FCSTD DOCUMENT  (FreeCAD 0.18.4R)
Label: Crane-04
License: All rights reserved
LicenseURL: http://en.wikipedia.org/wiki/All_rights_reserved
objects: Part::Cylinder×505, Part::MultiFuse×292, Part::Cut×223, Part::Box×206, Part::Fillet×87, Part::Feature×32, Part::Chamfer×30, Part::Extrusion×26, App::DocumentObjectGroup×7, Part::Mirroring×5, Part::Cone×4, Part::FeaturePython×4, Part::RegularPolygon×2
note: 1416 computed .brp shape members not serialized (recipe doc carries the construction recipe); baked Part::Feature solids carry a one-line shape summary decoded from their .brp

FEATURE [Part::Box] Box001  label="Cube001"
  AttacherType = Attacher::AttachEngine3D
  Height = 125
  Length = 30
  Placement = pos=(1,0,3) rot=(0,-1,0;0.20944rad)
  Width = 25
FEATURE [Part::Box] Box002  label="Cube002"
  AttacherType = Attacher::AttachEngine3D
  Height = 135
  Length = 26
  Placement = pos=(22,0,13) rot=(0,-1,0;0.261799rad)
  Width = 25
FEATURE [Part::Box] Box003  label="Cube003"
  AttacherType = Attacher::AttachEngine3D
  Height = 145
  Length = 35
  Placement = pos=(5,3,1) rot=(0,-1,0;0.20944rad)
  Width = 19
FEATURE [Part::Box] Box007  label="Cube004"
  AttacherType = Attacher::AttachEngine3D
  Height = 11
  Length = 25
  Placement = pos=(1,0,-2) rot=(0,0,1;0rad)
  Width = 25
FEATURE [Part::Fillet] Fillet
  Base = -> Box002
  Edges = 1 edges r=10: [Edge4]
  Placement = pos=(6,0,4) rot=(0,0,1;0rad)
FEATURE [Part::Box] Box017  label="Cube015"
  AttacherType = Attacher::AttachEngine3D
  Height = 30
  Length = 35
  Placement = pos=(1,0,0) rot=(0,0,1;0rad)
  Width = 25
FEATURE [Part::Box] Box018  label="Cube016"
  AttacherType = Attacher::AttachEngine3D
  Height = 30
  Length = 190
  Placement = pos=(1,0,105) rot=(0,0,1;0rad)
  Width = 25
FEATURE [Part::Box] Box019  label="Cube017"
  AttacherType = Attacher::AttachEngine3D
  Height = 10
  Length = 80
  Placement = pos=(65,0,105) rot=(0,0,1;0rad)
  Width = 25
FEATURE [Part::Cut] Cut002
  Base = -> Box018
  Refine = true
  Tool = -> Box019
FEATURE [Part::Feature] Solid
  shape: bbox 71.89 x 27.5 x 16.57 mm, 5 faces (baked)
FEATURE [Part::Cut] Cut003
  Base = -> Cut002
  Refine = true
  Tool = -> Solid
FEATURE [Part::Box] Box020  label="Cube018"
  AttacherType = Attacher::AttachEngine3D
  Height = 5
  Length = 46
  Placement = pos=(145,0,105) rot=(0,0,1;0rad)
  Width = 25
FEATURE [Part::Cut] Cut004
  Base = -> Cut003
  Refine = true
  Tool = -> Box020
FEATURE [Part::Feature] Solid001
  shape: bbox 51.52 x 27.5 x 8.266 mm, 5 faces (baked)
FEATURE [Part::Cut] Cut005
  Base = -> Cut004
  Refine = true
  Tool = -> Solid001
FEATURE [Part::Box] Box021  label="Cube019"
  AttacherType = Attacher::AttachEngine3D
  Height = 19
  Length = 46
  Placement = pos=(0,0,115) rot=(0,-1,0;0.610865rad)
  Width = 25
FEATURE [Part::Chamfer] Chamfer
  Base = -> Cut005
  Edges = 1 edges: [Edge13 r1=20 r2=18]
FEATURE [Part::Cut] Cut006
  Base = -> Chamfer
  Placement = pos=(-19,0,10) rot=(0,0,1;0rad)
  Refine = true
  Tool = -> Box021
FEATURE [Part::Box] Box022  label="Cube020"
  AttacherType = Attacher::AttachEngine3D
  Height = 30
  Length = 190
  Placement = pos=(-18,3,112) rot=(0,0,1;0rad)
  Width = 19
FEATURE [Part::Cut] Cut007
  Base = -> Cut006
  Placement = pos=(0,0,1) rot=(0,0,1;0rad)
  Refine = true
  Tool = -> Box022
FEATURE [Part::Fillet] Fillet003
  Base = -> Cut007
  Edges = 6 edges r=3: [Edge9,Edge13,Edge15,Edge17,Edge30,Edge41]
  Placement = pos=(-98.4842,0,33.7999) rot=(0,1,0;0.872665rad)
FEATURE [Part::Feature] Face001
  shape: bbox 65.47 x 2e-07 x 51.48 mm, 1 faces, 0 solids (baked)
FEATURE [Part::Extrusion] Extrude001
  Base = -> Face001
  Dir = (0,3,0)
  DirMode = 0
  FaceMakerClass = Part::FaceMakerExtrusion
  LengthFwd = 0
  LengthRev = 0
  Placement = pos=(0,-1,0) rot=(0,0,1;0rad)
  Solid = false
  Symmetric = false
FEATURE [Part::Fillet] Fillet006
  Base = -> Extrude001
  Edges = 1 edges r=3: [Edge8]
FEATURE [Part::Fillet] Fillet007
  Base = -> Fillet006
  Edges = 2 edges r=5: [Edge3,Edge12]
FEATURE [Part::Cylinder] Cylinder
  Angle = 360
  AttacherType = Attacher::AttachEngine3D
  Height = 25
  Placement = pos=(-13,25,122.5) rot=(1,0,0;1.5708rad)
  Radius = 5
FEATURE [Part::Box] Box023  label="Cube021"
  AttacherType = Attacher::AttachEngine3D
  Height = 64
  Length = 26
  Placement = pos=(-19,0,87) rot=(0,-1,0;0.279253rad)
  Width = 25
FEATURE [Part::Cut] Cut008
  Base = -> Fillet003
  Placement = pos=(89.1967,0,53.7171) rot=(0,-1,0;0.872665rad)
  Refine = true
  Tool = -> Box023
FEATURE [Part::Fillet] Fillet008
  Base = -> Cut008
  Edges = 2 edges r=3: [Edge21,Edge25]
FEATURE [Part::Cylinder] Cylinder001
  Angle = 360
  AttacherType = Attacher::AttachEngine3D
  Height = 27
  Placement = pos=(-13,26,122.5) rot=(1,0,0;1.5708rad)
  Radius = 3.1
FEATURE [Part::Cylinder] Cylinder002
  Angle = 360
  AttacherType = Attacher::AttachEngine3D
  Height = 27
  Placement = pos=(31,26,7) rot=(1,0,0;1.5708rad)
  Radius = 1.5
FEATURE [Part::Cylinder] Cylinder003
  Angle = 360
  AttacherType = Attacher::AttachEngine3D
  Height = 29
  Placement = pos=(20,27,130) rot=(1,0,0;1.5708rad)
  Radius = 1.5
FEATURE [Part::Cylinder] Cylinder004
  Angle = 360
  AttacherType = Attacher::AttachEngine3D
  Height = 25
  Placement = pos=(166,25,126) rot=(1,0,0;1.5708rad)
  Radius = 1.6
FEATURE [Part::Box] Box  label="Cube"
  AttacherType = Attacher::AttachEngine3D
  Height = 26
  Length = 40
  Placement = pos=(131,0,105) rot=(0,0,1;0rad)
  Width = 5
FEATURE [Part::Box] Box024  label="Cube022"
  AttacherType = Attacher::AttachEngine3D
  Height = 25
  Length = 60
  Placement = pos=(108,0,105) rot=(0,1,0;0.357792rad)
  Width = 5
FEATURE [Part::Cut] Cut009
  Base = -> Box
  Refine = true
  Tool = -> Box024
FEATURE [Part::Cylinder] Cylinder005
  Angle = 360
  AttacherType = Attacher::AttachEngine3D
  Height = 25
  Placement = pos=(166,25,115) rot=(1,0,0;1.5708rad)
  Radius = 1.6
FEATURE [Part::Cylinder] Cylinder006
  Angle = 360
  AttacherType = Attacher::AttachEngine3D
  Height = 25
  Placement = pos=(136,25,126) rot=(1,0,0;1.5708rad)
  Radius = 1.6
FEATURE [Part::Fillet] Fillet009
  Base = -> Cut009
  Edges = 4 edges r=3: [Edge2,Edge4,Edge9,Edge12]
  Placement = pos=(0,3,0) rot=(0,0,1;0rad)
FEATURE [Part::Box] Box025  label="Cube023"
  AttacherType = Attacher::AttachEngine3D
  Height = 26
  Length = 40
  Placement = pos=(131,0,105) rot=(0,0,1;0rad)
  Width = 5
FEATURE [Part::Box] Box026  label="Cube024"
  AttacherType = Attacher::AttachEngine3D
  Height = 25
  Length = 60
  Placement = pos=(108,0,105) rot=(0,1,0;0.357792rad)
  Width = 5
FEATURE [Part::Cut] Cut010
  Base = -> Box025
  Refine = true
  Tool = -> Box026
FEATURE [Part::Fillet] Fillet010
  Base = -> Cut010
  Edges = 4 edges r=3: [Edge2,Edge4,Edge9,Edge12]
  Placement = pos=(0,25,0) rot=(0,0,1;0rad)
FEATURE [Part::Cylinder] Cylinder007
  Angle = 360
  AttacherType = Attacher::AttachEngine3D
  Height = 25
  Placement = pos=(166,25,126) rot=(1,0,0;1.5708rad)
  Radius = 1.25
FEATURE [Part::Cylinder] Cylinder008
  Angle = 360
  AttacherType = Attacher::AttachEngine3D
  Height = 25
  Placement = pos=(136,25,126) rot=(1,0,0;1.5708rad)
  Radius = 1.25
FEATURE [Part::Cylinder] Cylinder009
  Angle = 360
  AttacherType = Attacher::AttachEngine3D
  Height = 25
  Placement = pos=(166,25,115) rot=(1,0,0;1.5708rad)
  Radius = 1.25
FEATURE [Part::MultiFuse] Fusion002
  Refine = true
  Shapes = -> [Cylinder004,Cylinder006,Cylinder005]
FEATURE [Part::MultiFuse] Fusion003
  Placement = pos=(0,5,0) rot=(0,0,1;0rad)
  Refine = true
  Shapes = -> [Cylinder007,Cylinder009,Cylinder008]
FEATURE [Part::Box] Box027  label="Cube025"
  AttacherType = Attacher::AttachEngine3D
  Height = 200
  Length = 29
  Placement = pos=(155,30,-59) rot=(0,0,1;0rad)
  Width = 17
FEATURE [Part::Box] Box028  label="Cube026"
  AttacherType = Attacher::AttachEngine3D
  Height = 200
  Length = 20.5
  Placement = pos=(159.25,33.25,-59) rot=(0,0,1;0rad)
  Width = 10.5
FEATURE [Part::Cylinder] Cylinder013
  Angle = 360
  AttacherType = Attacher::AttachEngine3D
  Height = 12
  Placement = pos=(13,12.5,-3) rot=(0,0,1;0rad)
  Radius = 2.5
FEATURE [Part::Box] Box030  label="Cube028"
  AttacherType = Attacher::AttachEngine3D
  Height = 5
  Length = 35
  Placement = pos=(1,3,4) rot=(0,0,1;0rad)
  Width = 19
FEATURE [Part::Cylinder] Cylinder020
  Angle = 360
  AttacherType = Attacher::AttachEngine3D
  Height = 25
  Placement = pos=(-19.5,25,121.5) rot=(1,0,0;1.5708rad)
  Radius = 4
FEATURE [Part::Cylinder] Cylinder028
  Angle = 360
  AttacherType = Attacher::AttachEngine3D
  Height = 25
  Placement = pos=(-4,25,63) rot=(1,0,0;1.5708rad)
  Radius = 5
FEATURE [Part::Cylinder] Cylinder029
  Angle = 360
  AttacherType = Attacher::AttachEngine3D
  Height = 25
  Placement = pos=(31,25,7) rot=(1,0,0;1.5708rad)
  Radius = 5
FEATURE [Part::Chamfer] Chamfer002
  Base = -> Fillet008
  Edges = 2 edges r=6: [Edge58,Edge66]
FEATURE [Part::Cylinder] Cylinder030
  Angle = 360
  AttacherType = Attacher::AttachEngine3D
  Height = 26
  Radius = 7.5
FEATURE [Part::Box] Box036  label="Cube034"
  AttacherType = Attacher::AttachEngine3D
  Height = 26
  Length = 10.4
  Placement = pos=(-5.2,-8.05,0) rot=(0,0,1;0rad)
  Width = 16.1
FEATURE [Part::Cut] Cut020
  Base = -> Cylinder030
  Refine = true
  Tool = -> Box036
FEATURE [Part::Cone] Cone
  Angle = 360
  AttacherType = Attacher::AttachEngine3D
  Height = 13
  Placement = pos=(0,0,-13) rot=(0,0,1;0rad)
  Radius1 = 5
  Radius2 = 7.5
FEATURE [Part::Box] Box037  label="Cube035"
  AttacherType = Attacher::AttachEngine3D
  Height = 12
  Length = 16
  Placement = pos=(-8,3,-12) rot=(0,0,1;0rad)
  Width = 10
FEATURE [Part::Box] Box038  label="Cube036"
  AttacherType = Attacher::AttachEngine3D
  Height = 12
  Length = 16
  Placement = pos=(-8,-13,-12) rot=(0,0,1;0rad)
  Width = 10
FEATURE [Part::MultiFuse] Fusion020
  Placement = pos=(0,0,-1) rot=(0,0,1;0rad)
  Refine = true
  Shapes = -> [Box038,Box037]
FEATURE [Part::Cylinder] Cylinder031
  Angle = 360
  AttacherType = Attacher::AttachEngine3D
  Height = 10
  Placement = pos=(0,5,-8) rot=(1,0,0;1.5708rad)
  Radius = 3.1
FEATURE [Part::Cylinder] Cylinder032
  Angle = 360
  AttacherType = Attacher::AttachEngine3D
  Height = 2
  Placement = pos=(0,0,-2) rot=(0,0,1;0rad)
  Radius = 7.5
FEATURE [Part::Cut] Cut021
  Base = -> Cone
  Refine = true
  Tool = -> Fusion020
FEATURE [Part::MultiFuse] Fusion021
  Refine = true
  Shapes = -> [Cut020,Cut021,Cylinder032]
FEATURE [Part::Cut] Cut022
  Base = -> Fusion021
  Refine = true
  Tool = -> Cylinder031
FEATURE [Part::Cylinder] Cylinder033
  Angle = 360
  AttacherType = Attacher::AttachEngine3D
  Height = 16
  Radius = 7.5
FEATURE [Part::Cylinder] Cylinder034
  Angle = 360
  AttacherType = Attacher::AttachEngine3D
  Height = 16
  Radius = 6.25
FEATURE [Part::Cut] Cut023
  Base = -> Cylinder033
  Refine = true
  Tool = -> Cylinder034
FEATURE [Part::MultiFuse] Fusion022
  Refine = true
  Shapes = -> [Cut022,Cut023]
FEATURE [Part::Box] Box004  label="Cube006"
  AttacherType = Attacher::AttachEngine3D
  Height = 2.5
  Length = 10
  Placement = pos=(2,-2,-0.5) rot=(0,0,1;0rad)
  Width = 4
FEATURE [Part::Cut] Cut024
  Base = -> Fusion022
  Placement = pos=(0,40,0) rot=(-1,0,0;1.5708rad)
  Refine = true
  Tool = -> Box004
FEATURE [Part::Cylinder] Cylinder014
  Angle = 360
  AttacherType = Attacher::AttachEngine3D
  Height = 5
  Placement = pos=(0,0,4) rot=(0,0,1;0rad)
  Radius = 3
FEATURE [Part::Cylinder] Cylinder015
  Angle = 360
  AttacherType = Attacher::AttachEngine3D
  Height = 8
  Placement = pos=(0,4,0) rot=(1,0,0;1.5708rad)
  Radius = 6
FEATURE [Part::Cylinder] Cylinder035
  Angle = 360
  AttacherType = Attacher::AttachEngine3D
  Height = 8
  Placement = pos=(0,4,0) rot=(1,0,0;1.5708rad)
  Radius = 3.1
FEATURE [Part::Cut] Cut025
  Base = -> Cylinder015
  Placement = pos=(0,0,-1) rot=(0,0,1;0rad)
  Refine = true
  Tool = -> Cylinder035
FEATURE [Part::Box] Box005  label="Cube007"
  AttacherType = Attacher::AttachEngine3D
  Height = 10
  Length = 6
  Placement = pos=(-3,2,4) rot=(0,0,1;0rad)
  Width = 2
FEATURE [Part::Box] Box006  label="Cube009"
  AttacherType = Attacher::AttachEngine3D
  Height = 10
  Length = 10
  Placement = pos=(-5,-5,4) rot=(0,0,1;0rad)
  Width = 10
FEATURE [Part::Cut] Cut026
  Base = -> Cut025
  Refine = true
  Tool = -> Box006
FEATURE [Part::Cut] Cut027
  Base = -> Cylinder014
  Refine = true
  Tool = -> Box005
FEATURE [Part::MultiFuse] Fusion023  label="cylinder-piston-head-attach"
  Placement = pos=(0,0,168) rot=(1,0,0;3.14159rad)
  Refine = true
  Shapes = -> [Cut026,Cut027]
FEATURE [Part::Fillet] Fillet012  label="cylinder-motor-holder"
  Base = -> Cut024
  Edges = 3 edges r=3: [Edge56,Edge61,Edge65]
  Placement = pos=(0,0,0) rot=(1,0,0;1.5708rad)
FEATURE [Part::Cylinder] Cylinder036  label="cylinder-jacket"
  Angle = 360
  AttacherType = Attacher::AttachEngine3D
  Height = 85
  Placement = pos=(0,0,38) rot=(0,0,1;0rad)
  Radius = 8
FEATURE [Part::MultiFuse] Fusion024  label="cylinder-body"
  Placement = pos=(31,12.5,-20) rot=(0,0,1;0rad)
  Refine = true
  Shapes = -> [Cylinder036,Fillet012]
FEATURE [Part::Cylinder] Cylinder037  label="cylinder-piston-rod"
  Angle = 360
  AttacherType = Attacher::AttachEngine3D
  Height = 80
  Placement = pos=(0,0,84) rot=(0,0,1;0rad)
  Radius = 4
FEATURE [Part::MultiFuse] Fusion025  label="cylinder-piston"
  Placement = pos=(31,12.5,-33.5) rot=(0,0,1;0rad)
  Refine = true
  Shapes = -> [Fusion023,Cylinder037]
FEATURE [Part::Box] Box039  label="Cube037"
  AttacherType = Attacher::AttachEngine3D
  Height = 14
  Length = 15
  Placement = pos=(23,9,1) rot=(0,0,1;0rad)
  Width = 7
FEATURE [Part::Feature] Face007
  shape: bbox 32.17 x 2e-07 x 34.8 mm, 1 faces, 0 solids (baked)
FEATURE [Part::Extrusion] Extrude007
  Base = -> Face007
  Dir = (0,3,0)
  DirMode = 0
  FaceMakerClass = Part::FaceMakerExtrusion
  LengthFwd = 0
  LengthRev = 0
  Solid = false
  Symmetric = false
FEATURE [Part::Fillet] Fillet013
  Base = -> Extrude007
  Edges = 1 edges r=1: [Edge5]
  Placement = pos=(0,-1,0) rot=(0,0,1;0rad)
FEATURE [Part::MultiFuse] Fusion034
  Refine = true
  Shapes = -> [Fillet007,Fillet013]
FEATURE [Part::Fillet] Fillet016
  Base = -> Fusion034
  Edges = 1 edges r=1: [Edge22]
FEATURE [Part::Cylinder] Cylinder044
  Angle = 360
  AttacherType = Attacher::AttachEngine3D
  Height = 29
  Placement = pos=(-3,27,133) rot=(1,0,0;1.5708rad)
  Radius = 1.5
FEATURE [Part::Cylinder] Cylinder045
  Angle = 360
  AttacherType = Attacher::AttachEngine3D
  Height = 29
  Placement = pos=(11,27,142) rot=(1,0,0;1.5708rad)
  Radius = 1.5
FEATURE [Part::Cylinder] Cylinder047
  Angle = 360
  AttacherType = Attacher::AttachEngine3D
  Height = 29
  Placement = pos=(38,27,129) rot=(1,0,0;1.5708rad)
  Radius = 1.5
FEATURE [Part::Cylinder] Cylinder048
  Angle = 360
  AttacherType = Attacher::AttachEngine3D
  Height = 27
  Placement = pos=(-13,26,122.5) rot=(1,0,0;1.5708rad)
  Radius = 1.5
FEATURE [Part::MultiFuse] Fusion035
  Refine = true
  Shapes = -> [Cylinder003,Cylinder044,Cylinder045,Cylinder047,Cylinder048]
FEATURE [Part::Cut] Cut037  label="crane-secondary-arm-left-plate"
  Base = -> Fillet016
  Placement = pos=(162,58,35) rot=(0,0,1;0rad)
  Refine = true
  Tool = -> Fusion035
FEATURE [Part::Feature] Face008
  shape: bbox 65.47 x 2e-07 x 51.48 mm, 1 faces, 0 solids (baked)
FEATURE [Part::Extrusion] Extrude008
  Base = -> Face008
  Dir = (0,3,0)
  DirMode = 0
  FaceMakerClass = Part::FaceMakerExtrusion
  LengthFwd = 0
  LengthRev = 0
  Placement = pos=(0,-1,0) rot=(0,0,1;0rad)
  Solid = false
  Symmetric = false
FEATURE [Part::Fillet] Fillet017
  Base = -> Extrude008
  Edges = 1 edges r=3: [Edge8]
FEATURE [Part::Fillet] Fillet018
  Base = -> Fillet017
  Edges = 2 edges r=5: [Edge3,Edge12]
FEATURE [Part::Cylinder] Cylinder049
  Angle = 360
  AttacherType = Attacher::AttachEngine3D
  Height = 29
  Placement = pos=(20,27,130) rot=(1,0,0;1.5708rad)
  Radius = 1.5
FEATURE [Part::Feature] Face009
  shape: bbox 32.17 x 2e-07 x 34.8 mm, 1 faces, 0 solids (baked)
FEATURE [Part::Extrusion] Extrude009
  Base = -> Face009
  Dir = (0,3,0)
  DirMode = 0
  FaceMakerClass = Part::FaceMakerExtrusion
  LengthFwd = 0
  LengthRev = 0
  Solid = false
  Symmetric = false
FEATURE [Part::Fillet] Fillet019
  Base = -> Extrude009
  Edges = 1 edges r=1: [Edge5]
  Placement = pos=(0,-1,0) rot=(0,0,1;0rad)
FEATURE [Part::MultiFuse] Fusion036
  Refine = true
  Shapes = -> [Fillet018,Fillet019]
FEATURE [Part::Fillet] Fillet020
  Base = -> Fusion036
  Edges = 1 edges r=1: [Edge22]
FEATURE [Part::Cylinder] Cylinder050
  Angle = 360
  AttacherType = Attacher::AttachEngine3D
  Height = 29
  Placement = pos=(-3,27,133) rot=(1,0,0;1.5708rad)
  Radius = 1.5
FEATURE [Part::Cylinder] Cylinder051
  Angle = 360
  AttacherType = Attacher::AttachEngine3D
  Height = 29
  Placement = pos=(11,27,142) rot=(1,0,0;1.5708rad)
  Radius = 1.5
FEATURE [Part::Cylinder] Cylinder052
  Angle = 360
  AttacherType = Attacher::AttachEngine3D
  Height = 29
  Placement = pos=(38,27,129) rot=(1,0,0;1.5708rad)
  Radius = 1.5
FEATURE [Part::Cylinder] Cylinder053
  Angle = 360
  AttacherType = Attacher::AttachEngine3D
  Height = 27
  Placement = pos=(-13,26,122.5) rot=(1,0,0;1.5708rad)
  Radius = 1.5
FEATURE [Part::MultiFuse] Fusion037
  Refine = true
  Shapes = -> [Cylinder049,Cylinder050,Cylinder051,Cylinder052,Cylinder053]
FEATURE [Part::Cut] Cut038  label="crane-secondary-arm-right-plate"
  Base = -> Fillet020
  Placement = pos=(162,86,35) rot=(0,0,1;0rad)
  Refine = true
  Tool = -> Fusion037
FEATURE [Part::Cylinder] Cylinder055
  Angle = 360
  AttacherType = Attacher::AttachEngine3D
  Height = 25
  Placement = pos=(11,25,142) rot=(1,0,0;1.5708rad)
  Radius = 4
FEATURE [Part::Cylinder] Cylinder065
  Angle = 360
  AttacherType = Attacher::AttachEngine3D
  Height = 19
  Placement = pos=(20,22,130) rot=(1,0,0;1.5708rad)
  Radius = 5
FEATURE [Part::Cylinder] Cylinder066
  Angle = 360
  AttacherType = Attacher::AttachEngine3D
  Height = 25
  Placement = pos=(43,25,129) rot=(1,0,0;1.5708rad)
  Radius = 1.6
FEATURE [Part::Cylinder] Cylinder071
  Angle = 360
  AttacherType = Attacher::AttachEngine3D
  Height = 25
  Placement = pos=(166,25,126.5) rot=(1,0,0;1.5708rad)
  Radius = 3.1
FEATURE [Part::MultiFuse] Fusion044  label="cylinder-lifter"
  Placement = pos=(163,60,26.5) rot=(0,-1,0;0.094248rad)
  Refine = true
  Shapes = -> [Fusion025,Fusion024]
FEATURE [Part::Cylinder] Cylinder072
  Angle = 360
  AttacherType = Attacher::AttachEngine3D
  Height = 26
  Radius = 7.5
FEATURE [Part::Box] Box040  label="Cube038"
  AttacherType = Attacher::AttachEngine3D
  Height = 26
  Length = 10.4
  Placement = pos=(-5.2,-8.05,0) rot=(0,0,1;0rad)
  Width = 16.1
FEATURE [Part::Cut] Cut039
  Base = -> Cylinder072
  Refine = true
  Tool = -> Box040
FEATURE [Part::Cone] Cone001
  Angle = 360
  AttacherType = Attacher::AttachEngine3D
  Height = 13
  Placement = pos=(0,0,-13) rot=(0,0,1;0rad)
  Radius1 = 5
  Radius2 = 7.5
FEATURE [Part::Box] Box041  label="Cube039"
  AttacherType = Attacher::AttachEngine3D
  Height = 12
  Length = 16
  Placement = pos=(-8,3,-12) rot=(0,0,1;0rad)
  Width = 10
FEATURE [Part::Box] Box042  label="Cube040"
  AttacherType = Attacher::AttachEngine3D
  Height = 12
  Length = 16
  Placement = pos=(-8,-13,-12) rot=(0,0,1;0rad)
  Width = 10
FEATURE [Part::MultiFuse] Fusion045
  Placement = pos=(0,0,-1) rot=(0,0,1;0rad)
  Refine = true
  Shapes = -> [Box042,Box041]
FEATURE [Part::Cylinder] Cylinder073
  Angle = 360
  AttacherType = Attacher::AttachEngine3D
  Height = 10
  Placement = pos=(0,5,-8) rot=(1,0,0;1.5708rad)
  Radius = 3.1
FEATURE [Part::Cylinder] Cylinder074
  Angle = 360
  AttacherType = Attacher::AttachEngine3D
  Height = 2
  Placement = pos=(0,0,-2) rot=(0,0,1;0rad)
  Radius = 7.5
FEATURE [Part::Cut] Cut040
  Base = -> Cone001
  Refine = true
  Tool = -> Fusion045
FEATURE [Part::MultiFuse] Fusion046
  Refine = true
  Shapes = -> [Cut039,Cut040,Cylinder074]
FEATURE [Part::Cut] Cut041
  Base = -> Fusion046
  Refine = true
  Tool = -> Cylinder073
FEATURE [Part::Cylinder] Cylinder075
  Angle = 360
  AttacherType = Attacher::AttachEngine3D
  Height = 16
  Radius = 7.5
FEATURE [Part::Cylinder] Cylinder076
  Angle = 360
  AttacherType = Attacher::AttachEngine3D
  Height = 16
  Radius = 6.25
FEATURE [Part::Cut] Cut042
  Base = -> Cylinder075
  Refine = true
  Tool = -> Cylinder076
FEATURE [Part::MultiFuse] Fusion047
  Refine = true
  Shapes = -> [Cut041,Cut042]
FEATURE [Part::Box] Box043  label="Cube041"
  AttacherType = Attacher::AttachEngine3D
  Height = 2.5
  Length = 10
  Placement = pos=(2,-2,-0.5) rot=(0,0,1;0rad)
  Width = 4
FEATURE [Part::Cut] Cut043
  Base = -> Fusion047
  Placement = pos=(0,40,0) rot=(-1,0,0;1.5708rad)
  Refine = true
  Tool = -> Box043
FEATURE [Part::Cylinder] Cylinder077
  Angle = 360
  AttacherType = Attacher::AttachEngine3D
  Height = 5
  Placement = pos=(0,0,4) rot=(0,0,1;0rad)
  Radius = 3
FEATURE [Part::Cylinder] Cylinder078
  Angle = 360
  AttacherType = Attacher::AttachEngine3D
  Height = 8
  Placement = pos=(0,4,0) rot=(1,0,0;1.5708rad)
  Radius = 6
FEATURE [Part::Cylinder] Cylinder079
  Angle = 360
  AttacherType = Attacher::AttachEngine3D
  Height = 8
  Placement = pos=(0,4,0) rot=(1,0,0;1.5708rad)
  Radius = 3.1
FEATURE [Part::Cut] Cut044
  Base = -> Cylinder078
  Placement = pos=(0,0,-1) rot=(0,0,1;0rad)
  Refine = true
  Tool = -> Cylinder079
FEATURE [Part::Box] Box044  label="Cube042"
  AttacherType = Attacher::AttachEngine3D
  Height = 10
  Length = 6
  Placement = pos=(-3,2,4) rot=(0,0,1;0rad)
  Width = 2
FEATURE [Part::Box] Box045  label="Cube043"
  AttacherType = Attacher::AttachEngine3D
  Height = 10
  Length = 10
  Placement = pos=(-5,-5,4) rot=(0,0,1;0rad)
  Width = 10
FEATURE [Part::Cut] Cut045
  Base = -> Cut044
  Refine = true
  Tool = -> Box045
FEATURE [Part::Cut] Cut046
  Base = -> Cylinder077
  Refine = true
  Tool = -> Box044
FEATURE [Part::MultiFuse] Fusion048  label="cylinder-piston-head-attach001"
  Placement = pos=(0,0,168) rot=(1,0,0;3.14159rad)
  Refine = true
  Shapes = -> [Cut045,Cut046]
FEATURE [Part::Fillet] Fillet021  label="cylinder-motor-holder001"
  Base = -> Cut043
  Edges = 3 edges r=3: [Edge56,Edge61,Edge65]
  Placement = pos=(0,0,0) rot=(1,0,0;1.5708rad)
FEATURE [Part::Cylinder] Cylinder080  label="cylinder-jacket001"
  Angle = 360
  AttacherType = Attacher::AttachEngine3D
  Height = 85
  Placement = pos=(0,0,38) rot=(0,0,1;0rad)
  Radius = 8
FEATURE [Part::MultiFuse] Fusion049  label="cylinder-body001"
  Placement = pos=(31,12.5,-20) rot=(0,0,1;0rad)
  Refine = true
  Shapes = -> [Cylinder080,Fillet021]
FEATURE [Part::Cylinder] Cylinder081  label="cylinder-piston-rod001"
  Angle = 360
  AttacherType = Attacher::AttachEngine3D
  Height = 53
  Placement = pos=(0,0,111) rot=(0,0,1;0rad)
  Radius = 4
FEATURE [Part::MultiFuse] Fusion050  label="cylinder-piston001"
  Placement = pos=(31,12.5,-12) rot=(0,0,1;0rad)
  Refine = true
  Shapes = -> [Fusion048,Cylinder081]
FEATURE [Part::MultiFuse] Fusion051  label="cylinder-arm"
  Placement = pos=(196.5,60,197) rot=(0,1,0;1.64934rad)
  Refine = true
  Shapes = -> [Fusion050,Fusion049]
FEATURE [Part::Cylinder] Cylinder082  label="Cylinder080"
  Angle = 360
  AttacherType = Attacher::AttachEngine3D
  Height = 11
  Placement = pos=(9,18,-2) rot=(0,0,1;0rad)
  Radius = 1.25
FEATURE [Part::Cylinder] Cylinder083  label="Cylinder081"
  Angle = 360
  AttacherType = Attacher::AttachEngine3D
  Height = 11
  Placement = pos=(9,7,-2) rot=(0,0,1;0rad)
  Radius = 1.25
FEATURE [Part::Cylinder] Cylinder084  label="Cylinder259"
  Angle = 360
  AttacherType = Attacher::AttachEngine3D
  Height = 11
  Placement = pos=(18,18,-2) rot=(0,0,1;0rad)
  Radius = 1.25
FEATURE [Part::Cylinder] Cylinder085  label="Cylinder260"
  Angle = 360
  AttacherType = Attacher::AttachEngine3D
  Height = 11
  Placement = pos=(18,7,-2) rot=(0,0,1;0rad)
  Radius = 1.25
FEATURE [Part::Box] Box046  label="Cube044"
  AttacherType = Attacher::AttachEngine3D
  Height = 18
  Length = 13
  Placement = pos=(29,3,125) rot=(0,0,1;0rad)
  Width = 19
FEATURE [Part::Fillet] Fillet022
  Base = -> Box046
  Edges = 2 edges r=4: [Edge4,Edge8]
FEATURE [Part::Box] Box047  label="Cube045"
  AttacherType = Attacher::AttachEngine3D
  Height = 12
  Length = 13
  Placement = pos=(31,9,125) rot=(0,0,1;0rad)
  Width = 7
FEATURE [Part::Cut] Cut048
  Base = -> Fillet022
  Refine = true
  Tool = -> Box047
FEATURE [Part::Fillet] Fillet023
  Base = -> Cut048
  Edges = 1 edges r=3: [Edge35]
  Placement = pos=(5,0,0.5) rot=(0,0,1;0rad)
FEATURE [Part::Cylinder] Cylinder086  label="Cylinder261"
  Angle = 360
  AttacherType = Attacher::AttachEngine3D
  Height = 29
  Placement = pos=(20,27,130) rot=(1,0,0;1.5708rad)
  Radius = 1.6
FEATURE [Part::Cylinder] Cylinder087  label="Cylinder262"
  Angle = 360
  AttacherType = Attacher::AttachEngine3D
  Height = 25
  Placement = pos=(328,85,161.5) rot=(1,0,0;1.5708rad)
  Radius = 1.5
FEATURE [Part::RegularPolygon] RegularPolygon001  label="Regular polygon001"
  AttacherType = Attacher::AttachEngine3D
  Circumradius = 3.25
  Placement = pos=(5,0,4) rot=(1,0,0;1.5708rad)
  Polygon = 6
FEATURE [Part::Feature] Face
  shape: bbox 8.306 x 2e-07 x 8.194 mm, 1 faces, 0 solids (baked)
FEATURE [Part::Extrusion] Extrude
  Base = -> Face
  Dir = (0,5,0)
  DirMode = 0
  FaceMakerClass = Part::FaceMakerExtrusion
  LengthFwd = 0
  LengthRev = 0
  Solid = false
  Symmetric = false
FEATURE [Part::Cylinder] Cylinder089  label="Cylinder263"
  Angle = 360
  AttacherType = Attacher::AttachEngine3D
  Height = 4
  Placement = pos=(5,25,4) rot=(1,0,0;1.5708rad)
  Radius = 3.25
FEATURE [Part::Cylinder] Cylinder090  label="Cylinder264"
  Angle = 360
  AttacherType = Attacher::AttachEngine3D
  Height = 25
  Placement = pos=(5,25,4) rot=(1,0,0;1.5708rad)
  Radius = 1.6
FEATURE [Part::MultiFuse] Fusion054
  Refine = true
  Shapes = -> [Extrude,Cylinder089,Cylinder090]
FEATURE [Part::Feature] Face010
  shape: bbox 8.306 x 2e-07 x 8.194 mm, 1 faces, 0 solids (baked)
FEATURE [Part::Extrusion] Extrude010
  Base = -> Face010
  Dir = (0,5,0)
  DirMode = 0
  FaceMakerClass = Part::FaceMakerExtrusion
  LengthFwd = 0
  LengthRev = 0
  Solid = false
  Symmetric = false
FEATURE [Part::Cylinder] Cylinder091  label="Cylinder265"
  Angle = 360
  AttacherType = Attacher::AttachEngine3D
  Height = 4
  Placement = pos=(5,25,4) rot=(1,0,0;1.5708rad)
  Radius = 3.25
FEATURE [Part::Cylinder] Cylinder092  label="Cylinder266"
  Angle = 360
  AttacherType = Attacher::AttachEngine3D
  Height = 25
  Placement = pos=(5,25,4) rot=(1,0,0;1.5708rad)
  Radius = 1.6
FEATURE [Part::MultiFuse] Fusion055
  Placement = pos=(17,0,0) rot=(0,0,1;0rad)
  Refine = true
  Shapes = -> [Extrude010,Cylinder091,Cylinder092]
FEATURE [Part::Feature] Face011
  shape: bbox 8.306 x 2e-07 x 8.194 mm, 1 faces, 0 solids (baked)
FEATURE [Part::Extrusion] Extrude011
  Base = -> Face011
  Dir = (0,5,0)
  DirMode = 0
  FaceMakerClass = Part::FaceMakerExtrusion
  LengthFwd = 0
  LengthRev = 0
  Solid = false
  Symmetric = false
FEATURE [Part::Cylinder] Cylinder093  label="Cylinder267"
  Angle = 360
  AttacherType = Attacher::AttachEngine3D
  Height = 4
  Placement = pos=(5,25,4) rot=(1,0,0;1.5708rad)
  Radius = 3.25
FEATURE [Part::Cylinder] Cylinder094  label="Cylinder268"
  Angle = 360
  AttacherType = Attacher::AttachEngine3D
  Height = 25
  Placement = pos=(5,25,4) rot=(1,0,0;1.5708rad)
  Radius = 1.6
FEATURE [Part::MultiFuse] Fusion056
  Placement = pos=(-9,0,59) rot=(0,0,1;0rad)
  Refine = true
  Shapes = -> [Extrude011,Cylinder093,Cylinder094]
FEATURE [Part::Feature] Face012
  shape: bbox 8.306 x 2e-07 x 8.194 mm, 1 faces, 0 solids (baked)
FEATURE [Part::Extrusion] Extrude012
  Base = -> Face012
  Dir = (0,5,0)
  DirMode = 0
  FaceMakerClass = Part::FaceMakerExtrusion
  LengthFwd = 0
  LengthRev = 0
  Solid = false
  Symmetric = false
FEATURE [Part::Cylinder] Cylinder095  label="Cylinder269"
  Angle = 360
  AttacherType = Attacher::AttachEngine3D
  Height = 4
  Placement = pos=(5,25,4) rot=(1,0,0;1.5708rad)
  Radius = 3.25
FEATURE [Part::Cylinder] Cylinder096  label="Cylinder270"
  Angle = 360
  AttacherType = Attacher::AttachEngine3D
  Height = 25
  Placement = pos=(5,25,4) rot=(1,0,0;1.5708rad)
  Radius = 1.6
FEATURE [Part::MultiFuse] Fusion057
  Placement = pos=(-24.5,0,117.5) rot=(0,0,1;0rad)
  Refine = true
  Shapes = -> [Extrude012,Cylinder095,Cylinder096]
FEATURE [Part::Cylinder] Cylinder097  label="Cylinder271"
  Angle = 360
  AttacherType = Attacher::AttachEngine3D
  Height = 25
  Placement = pos=(57,25,142) rot=(1,0,0;1.5708rad)
  Radius = 4
FEATURE [Part::Cylinder] Cylinder098  label="Cylinder272"
  Angle = 360
  AttacherType = Attacher::AttachEngine3D
  Height = 25
  Placement = pos=(105,25,141) rot=(1,0,0;1.5708rad)
  Radius = 5
FEATURE [Part::Cylinder] Cylinder099  label="Cylinder273"
  Angle = 360
  AttacherType = Attacher::AttachEngine3D
  Height = 25
  Placement = pos=(150,25,141) rot=(1,0,0;1.5708rad)
  Radius = 5
FEATURE [Part::Cylinder] Cylinder100  label="Cylinder274"
  Angle = 360
  AttacherType = Attacher::AttachEngine3D
  Height = 25
  Placement = pos=(5,25,136) rot=(1,0,0;1.5708rad)
  Radius = 5
FEATURE [Part::Cylinder] Cylinder101
  Angle = 360
  AttacherType = Attacher::AttachEngine3D
  Height = 25
  Placement = pos=(-3,25,133) rot=(1,0,0;1.5708rad)
  Radius = 3.2
FEATURE [Part::Feature] Face013
  shape: bbox 8.306 x 2e-07 x 8.194 mm, 1 faces, 0 solids (baked)
FEATURE [Part::Extrusion] Extrude013
  Base = -> Face013
  Dir = (0,5,0)
  DirMode = 0
  FaceMakerClass = Part::FaceMakerExtrusion
  LengthFwd = 0
  LengthRev = 0
  Solid = false
  Symmetric = false
FEATURE [Part::Cylinder] Cylinder102  label="Cylinder275"
  Angle = 360
  AttacherType = Attacher::AttachEngine3D
  Height = 4
  Placement = pos=(5,25,4) rot=(1,0,0;1.5708rad)
  Radius = 3.25
FEATURE [Part::Cylinder] Cylinder103  label="Cylinder276"
  Angle = 360
  AttacherType = Attacher::AttachEngine3D
  Height = 25
  Placement = pos=(5,25,4) rot=(1,0,0;1.5708rad)
  Radius = 1.6
FEATURE [Part::MultiFuse] Fusion060
  Placement = pos=(0,0,132) rot=(0,0,1;0rad)
  Refine = true
  Shapes = -> [Extrude013,Cylinder102,Cylinder103]
FEATURE [Part::Feature] Face014
  shape: bbox 8.306 x 2e-07 x 8.194 mm, 1 faces, 0 solids (baked)
FEATURE [Part::Extrusion] Extrude014
  Base = -> Face014
  Dir = (0,5,0)
  DirMode = 0
  FaceMakerClass = Part::FaceMakerExtrusion
  LengthFwd = 0
  LengthRev = 0
  Solid = false
  Symmetric = false
FEATURE [Part::Cylinder] Cylinder104  label="Cylinder277"
  Angle = 360
  AttacherType = Attacher::AttachEngine3D
  Height = 4
  Placement = pos=(5,25,4) rot=(1,0,0;1.5708rad)
  Radius = 3.25
FEATURE [Part::Cylinder] Cylinder105  label="Cylinder278"
  Angle = 360
  AttacherType = Attacher::AttachEngine3D
  Height = 25
  Placement = pos=(5,25,4) rot=(1,0,0;1.5708rad)
  Radius = 1.6
FEATURE [Part::MultiFuse] Fusion061
  Placement = pos=(52,0,138) rot=(0,0,1;0rad)
  Refine = true
  Shapes = -> [Extrude014,Cylinder104,Cylinder105]
FEATURE [Part::Feature] Face015
  shape: bbox 8.306 x 2e-07 x 8.194 mm, 1 faces, 0 solids (baked)
FEATURE [Part::Extrusion] Extrude015
  Base = -> Face015
  Dir = (0,5,0)
  DirMode = 0
  FaceMakerClass = Part::FaceMakerExtrusion
  LengthFwd = 0
  LengthRev = 0
  Solid = false
  Symmetric = false
FEATURE [Part::Cylinder] Cylinder106  label="Cylinder279"
  Angle = 360
  AttacherType = Attacher::AttachEngine3D
  Height = 4
  Placement = pos=(5,25,4) rot=(1,0,0;1.5708rad)
  Radius = 3.25
FEATURE [Part::Cylinder] Cylinder107  label="Cylinder165"
  Angle = 360
  AttacherType = Attacher::AttachEngine3D
  Height = 25
  Placement = pos=(5,25,4) rot=(1,0,0;1.5708rad)
  Radius = 1.6
FEATURE [Part::MultiFuse] Fusion062
  Placement = pos=(100,0,137) rot=(0,0,1;0rad)
  Refine = true
  Shapes = -> [Extrude015,Cylinder106,Cylinder107]
FEATURE [Part::Feature] Face016
  shape: bbox 8.306 x 2e-07 x 8.194 mm, 1 faces, 0 solids (baked)
FEATURE [Part::Extrusion] Extrude016
  Base = -> Face016
  Dir = (0,5,0)
  DirMode = 0
  FaceMakerClass = Part::FaceMakerExtrusion
  LengthFwd = 0
  LengthRev = 0
  Solid = false
  Symmetric = false
FEATURE [Part::Cylinder] Cylinder108  label="Cylinder280"
  Angle = 360
  AttacherType = Attacher::AttachEngine3D
  Height = 4
  Placement = pos=(5,25,4) rot=(1,0,0;1.5708rad)
  Radius = 3.25
FEATURE [Part::Cylinder] Cylinder109  label="Cylinder281"
  Angle = 360
  AttacherType = Attacher::AttachEngine3D
  Height = 25
  Placement = pos=(5,25,4) rot=(1,0,0;1.5708rad)
  Radius = 1.6
FEATURE [Part::MultiFuse] Fusion063
  Placement = pos=(145,0,137) rot=(0,0,1;0rad)
  Refine = true
  Shapes = -> [Extrude016,Cylinder108,Cylinder109]
FEATURE [Part::MultiFuse] Fusion065
  Refine = true
  Shapes = -> [Fusion060,Fusion061,Fusion063,Fusion062]
FEATURE [Part::Cylinder] Cylinder110  label="Cylinder282"
  Angle = 360
  AttacherType = Attacher::AttachEngine3D
  Height = 9
  Placement = pos=(20,17,130) rot=(1,0,0;1.5708rad)
  Radius = 5
FEATURE [Part::Cut] Cut053
  Base = -> Cylinder065
  Refine = true
  Tool = -> Cylinder110
FEATURE [Part::MultiFuse] Fusion066
  Refine = true
  Shapes = -> [Cut053,Cylinder055,Cylinder097,Cylinder101,Cylinder098,Cylinder099,Cylinder100]
FEATURE [Part::Cylinder] Cylinder111  label="Cylinder283"
  Angle = 360
  AttacherType = Attacher::AttachEngine3D
  Height = 8
  Placement = pos=(38,25,129) rot=(1,0,0;1.5708rad)
  Radius = 1.25
FEATURE [Part::Cylinder] Cylinder112  label="Cylinder284"
  Angle = 360
  AttacherType = Attacher::AttachEngine3D
  Height = 8
  Placement = pos=(38,8,129) rot=(1,0,0;1.5708rad)
  Radius = 1.25
FEATURE [Part::MultiFuse] Fusion069
  Refine = true
  Shapes = -> [Fillet023,Chamfer002]
FEATURE [Part::MultiFuse] Fusion070
  Refine = true
  Shapes = -> [Fusion069,Fusion066]
FEATURE [Part::Cut] Cut054
  Base = -> Fusion070
  Refine = true
  Tool = -> Fusion065
FEATURE [Part::Box] Box048  label="Cube046"
  AttacherType = Attacher::AttachEngine3D
  Height = 6
  Length = 10
  Placement = pos=(-4,10.5,16) rot=(0,-1,0;0.20944rad)
  Width = 4
FEATURE [Part::Fillet] Fillet024
  Base = -> Box048
  Edges = 4 edges r=1.5: [Edge9,Edge10,Edge11,Edge12]
FEATURE [Part::Cylinder] Cylinder113  label="Cylinder285"
  Angle = 360
  AttacherType = Attacher::AttachEngine3D
  Height = 10
  Placement = pos=(-7,3,30) rot=(0,1,0;1.36136rad)
  Radius = 1
FEATURE [Part::Cylinder] Cylinder114  label="Cylinder286"
  Angle = 360
  AttacherType = Attacher::AttachEngine3D
  Height = 10
  Placement = pos=(-7,22,30) rot=(0,1,0;1.36136rad)
  Radius = 1
FEATURE [Part::MultiFuse] Fusion071
  Refine = true
  Shapes = -> [Cylinder113,Cylinder114]
FEATURE [Part::Cylinder] Cylinder115  label="Cylinder287"
  Angle = 360
  AttacherType = Attacher::AttachEngine3D
  Height = 10
  Placement = pos=(-7,3,30) rot=(0,1,0;1.36136rad)
  Radius = 1
FEATURE [Part::Cylinder] Cylinder116  label="Cylinder288"
  Angle = 360
  AttacherType = Attacher::AttachEngine3D
  Height = 10
  Placement = pos=(-7,22,30) rot=(0,1,0;1.36136rad)
  Radius = 1
FEATURE [Part::MultiFuse] Fusion072
  Placement = pos=(-18,0,86) rot=(0,0,1;0rad)
  Refine = true
  Shapes = -> [Cylinder115,Cylinder116]
FEATURE [Part::Cylinder] Cylinder117  label="Cylinder289"
  Angle = 360
  AttacherType = Attacher::AttachEngine3D
  Height = 10
  Placement = pos=(-7,3,30) rot=(0,1,0;1.36136rad)
  Radius = 1
FEATURE [Part::Cylinder] Cylinder118  label="Cylinder290"
  Angle = 360
  AttacherType = Attacher::AttachEngine3D
  Height = 10
  Placement = pos=(-7,22,30) rot=(0,1,0;1.36136rad)
  Radius = 1
FEATURE [Part::MultiFuse] Fusion073
  Placement = pos=(-9,0,43) rot=(0,0,1;0rad)
  Refine = true
  Shapes = -> [Cylinder117,Cylinder118]
FEATURE [Part::MultiFuse] Fusion075
  Refine = true
  Shapes = -> [Fusion071,Fusion072,Fusion073]
FEATURE [Part::Cylinder] Cylinder119  label="Cylinder291"
  Angle = 360
  AttacherType = Attacher::AttachEngine3D
  Height = 10
  Placement = pos=(-7,3,30) rot=(0,0,1;0rad)
  Radius = 1
FEATURE [Part::Cylinder] Cylinder120  label="Cylinder292"
  Angle = 360
  AttacherType = Attacher::AttachEngine3D
  Height = 10
  Placement = pos=(-7,22,30) rot=(0,0,1;0rad)
  Radius = 1
FEATURE [Part::MultiFuse] Fusion076
  Placement = pos=(24,0,108) rot=(0,0,1;0rad)
  Refine = true
  Shapes = -> [Cylinder120,Cylinder119]
FEATURE [Part::Cylinder] Cylinder121  label="Cylinder179"
  Angle = 360
  AttacherType = Attacher::AttachEngine3D
  Height = 10
  Placement = pos=(-7,3,30) rot=(0,0,1;0rad)
  Radius = 1
FEATURE [Part::Cylinder] Cylinder122  label="Cylinder293"
  Angle = 360
  AttacherType = Attacher::AttachEngine3D
  Height = 10
  Placement = pos=(-7,22,30) rot=(0,0,1;0rad)
  Radius = 1
FEATURE [Part::MultiFuse] Fusion077
  Placement = pos=(150,0,108) rot=(0,0,1;0rad)
  Refine = true
  Shapes = -> [Cylinder122,Cylinder121]
FEATURE [Part::Cylinder] Cylinder123  label="Cylinder294"
  Angle = 360
  AttacherType = Attacher::AttachEngine3D
  Height = 10
  Placement = pos=(-7,3,30) rot=(0,0,1;0rad)
  Radius = 1
FEATURE [Part::Cylinder] Cylinder124  label="Cylinder295"
  Angle = 360
  AttacherType = Attacher::AttachEngine3D
  Height = 10
  Placement = pos=(-7,22,30) rot=(0,0,1;0rad)
  Radius = 1
FEATURE [Part::MultiFuse] Fusion078
  Placement = pos=(87,0,108) rot=(0,0,1;0rad)
  Refine = true
  Shapes = -> [Cylinder124,Cylinder123]
FEATURE [Part::MultiFuse] Fusion079
  Placement = pos=(0,0,0.5) rot=(0,0,1;0rad)
  Refine = true
  Shapes = -> [Fusion076,Fusion078,Fusion077]
FEATURE [Part::Cylinder] Cylinder125  label="Cylinder296"
  Angle = 360
  AttacherType = Attacher::AttachEngine3D
  Height = 4.8
  Placement = pos=(5,4.8,4) rot=(1,0,0;1.5708rad)
  Radius = 2.25
FEATURE [Part::Cylinder] Cylinder126  label="Cylinder297"
  Angle = 360
  AttacherType = Attacher::AttachEngine3D
  Height = 4.8
  Placement = pos=(22,4.8,4) rot=(1,0,0;1.5708rad)
  Radius = 2.25
FEATURE [Part::Cylinder] Cylinder127  label="Cylinder185"
  Angle = 360
  AttacherType = Attacher::AttachEngine3D
  Height = 4.8
  Placement = pos=(-4,4.8,63) rot=(1,0,0;1.5708rad)
  Radius = 2.25
FEATURE [Part::Cylinder] Cylinder128  label="Cylinder298"
  Angle = 360
  AttacherType = Attacher::AttachEngine3D
  Height = 4.8
  Placement = pos=(-19.5,4.8,121.5) rot=(1,0,0;1.5708rad)
  Radius = 2.25
FEATURE [Part::Cylinder] Cylinder129  label="Cylinder299"
  Angle = 360
  AttacherType = Attacher::AttachEngine3D
  Height = 4.8
  Placement = pos=(5,4.8,136) rot=(1,0,0;1.5708rad)
  Radius = 2.25
FEATURE [Part::MultiFuse] Fusion080  label="crane-main-arm-HEX-SUPPORTS"
  Placement = pos=(162,60,35) rot=(0,0,1;0rad)
  Refine = true
  Shapes = -> [Cylinder128,Cylinder125,Cylinder126,Cylinder127]
FEATURE [Part::Cylinder] Cylinder130  label="Cylinder300"
  Angle = 360
  AttacherType = Attacher::AttachEngine3D
  Height = 4.8
  Placement = pos=(57,4.8,142) rot=(1,0,0;1.5708rad)
  Radius = 2.25
FEATURE [Part::Cylinder] Cylinder131  label="Cylinder301"
  Angle = 360
  AttacherType = Attacher::AttachEngine3D
  Height = 4.8
  Placement = pos=(105,4.8,141) rot=(1,0,0;1.5708rad)
  Radius = 2.25
FEATURE [Part::Cylinder] Cylinder132  label="Cylinder302"
  Angle = 360
  AttacherType = Attacher::AttachEngine3D
  Height = 4.8
  Placement = pos=(150,4.8,141) rot=(1,0,0;1.5708rad)
  Radius = 2.25
FEATURE [Part::MultiFuse] Fusion081  label="crane-secondary-arm-HEX-SUPPORTS"
  Placement = pos=(162,60,35) rot=(0,0,1;0rad)
  Refine = true
  Shapes = -> [Cylinder129,Cylinder130,Cylinder131,Cylinder132]
FEATURE [Part::Cylinder] Cylinder133  label="Cylinder303"
  Angle = 360
  AttacherType = Attacher::AttachEngine3D
  Height = 3.8
  Placement = pos=(-19.5,25,121.5) rot=(1,0,0;1.5708rad)
  Radius = 2.5
FEATURE [Part::Cylinder] Cylinder134  label="Cylinder304"
  Angle = 360
  AttacherType = Attacher::AttachEngine3D
  Height = 3.8
  Placement = pos=(5,25,4) rot=(1,0,0;1.5708rad)
  Radius = 2.5
FEATURE [Part::Cylinder] Cylinder135  label="Cylinder305"
  Angle = 360
  AttacherType = Attacher::AttachEngine3D
  Height = 3.8
  Placement = pos=(22,25,4) rot=(1,0,0;1.5708rad)
  Radius = 2.5
FEATURE [Part::Cylinder] Cylinder136  label="Cylinder306"
  Angle = 360
  AttacherType = Attacher::AttachEngine3D
  Height = 3.8
  Placement = pos=(-4,25,63) rot=(1,0,0;1.5708rad)
  Radius = 2.5
FEATURE [Part::MultiFuse] Fusion082  label="crane-main-arm-ROUND-SUPPORTS"
  Placement = pos=(162,60,35) rot=(0,0,1;0rad)
  Refine = true
  Shapes = -> [Cylinder136,Cylinder133,Cylinder134,Cylinder135]
FEATURE [Part::Cylinder] Cylinder137  label="Cylinder307"
  Angle = 360
  AttacherType = Attacher::AttachEngine3D
  Height = 3.8
  Placement = pos=(5,25,136) rot=(1,0,0;1.5708rad)
  Radius = 2.5
FEATURE [Part::Cylinder] Cylinder138  label="Cylinder308"
  Angle = 360
  AttacherType = Attacher::AttachEngine3D
  Height = 3.8
  Placement = pos=(57,25,142) rot=(1,0,0;1.5708rad)
  Radius = 2.5
FEATURE [Part::Cylinder] Cylinder139  label="Cylinder309"
  Angle = 360
  AttacherType = Attacher::AttachEngine3D
  Height = 3.8
  Placement = pos=(105,25,141) rot=(1,0,0;1.5708rad)
  Radius = 2.5
FEATURE [Part::Cylinder] Cylinder140  label="Cylinder310"
  Angle = 360
  AttacherType = Attacher::AttachEngine3D
  Height = 3.8
  Placement = pos=(150,25,141) rot=(1,0,0;1.5708rad)
  Radius = 2.5
FEATURE [Part::MultiFuse] Fusion083  label="crane-secondary-arm-ROUND-SUPPORTS"
  Placement = pos=(162,60,35) rot=(0,0,1;0rad)
  Refine = true
  Shapes = -> [Cylinder137,Cylinder138,Cylinder139,Cylinder140]
FEATURE [Part::Cylinder] Cylinder141  label="Cylinder311"
  Angle = 360
  AttacherType = Attacher::AttachEngine3D
  Height = 29
  Placement = pos=(-3,27,133) rot=(1,0,0;1.5708rad)
  Radius = 1.25
FEATURE [Part::Cylinder] Cylinder142  label="Cylinder312"
  Angle = 360
  AttacherType = Attacher::AttachEngine3D
  Height = 29
  Placement = pos=(11,27,142) rot=(1,0,0;1.5708rad)
  Radius = 1.25
FEATURE [Part::MultiFuse] Fusion084
  Refine = true
  Shapes = -> [Cylinder142,Cylinder141,Cylinder066,Cylinder071,Cylinder086,Cylinder111,Cylinder112]
FEATURE [Part::Cut] Cut059
  Base = -> Cut054
  Refine = true
  Tool = -> Fusion084
FEATURE [Part::Cut] Cut060  label="crane-secondary-arm"
  Base = -> Cut059
  Placement = pos=(162,60,35) rot=(0,0,1;0rad)
  Refine = true
  Tool = -> Fusion079
FEATURE [Part::Cylinder] Cylinder143  label="Cylinder313"
  Angle = 360
  AttacherType = Attacher::AttachEngine3D
  Height = 17
  Placement = pos=(184,47,128) rot=(1,0,0;1.5708rad)
  Radius = 0.8
FEATURE [Part::Chamfer] Chamfer004
  Base = -> Box027
  Edges = 1 edges: [Edge2 r1=14.5 r2=28.99]
FEATURE [Part::Cut] Cut061  label="Cut060"
  Base = -> Chamfer004
  Placement = pos=(2,0,10) rot=(0,0,1;0rad)
  Refine = true
  Tool = -> Box028
FEATURE [Part::Cylinder] Cylinder144  label="Cylinder314"
  Angle = 360
  AttacherType = Attacher::AttachEngine3D
  Height = 1.6
  Placement = pos=(184,47,128) rot=(1,0,0;1.5708rad)
  Radius = 2.1
FEATURE [Part::RegularPolygon] RegularPolygon  label="Regular polygon"
  AttacherType = Attacher::AttachEngine3D
  Circumradius = 2.5
  Placement = pos=(0,0,-13) rot=(0,0,1;0rad)
  Polygon = 6
FEATURE [Part::Feature] Face017
  Placement = pos=(0,0,0) rot=(0,0,1;0.523599rad)
  shape: bbox 4.777 x 5.508 x 2e-07 mm, 1 faces, 0 solids (baked)
FEATURE [Part::Extrusion] Extrude017
  Base = -> Face017
  Dir = (0,0,1.6)
  DirMode = 0
  FaceMakerClass = Part::FaceMakerExtrusion
  LengthFwd = 0
  LengthRev = 0
  Placement = pos=(184,18.6,128) rot=(1,0,0;1.5708rad)
  Solid = true
  Symmetric = false
FEATURE [Part::MultiFuse] Fusion085
  Placement = pos=(0,0,18) rot=(0,0,1;0rad)
  Refine = true
  Shapes = -> [Cylinder143,Cylinder144,Extrude017]
FEATURE [Part::Cylinder] Cylinder145  label="Cylinder315"
  Angle = 360
  AttacherType = Attacher::AttachEngine3D
  Height = 17
  Placement = pos=(184,47,128) rot=(1,0,0;1.5708rad)
  Radius = 0.8
FEATURE [Part::Cylinder] Cylinder146  label="Cylinder316"
  Angle = 360
  AttacherType = Attacher::AttachEngine3D
  Height = 1.6
  Placement = pos=(184,47,128) rot=(1,0,0;1.5708rad)
  Radius = 2.1
FEATURE [Part::Feature] Face018
  Placement = pos=(0,0,0) rot=(0,0,1;0.523599rad)
  shape: bbox 4.777 x 5.508 x 2e-07 mm, 1 faces, 0 solids (baked)
FEATURE [Part::Extrusion] Extrude018
  Base = -> Face018
  Dir = (0,0,1.6)
  DirMode = 0
  FaceMakerClass = Part::FaceMakerExtrusion
  LengthFwd = 0
  LengthRev = 0
  Placement = pos=(184,18.6,128) rot=(1,0,0;1.5708rad)
  Solid = true
  Symmetric = false
FEATURE [Part::MultiFuse] Fusion086
  Placement = pos=(0,0,-173) rot=(0,0,1;0rad)
  Refine = true
  Shapes = -> [Cylinder145,Cylinder146,Extrude018]
FEATURE [Part::Cylinder] Cylinder147  label="Cylinder317"
  Angle = 360
  AttacherType = Attacher::AttachEngine3D
  Height = 17
  Placement = pos=(184,47,128) rot=(1,0,0;1.5708rad)
  Radius = 0.8
FEATURE [Part::Cylinder] Cylinder148  label="Cylinder318"
  Angle = 360
  AttacherType = Attacher::AttachEngine3D
  Height = 1.6
  Placement = pos=(184,47,128) rot=(1,0,0;1.5708rad)
  Radius = 2.1
FEATURE [Part::Feature] Face019
  Placement = pos=(0,0,0) rot=(0,0,1;0.523599rad)
  shape: bbox 4.777 x 5.508 x 2e-07 mm, 1 faces, 0 solids (baked)
FEATURE [Part::Extrusion] Extrude019
  Base = -> Face019
  Dir = (0,0,1.6)
  DirMode = 0
  FaceMakerClass = Part::FaceMakerExtrusion
  LengthFwd = 0
  LengthRev = 0
  Placement = pos=(184,18.6,128) rot=(1,0,0;1.5708rad)
  Solid = true
  Symmetric = false
FEATURE [Part::MultiFuse] Fusion087
  Placement = pos=(0,0,-77) rot=(0,0,1;0rad)
  Refine = true
  Shapes = -> [Cylinder147,Cylinder148,Extrude019]
FEATURE [Part::Cylinder] Cylinder149  label="Cylinder319"
  Angle = 360
  AttacherType = Attacher::AttachEngine3D
  Height = 17
  Placement = pos=(184,47,128) rot=(1,0,0;1.5708rad)
  Radius = 0.8
FEATURE [Part::Cylinder] Cylinder150  label="Cylinder320"
  Angle = 360
  AttacherType = Attacher::AttachEngine3D
  Height = 1.6
  Placement = pos=(184,47,128) rot=(1,0,0;1.5708rad)
  Radius = 2.1
FEATURE [Part::Feature] Face020
  Placement = pos=(0,0,0) rot=(0,0,1;0.523599rad)
  shape: bbox 4.777 x 5.508 x 2e-07 mm, 1 faces, 0 solids (baked)
FEATURE [Part::Extrusion] Extrude020
  Base = -> Face020
  Dir = (0,0,1.6)
  DirMode = 0
  FaceMakerClass = Part::FaceMakerExtrusion
  LengthFwd = 0
  LengthRev = 0
  Placement = pos=(184,18.6,128) rot=(1,0,0;1.5708rad)
  Solid = true
  Symmetric = false
FEATURE [Part::MultiFuse] Fusion088
  Placement = pos=(0,0,-28) rot=(0,0,1;0rad)
  Refine = true
  Shapes = -> [Cylinder149,Cylinder150,Extrude020]
FEATURE [Part::Cylinder] Cylinder151  label="Cylinder321"
  Angle = 360
  AttacherType = Attacher::AttachEngine3D
  Height = 17
  Placement = pos=(184,47,128) rot=(1,0,0;1.5708rad)
  Radius = 0.8
FEATURE [Part::Cylinder] Cylinder152  label="Cylinder322"
  Angle = 360
  AttacherType = Attacher::AttachEngine3D
  Height = 1.6
  Placement = pos=(184,47,128) rot=(1,0,0;1.5708rad)
  Radius = 2.1
FEATURE [Part::Feature] Face021
  Placement = pos=(0,0,0) rot=(0,0,1;0.523599rad)
  shape: bbox 4.777 x 5.508 x 2e-07 mm, 1 faces, 0 solids (baked)
FEATURE [Part::Extrusion] Extrude021
  Base = -> Face021
  Dir = (0,0,1.6)
  DirMode = 0
  FaceMakerClass = Part::FaceMakerExtrusion
  LengthFwd = 0
  LengthRev = 0
  Placement = pos=(184,18.6,128) rot=(1,0,0;1.5708rad)
  Solid = true
  Symmetric = false
FEATURE [Part::MultiFuse] Fusion089
  Placement = pos=(0,0,-125) rot=(0,0,1;0rad)
  Refine = true
  Shapes = -> [Cylinder151,Cylinder152,Extrude021]
FEATURE [Part::Cylinder] Cylinder153  label="Cylinder323"
  Angle = 360
  AttacherType = Attacher::AttachEngine3D
  Height = 17
  Placement = pos=(184,47,128) rot=(1,0,0;1.5708rad)
  Radius = 0.8
FEATURE [Part::Cylinder] Cylinder154  label="Cylinder324"
  Angle = 360
  AttacherType = Attacher::AttachEngine3D
  Height = 1.6
  Placement = pos=(184,47,128) rot=(1,0,0;1.5708rad)
  Radius = 2.1
FEATURE [Part::Feature] Face022
  Placement = pos=(0,0,0) rot=(0,0,1;0.523599rad)
  shape: bbox 4.777 x 5.508 x 2e-07 mm, 1 faces, 0 solids (baked)
FEATURE [Part::Extrusion] Extrude022
  Base = -> Face022
  Dir = (0,0,1.6)
  DirMode = 0
  FaceMakerClass = Part::FaceMakerExtrusion
  LengthFwd = 0
  LengthRev = 0
  Placement = pos=(184,18.6,128) rot=(1,0,0;1.5708rad)
  Solid = true
  Symmetric = false
FEATURE [Part::MultiFuse] Fusion090
  Placement = pos=(-25,0,-173) rot=(0,0,1;0rad)
  Refine = true
  Shapes = -> [Cylinder153,Cylinder154,Extrude022]
FEATURE [Part::Cylinder] Cylinder155  label="Cylinder325"
  Angle = 360
  AttacherType = Attacher::AttachEngine3D
  Height = 17
  Placement = pos=(184,47,128) rot=(1,0,0;1.5708rad)
  Radius = 0.8
FEATURE [Part::Cylinder] Cylinder156  label="Cylinder326"
  Angle = 360
  AttacherType = Attacher::AttachEngine3D
  Height = 1.6
  Placement = pos=(184,47,128) rot=(1,0,0;1.5708rad)
  Radius = 2.1
FEATURE [Part::Feature] Face023
  Placement = pos=(0,0,0) rot=(0,0,1;0.523599rad)
  shape: bbox 4.777 x 5.508 x 2e-07 mm, 1 faces, 0 solids (baked)
FEATURE [Part::Extrusion] Extrude023
  Base = -> Face023
  Dir = (0,0,1.6)
  DirMode = 0
  FaceMakerClass = Part::FaceMakerExtrusion
  LengthFwd = 0
  LengthRev = 0
  Placement = pos=(184,18.6,128) rot=(1,0,0;1.5708rad)
  Solid = true
  Symmetric = false
FEATURE [Part::MultiFuse] Fusion091
  Placement = pos=(-25,0,-77) rot=(0,0,1;0rad)
  Refine = true
  Shapes = -> [Cylinder155,Cylinder156,Extrude023]
FEATURE [Part::Cylinder] Cylinder157  label="Cylinder327"
  Angle = 360
  AttacherType = Attacher::AttachEngine3D
  Height = 17
  Placement = pos=(184,47,128) rot=(1,0,0;1.5708rad)
  Radius = 0.8
FEATURE [Part::Cylinder] Cylinder158  label="Cylinder328"
  Angle = 360
  AttacherType = Attacher::AttachEngine3D
  Height = 1.6
  Placement = pos=(184,47,128) rot=(1,0,0;1.5708rad)
  Radius = 2.1
FEATURE [Part::Feature] Face024
  Placement = pos=(0,0,0) rot=(0,0,1;0.523599rad)
  shape: bbox 4.777 x 5.508 x 2e-07 mm, 1 faces, 0 solids (baked)
FEATURE [Part::Extrusion] Extrude024
  Base = -> Face024
  Dir = (0,0,1.6)
  DirMode = 0
  FaceMakerClass = Part::FaceMakerExtrusion
  LengthFwd = 0
  LengthRev = 0
  Placement = pos=(184,18.6,128) rot=(1,0,0;1.5708rad)
  Solid = true
  Symmetric = false
FEATURE [Part::MultiFuse] Fusion092
  Placement = pos=(-25,0,-39) rot=(0,0,1;0rad)
  Refine = true
  Shapes = -> [Cylinder157,Cylinder158,Extrude024]
FEATURE [Part::Cylinder] Cylinder159  label="Cylinder329"
  Angle = 360
  AttacherType = Attacher::AttachEngine3D
  Height = 17
  Placement = pos=(184,47,128) rot=(1,0,0;1.5708rad)
  Radius = 0.8
FEATURE [Part::Cylinder] Cylinder160  label="Cylinder330"
  Angle = 360
  AttacherType = Attacher::AttachEngine3D
  Height = 1.6
  Placement = pos=(184,47,128) rot=(1,0,0;1.5708rad)
  Radius = 2.1
FEATURE [Part::Feature] Face025
  Placement = pos=(0,0,0) rot=(0,0,1;0.523599rad)
  shape: bbox 4.777 x 5.508 x 2e-07 mm, 1 faces, 0 solids (baked)
FEATURE [Part::Extrusion] Extrude025
  Base = -> Face025
  Dir = (0,0,1.6)
  DirMode = 0
  FaceMakerClass = Part::FaceMakerExtrusion
  LengthFwd = 0
  LengthRev = 0
  Placement = pos=(184,18.6,128) rot=(1,0,0;1.5708rad)
  Solid = true
  Symmetric = false
FEATURE [Part::MultiFuse] Fusion093
  Placement = pos=(-25,0,-125) rot=(0,0,1;0rad)
  Refine = true
  Shapes = -> [Cylinder159,Cylinder160,Extrude025]
FEATURE [Part::Cylinder] Cylinder161  label="Cylinder331"
  Angle = 360
  AttacherType = Attacher::AttachEngine3D
  Height = 17
  Placement = pos=(184,47,128) rot=(1,0,0;1.5708rad)
  Radius = 0.8
FEATURE [Part::Cylinder] Cylinder162  label="Cylinder332"
  Angle = 360
  AttacherType = Attacher::AttachEngine3D
  Height = 1.6
  Placement = pos=(184,47,128) rot=(1,0,0;1.5708rad)
  Radius = 2.1
FEATURE [Part::Feature] Face026
  Placement = pos=(0,0,0) rot=(0,0,1;0.523599rad)
  shape: bbox 4.777 x 5.508 x 2e-07 mm, 1 faces, 0 solids (baked)
FEATURE [Part::Extrusion] Extrude026
  Base = -> Face026
  Dir = (0,0,1.6)
  DirMode = 0
  FaceMakerClass = Part::FaceMakerExtrusion
  LengthFwd = 0
  LengthRev = 0
  Placement = pos=(184,18.6,128) rot=(1,0,0;1.5708rad)
  Solid = true
  Symmetric = false
FEATURE [Part::MultiFuse] Fusion094
  Placement = pos=(-25,0,6) rot=(0,0,1;0rad)
  Refine = true
  Shapes = -> [Cylinder161,Cylinder162,Extrude026]
FEATURE [Part::MultiFuse] Fusion095
  Refine = true
  Shapes = -> [Fusion085,Fusion086,Fusion087,Fusion088,Fusion089,Fusion090,Fusion091,Fusion092,Fusion093,Fusion094]
FEATURE [Part::Cut] Cut062
  Base = -> Cut061
  Refine = true
  Tool = -> Fusion095
FEATURE [Part::Cylinder] Cylinder163  label="Cylinder333"
  Angle = 360
  AttacherType = Attacher::AttachEngine3D
  Height = 5
  Placement = pos=(159,30,104) rot=(1,0,0;1.5708rad)
  Radius = 7
FEATURE [Part::Cylinder] Cylinder164  label="Cylinder334"
  Angle = 360
  AttacherType = Attacher::AttachEngine3D
  Height = 3
  Placement = pos=(159,30,104) rot=(1,0,0;1.5708rad)
  Radius = 1.25
FEATURE [Part::Cut] Cut012
  Base = -> Fillet010
  Placement = pos=(292,0,-39.5) rot=(0,-1,0;1.5708rad)
  Refine = true
  Tool = -> Fusion003
FEATURE [Part::Cut] Cut011
  Base = -> Fillet009
  Placement = pos=(292,0,-39.5) rot=(0,-1,0;1.5708rad)
  Refine = true
  Tool = -> Fusion002
FEATURE [Part::Cylinder] Cylinder175  label="extender-arm-cylinder-piston-rod"
  Angle = 360
  AttacherType = Attacher::AttachEngine3D
  Height = 101
  Placement = pos=(408,98.5,189.5) rot=(0,1,0;1.5708rad)
  Radius = 3
FEATURE [Part::Cylinder] Cylinder176  label="Cylinder335"
  Angle = 360
  AttacherType = Attacher::AttachEngine3D
  Height = 20
  Placement = pos=(194,50.5,143) rot=(1,0,0;1.5708rad)
  Radius = 1.6
FEATURE [Part::Cylinder] Cylinder177  label="Cylinder336"
  Angle = 360
  AttacherType = Attacher::AttachEngine3D
  Height = 5
  Placement = pos=(159,8,104) rot=(1,0,0;1.5708rad)
  Radius = 7
FEATURE [Part::MultiFuse] Fusion103
  Refine = true
  Shapes = -> [Cut011,Cylinder177]
FEATURE [Part::MultiFuse] Fusion104
  Refine = true
  Shapes = -> [Cut012,Cylinder163]
FEATURE [Part::Fillet] Fillet026
  Base = -> Fusion103
  Edges = 2 edges r=2.499: [Edge12,Edge28]
FEATURE [Part::Fillet] Fillet027
  Base = -> Fusion104
  Edges = 2 edges r=2.499: [Edge12,Edge28]
FEATURE [Part::Cylinder] Cylinder178  label="Cylinder337"
  Angle = 360
  AttacherType = Attacher::AttachEngine3D
  Height = 5
  Placement = pos=(159,8,104) rot=(1,0,0;1.5708rad)
  Radius = 3.1
FEATURE [Part::Cut] Cut072  label="crane-extender-arm-outer-plate"
  Base = -> Fillet026
  Placement = pos=(454.5,60,-4.5) rot=(0,-1,0;1.5708rad)
  Refine = true
  Tool = -> Cylinder178
FEATURE [Part::Cylinder] Cylinder180  label="Cylinder338"
  Angle = 360
  AttacherType = Attacher::AttachEngine3D
  Height = 3
  Placement = pos=(166,30,126.5) rot=(1,0,0;1.5708rad)
  Radius = 1.25
FEATURE [Part::Cylinder] Cylinder181  label="Cylinder339"
  Angle = 360
  AttacherType = Attacher::AttachEngine3D
  Height = 3
  Placement = pos=(166,30,96.5) rot=(1,0,0;1.5708rad)
  Radius = 1.25
FEATURE [Part::Cylinder] Cylinder182  label="Cylinder340"
  Angle = 360
  AttacherType = Attacher::AttachEngine3D
  Height = 3
  Placement = pos=(177,30,126.5) rot=(1,0,0;1.5708rad)
  Radius = 1.25
FEATURE [Part::MultiFuse] Fusion105
  Placement = pos=(0,2.8,0) rot=(0,0,1;0rad)
  Refine = true
  Shapes = -> [Cylinder164,Cylinder180,Cylinder181,Cylinder182]
FEATURE [Part::Cylinder] Cylinder183  label="Cylinder341"
  Angle = 360
  AttacherType = Attacher::AttachEngine3D
  Height = 5
  Placement = pos=(159,30,104) rot=(1,0,0;1.5708rad)
  Radius = 1.25
FEATURE [Part::Cut] Cut073  label="crane-extender-arm-inner-plate"
  Base = -> Fillet027
  Placement = pos=(454.5,60,-4.5) rot=(0,-1,0;1.5708rad)
  Refine = true
  Tool = -> Cylinder183
FEATURE [Part::Box] Box055  label="Cube053"
  AttacherType = Attacher::AttachEngine3D
  Height = 13
  Length = 15
  Placement = pos=(186,33,138) rot=(0,0,1;0rad)
  Width = 11
FEATURE [Part::Box] Box056  label="Cube054"
  AttacherType = Attacher::AttachEngine3D
  Height = 10.5
  Length = 15
  Placement = pos=(186,35,138) rot=(0,0,1;0rad)
  Width = 7
FEATURE [Part::Chamfer] Chamfer005
  Base = -> Box055
  Edges = 1 edges r=5: [Edge6]
FEATURE [Part::Cut] Cut075
  Base = -> Chamfer005
  Refine = true
  Tool = -> Box056
FEATURE [Part::Fillet] Fillet028
  Base = -> Cut075
  Edges = 5 edges r=4: [Edge1,Edge3,Edge6,Edge8,Edge24]
FEATURE [Part::Cut] Cut076
  Base = -> Fillet028
  Refine = true
  Tool = -> Cylinder176
FEATURE [Part::MultiFuse] Fusion106
  Refine = true
  Shapes = -> [Cut062,Cut076]
FEATURE [Part::Cylinder] Cylinder186  label="Cylinder343"
  Angle = 360
  AttacherType = Attacher::AttachEngine3D
  Height = 10
  Placement = pos=(159,47,128) rot=(1,0,0;1.5708rad)
  Radius = 0.8
FEATURE [Part::Cylinder] Cylinder187  label="Cylinder344"
  Angle = 360
  AttacherType = Attacher::AttachEngine3D
  Height = 10
  Placement = pos=(184,47,128) rot=(1,0,0;1.5708rad)
  Radius = 0.8
FEATURE [Part::MultiFuse] Fusion107
  Placement = pos=(0,0,-52) rot=(0,0,1;0rad)
  Refine = true
  Shapes = -> [Cylinder187,Cylinder186]
FEATURE [Part::Cylinder] Cylinder188  label="Cylinder345"
  Angle = 360
  AttacherType = Attacher::AttachEngine3D
  Height = 10
  Placement = pos=(159,47,128) rot=(1,0,0;1.5708rad)
  Radius = 0.8
FEATURE [Part::Cylinder] Cylinder189  label="Cylinder346"
  Angle = 360
  AttacherType = Attacher::AttachEngine3D
  Height = 10
  Placement = pos=(184,47,128) rot=(1,0,0;1.5708rad)
  Radius = 0.8
FEATURE [Part::MultiFuse] Fusion108
  Refine = true
  Shapes = -> [Cylinder189,Cylinder188]
FEATURE [Part::Cylinder] Cylinder190  label="Cylinder347"
  Angle = 360
  AttacherType = Attacher::AttachEngine3D
  Height = 10
  Placement = pos=(159,47,128) rot=(1,0,0;1.5708rad)
  Radius = 0.8
FEATURE [Part::Cylinder] Cylinder191  label="Cylinder348"
  Angle = 360
  AttacherType = Attacher::AttachEngine3D
  Height = 10
  Placement = pos=(184,47,128) rot=(1,0,0;1.5708rad)
  Radius = 0.8
FEATURE [Part::MultiFuse] Fusion109
  Placement = pos=(0,0,-101) rot=(0,0,1;0rad)
  Refine = true
  Shapes = -> [Cylinder191,Cylinder190]
FEATURE [Part::Cylinder] Cylinder192  label="Cylinder349"
  Angle = 360
  AttacherType = Attacher::AttachEngine3D
  Height = 10
  Placement = pos=(159,47,128) rot=(1,0,0;1.5708rad)
  Radius = 0.8
FEATURE [Part::Cylinder] Cylinder193  label="Cylinder350"
  Angle = 360
  AttacherType = Attacher::AttachEngine3D
  Height = 10
  Placement = pos=(184,47,128) rot=(1,0,0;1.5708rad)
  Radius = 0.8
FEATURE [Part::MultiFuse] Fusion110
  Placement = pos=(0,0,-150) rot=(0,0,1;0rad)
  Refine = true
  Shapes = -> [Cylinder193,Cylinder192]
FEATURE [Part::MultiFuse] Fusion111
  Refine = true
  Shapes = -> [Fusion107,Fusion108,Fusion110,Fusion109]
FEATURE [Part::Cut] Cut077
  Base = -> Fusion106
  Refine = true
  Tool = -> Fusion105
FEATURE [Part::Cut] Cut078  label="crane-extender-arm"
  Base = -> Cut077
  Placement = pos=(454.5,60,-4.5) rot=(0,-1,0;1.5708rad)
  Refine = true
  Tool = -> Fusion111
FEATURE [Part::MultiFuse] Fusion114
  Refine = true
  Shapes = -> [Cylinder001,Cylinder002]
FEATURE [Part::MultiFuse] Fusion116
  Refine = true
  Shapes = -> [Cylinder013,Cylinder082,Cylinder083,Cylinder085,Cylinder084]
FEATURE [Part::MultiFuse] Fusion120
  Refine = true
  Shapes = -> [Cylinder029,Cylinder028,Cylinder,Cylinder020]
FEATURE [Part::MultiFuse] Fusion122
  Refine = true
  Shapes = -> [Fusion054,Fusion055,Fusion057,Fusion056]
FEATURE [Part::MultiFuse] Fusion
  Refine = true
  Shapes = -> [Box017,Box001]
FEATURE [Part::Cut] Cut
  Base = -> Fusion
  Refine = true
  Tool = -> Fillet
FEATURE [Part::Cut] Cut079
  Base = -> Cut
  Refine = true
  Tool = -> Box003
FEATURE [Part::MultiFuse] Fusion123
  Refine = true
  Shapes = -> [Box030,Box007]
FEATURE [Part::MultiFuse] Fusion124
  Refine = true
  Shapes = -> [Cut079,Fusion123]
FEATURE [Part::Chamfer] Chamfer006
  Base = -> Fusion124
  Edges = 2 edges r=6: [Edge25,Edge34]
FEATURE [Part::Fillet] Fillet029
  Base = -> Chamfer006
  Edges = 2 edges r=14: [Edge22,Edge27]
FEATURE [Part::Fillet] Fillet030
  Base = -> Fillet029
  Edges = 3 edges r=5: [Edge27,Edge30,Edge32]
FEATURE [Part::MultiFuse] Fusion125
  Refine = true
  Shapes = -> [Fillet030,Fusion120]
FEATURE [Part::Cut] Cut080
  Base = -> Fusion125
  Refine = true
  Tool = -> Fusion116
FEATURE [Part::Cut] Cut081
  Base = -> Cut080
  Refine = true
  Tool = -> Fusion122
FEATURE [Part::Cut] Cut082
  Base = -> Cut081
  Refine = true
  Tool = -> Fusion114
FEATURE [Part::Cut] Cut083
  Base = -> Cut082
  Refine = true
  Tool = -> Box039
FEATURE [Part::Cut] Cut084
  Base = -> Cut083
  Refine = true
  Tool = -> Fusion075
FEATURE [Part::Cut] Cut085  label="crane-main-arm"
  Base = -> Cut084
  Placement = pos=(162,60,35) rot=(0,0,1;0rad)
  Refine = true
  Tool = -> Fillet024
FEATURE [Part::Box] Box416  label="Cube641"
  AttacherType = Attacher::AttachEngine3D
  Height = 20
  Length = 480
  Placement = pos=(0,0,-92) rot=(0,0,1;0rad)
  Width = 11.5
FEATURE [Part::Box] Box417  label="Cube642"
  AttacherType = Attacher::AttachEngine3D
  Height = 17
  Length = 480
  Placement = pos=(0,1.5,-90.5) rot=(0,0,1;0rad)
  Width = 10
FEATURE [Part::Cut] Cut429  label="Cut769"
  Base = -> Box416
  Refine = true
  Tool = -> Box417
FEATURE [Part::Fillet] Fillet268
  Base = -> Cut429
  Edges = 2 edges r=3: [Edge11,Edge23]
  Placement = pos=(0,-1.5,0) rot=(0,0,1;0rad)
FEATURE [Part::Box] Box418  label="Cube643"
  AttacherType = Attacher::AttachEngine3D
  Height = 20
  Length = 480
  Placement = pos=(0,0,-92) rot=(0,0,1;0rad)
  Width = 11.5
FEATURE [Part::Box] Box419  label="Cube644"
  AttacherType = Attacher::AttachEngine3D
  Height = 17
  Length = 480
  Placement = pos=(0,1.5,-90.5) rot=(0,0,1;0rad)
  Width = 10
FEATURE [Part::Cut] Cut430  label="Cut770"
  Base = -> Box418
  Refine = true
  Tool = -> Box419
FEATURE [Part::Fillet] Fillet269
  Base = -> Cut430
  Edges = 2 edges r=3: [Edge11,Edge23]
FEATURE [Part::Mirroring] Part__Mirroring036  label="Fillet269 (Mirror #29)"
  Base = (0,0,0)
  Normal = (0,1,0)
  Placement = pos=(0,61.5,0) rot=(0,0,1;0rad)
  Source = -> Fillet269
FEATURE [Part::MultiFuse] Fusion231  label="frame-00"
  Placement = pos=(23.5,55,74) rot=(0,0,1;0rad)
  Refine = true
  Shapes = -> [Part__Mirroring036,Fillet268]
FEATURE [Part::Feature] Fusion654001  label="fuel-tank"
  Placement = pos=(5,0,0) rot=(0,0,1;0rad)
  shape: bbox 80 x 58.5 x 58 mm, 222 faces, 2 solids (baked)
FEATURE [Part::Chamfer] Chamfer108  label="air-box-holder"
  Edges = 1 edges r=1.49: [Edge70]
FEATURE [Part::Feature] Fusion248002050001  label="battery-box-air-tanks"
  Placement = pos=(5,0,0) rot=(0,0,1;0rad)
  shape: bbox 56 x 53.71 x 46.5 mm, 136 faces, 4 solids (baked)
FEATURE [Part::Cut] Cut397  label="cab-upper-part-02"
  Placement = pos=(0,0,3) rot=(0,0,1;0rad)
  Refine = true
FEATURE [Part::Cut] Cut398  label="cab-lower-part-05"
  Placement = pos=(0,0,3) rot=(0,0,1;0rad)
  Refine = true
FEATURE [Part::Cylinder] Cylinder198  label="Cylinder355"
  Angle = 360
  AttacherType = Attacher::AttachEngine3D
  Height = 50
  Placement = pos=(175,72.5,25) rot=(0,0,1;0rad)
  Radius = 2.5
FEATURE [Part::Box] Box422  label="Cube647"
  AttacherType = Attacher::AttachEngine3D
  Height = 30
  Length = 35.5
  Placement = pos=(155.75,59.75,30) rot=(0,0,1;0rad)
  Width = 25.5
FEATURE [Part::Box] Box423  label="Cube648"
  AttacherType = Attacher::AttachEngine3D
  Height = 125
  Length = 30
  Placement = pos=(155.75,59.75,33) rot=(0,-1,0;0.20944rad)
  Width = 25.5
FEATURE [Part::Box] Box424  label="Cube649"
  AttacherType = Attacher::AttachEngine3D
  Height = 30
  Length = 25.5
  Placement = pos=(155.75,59.75,28) rot=(0,0,1;0rad)
  Width = 25.5
FEATURE [Part::MultiFuse] Fusion248002050004
  Refine = true
  Shapes = -> [Box422,Box424,Box423]
FEATURE [Part::Fillet] Fillet270
  Base = -> Fusion248002050004
  Edges = 1 edges r=5.25: [Edge16]
  Placement = pos=(-5,0,2.75) rot=(0,0,1;0rad)
FEATURE [Part::Cylinder] Cylinder199  label="Cylinder356"
  Angle = 360
  AttacherType = Attacher::AttachEngine3D
  Height = 12
  Placement = pos=(13,12.5,-3) rot=(0,0,1;0rad)
  Radius = 2.5
FEATURE [Part::Cylinder] Cylinder200  label="Cylinder357"
  Angle = 360
  AttacherType = Attacher::AttachEngine3D
  Height = 11
  Placement = pos=(9,18,-2) rot=(0,0,1;0rad)
  Radius = 1.25
FEATURE [Part::Cylinder] Cylinder201  label="Cylinder358"
  Angle = 360
  AttacherType = Attacher::AttachEngine3D
  Height = 11
  Placement = pos=(9,7,-2) rot=(0,0,1;0rad)
  Radius = 1.25
FEATURE [Part::Cylinder] Cylinder202  label="Cylinder359"
  Angle = 360
  AttacherType = Attacher::AttachEngine3D
  Height = 11
  Placement = pos=(18,18,-2) rot=(0,0,1;0rad)
  Radius = 1.25
FEATURE [Part::Cylinder] Cylinder203  label="Cylinder360"
  Angle = 360
  AttacherType = Attacher::AttachEngine3D
  Height = 11
  Placement = pos=(18,7,-2) rot=(0,0,1;0rad)
  Radius = 1.25
FEATURE [Part::MultiFuse] Fusion248002050005
  Placement = pos=(150,60,25) rot=(0,0,1;0rad)
  Refine = true
  Shapes = -> [Cylinder199,Cylinder200,Cylinder201,Cylinder203,Cylinder202]
FEATURE [Part::Cylinder] Cylinder206  label="Cylinder361"
  Angle = 360
  AttacherType = Attacher::AttachEngine3D
  Height = 2.5
  Placement = pos=(9,18,-2) rot=(0,0,1;0rad)
  Radius = 3
FEATURE [Part::Cylinder] Cylinder207  label="Cylinder362"
  Angle = 360
  AttacherType = Attacher::AttachEngine3D
  Height = 2.5
  Placement = pos=(9,7,-2) rot=(0,0,1;0rad)
  Radius = 3
FEATURE [Part::Cylinder] Cylinder208  label="Cylinder363"
  Angle = 360
  AttacherType = Attacher::AttachEngine3D
  Height = 2.5
  Placement = pos=(18,18,-2) rot=(0,0,1;0rad)
  Radius = 3
FEATURE [Part::Cylinder] Cylinder209  label="Cylinder364"
  Angle = 360
  AttacherType = Attacher::AttachEngine3D
  Height = 2.5
  Placement = pos=(18,7,-2) rot=(0,0,1;0rad)
  Radius = 3
FEATURE [Part::FeaturePython] RefineLinearExtrude  # WARN: FeaturePython — macro-defined, semantics opaque (R4)
FEATURE [Part::Extrusion] LinearExtrude
  Base = -> RefineLinearExtrude
  Dir = (0,0,6)
  DirMode = 0
  FaceMakerClass = Part::FaceMakerExtrusion
  LengthFwd = 0
  LengthRev = 0
  Placement = pos=(121,29,26.5) rot=(0,0,1;0rad)
  Solid = true
  Symmetric = false
FEATURE [Part::FeaturePython] RefineLinearExtrude005  # WARN: FeaturePython — macro-defined, semantics opaque (R4)
FEATURE [Part::Extrusion] LinearExtrude005
  Base = -> RefineLinearExtrude005
  Dir = (0,0,8)
  DirMode = 0
  FaceMakerClass = Part::FaceMakerExtrusion
  LengthFwd = 0
  LengthRev = 0
  Solid = true
  Symmetric = false
FEATURE [Part::FeaturePython] RefineLinearExtrude006  # WARN: FeaturePython — macro-defined, semantics opaque (R4)
FEATURE [Part::Extrusion] LinearExtrude006
  Base = -> RefineLinearExtrude006
  Dir = (0,0,10)
  DirMode = 0
  FaceMakerClass = Part::FaceMakerExtrusion
  LengthFwd = 0
  LengthRev = 0
  Placement = pos=(0,0,-1) rot=(0,0,1;0rad)
  Solid = true
  Symmetric = false
FEATURE [Part::Cut] difference
  Base = -> LinearExtrude005
  Placement = pos=(163,72.5,26.5) rot=(0,0,1;0rad)
  Refine = true
  Tool = -> LinearExtrude006
FEATURE [Part::Cut] Cut433
  Base = -> difference
  Refine = true
  Tool = -> Fillet270
FEATURE [Part::MultiFuse] Fusion248002050006
  Placement = pos=(150,60,28.5) rot=(0,0,1;0rad)
  Refine = true
  Shapes = -> [Cylinder206,Cylinder207,Cylinder208,Cylinder209]
FEATURE [Part::MultiFuse] Fusion248002050007
  Refine = true
  Shapes = -> [Fusion248002050005,Fusion248002050006]
FEATURE [Part::Cut] Cut434
  Base = -> Cut433
  Refine = true
  Tool = -> Fusion248002050007
FEATURE [Part::Chamfer] Chamfer109  label="crane-rotating-gear"
  Base = -> Cut434
  Edges = 4 edges r=0.4: [Edge480,Edge481,Edge482,Edge484]
  Placement = pos=(12,0,2) rot=(0,0,1;0rad)
FEATURE [Part::Box] Box425  label="Cube650"
  AttacherType = Attacher::AttachEngine3D
  Height = 6
  Length = 1
  Placement = pos=(141.5,31,26.5) rot=(0,0,1;0rad)
  Width = 76
FEATURE [Part::Box] Box426  label="Cube651"
  AttacherType = Attacher::AttachEngine3D
  Height = 6
  Length = 5
  Placement = pos=(141.5,107,26.5) rot=(0,0,1;0rad)
  Width = 8
FEATURE [Part::Cut] Cut435
  Base = -> LinearExtrude
  Refine = true
  Tool = -> Box426
FEATURE [Part::MultiFuse] Fusion248002050008
  Placement = pos=(12,0,2) rot=(0,0,1;0rad)
  Refine = true
  Shapes = -> [Cut435,Box425]
FEATURE [Part::Cylinder] Cylinder210  label="Cylinder365"
  Angle = 360
  AttacherType = Attacher::AttachEngine3D
  Height = 20
  Placement = pos=(175,72.5,44) rot=(0,0,1;0rad)
  Radius = 9
FEATURE [Part::Cylinder] Cylinder211  label="cylinder-jacket003"
  Angle = 360
  AttacherType = Attacher::AttachEngine3D
  Height = 150
  Placement = pos=(1,0,56) rot=(0,0,1;0rad)
  Radius = 6
FEATURE [Part::Cylinder] Cylinder212  label="cylinder-jacket004"
  Angle = 360
  AttacherType = Attacher::AttachEngine3D
  Height = 150
  Placement = pos=(1,0,56) rot=(0,0,1;0rad)
  Radius = 5
FEATURE [Part::Cut] Cut436  label="extender-cylinder-jacket"
  Base = -> Cylinder211
  Placement = pos=(294.5,98.5,190.5) rot=(0,1,0;1.5708rad)
  Refine = true
  Tool = -> Cylinder212
FEATURE [Part::Cylinder] Cylinder213  label="Cylinder366"
  Angle = 360
  AttacherType = Attacher::AttachEngine3D
  Height = 6
  Placement = pos=(483.5,98.5,187.5) rot=(0,1,0;1.5708rad)
  Radius = 3.1
FEATURE [Part::Cylinder] Cylinder214  label="Cylinder367"
  Angle = 360
  AttacherType = Attacher::AttachEngine3D
  Height = 3
  Placement = pos=(483.5,98.5,187.5) rot=(0,1,0;1.5708rad)
  Radius = 4.9
FEATURE [Part::Cylinder] Cylinder215  label="Cylinder368"
  Angle = 360
  AttacherType = Attacher::AttachEngine3D
  Height = 3
  Placement = pos=(486.5,98.5,187.5) rot=(0,1,0;1.5708rad)
  Radius = 6
FEATURE [Part::MultiFuse] Fusion248002050009
  Refine = true
  Shapes = -> [Cylinder215,Cylinder214]
FEATURE [Part::Cut] Cut437
  Base = -> Fusion248002050009
  Placement = pos=(2,0,0) rot=(0,0,1;0rad)
  Refine = true
  Tool = -> Cylinder213
FEATURE [Part::Box] Box427  label="Cube652"
  AttacherType = Attacher::AttachEngine3D
  Height = 15
  Length = 39
  Placement = pos=(306.5,91,180) rot=(0,0,1;0rad)
  Width = 15
FEATURE [Part::Cylinder] Cylinder216  label="Cylinder369"
  Angle = 360
  AttacherType = Attacher::AttachEngine3D
  Height = 27
  Radius = 8
FEATURE [Part::Box] Box428  label="Cube653"
  AttacherType = Attacher::AttachEngine3D
  Height = 27
  Length = 10.4
  Placement = pos=(-5.2,-6.2,0) rot=(0,0,1;0rad)
  Width = 12.4
FEATURE [Part::Cylinder] Cylinder217  label="Cylinder370"
  Angle = 360
  AttacherType = Attacher::AttachEngine3D
  Height = 17
  Radius = 8
FEATURE [Part::Cylinder] Cylinder218  label="Cylinder371"
  Angle = 360
  AttacherType = Attacher::AttachEngine3D
  Height = 17
  Radius = 6.5
FEATURE [Part::Cut] Cut438
  Base = -> Cylinder217
  Refine = true
  Tool = -> Cylinder218
FEATURE [Part::Fillet] Fillet004
  Base = -> Box428
  Edges = 4 edges r=1: [Edge1,Edge3,Edge5,Edge7]
FEATURE [Part::Cut] Cut439
  Base = -> Cylinder216
  Refine = true
  Tool = -> Fillet004
FEATURE [Part::MultiFuse] Fusion010
  Refine = true
  Shapes = -> [Cut438,Cut439]
FEATURE [Part::Cylinder] Cylinder024
  Angle = 360
  AttacherType = Attacher::AttachEngine3D
  Height = 27
  Radius = 8
FEATURE [Part::Cut] Cut440  label="cylinder-motor-extender"
  Base = -> Cylinder024
  Placement = pos=(309.5,98.5,187.5) rot=(0,1,0;1.5708rad)
  Refine = true
  Tool = -> Fusion010
FEATURE [Part::Cylinder] Cylinder219  label="Cylinder372"
  Angle = 360
  AttacherType = Attacher::AttachEngine3D
  Height = 3
  Placement = pos=(333.5,98.5,186.5) rot=(0,1,0;1.5708rad)
  Radius = 5
FEATURE [Part::Cylinder] Cylinder220  label="Cylinder373"
  Angle = 360
  AttacherType = Attacher::AttachEngine3D
  Height = 6
  Placement = pos=(336.5,98.5,186.5) rot=(0,1,0;1.5708rad)
  Radius = 6.1
FEATURE [Part::MultiFuse] Fusion248002050010
  Placement = pos=(3,0,1) rot=(0,0,1;0rad)
  Refine = true
  Shapes = -> [Cylinder219,Cylinder220]
FEATURE [Part::Cone] Cone003
  Angle = 360
  AttacherType = Attacher::AttachEngine3D
  Height = 13
  Placement = pos=(0,0,-13) rot=(0,0,1;0rad)
  Radius1 = 5
  Radius2 = 7.5
FEATURE [Part::Box] Box012  label="Cube014"
  AttacherType = Attacher::AttachEngine3D
  Height = 12
  Length = 16
  Placement = pos=(-8,3,-12) rot=(0,0,1;0rad)
  Width = 10
FEATURE [Part::Box] Box013  label="Cube654"
  AttacherType = Attacher::AttachEngine3D
  Height = 12
  Length = 16
  Placement = pos=(-8,-13,-12) rot=(0,0,1;0rad)
  Width = 10
FEATURE [Part::MultiFuse] Fusion006
  Placement = pos=(0,0,-1) rot=(0,0,1;0rad)
  Refine = true
  Shapes = -> [Box013,Box012]
FEATURE [Part::Cylinder] Cylinder221  label="Cylinder374"
  Angle = 360
  AttacherType = Attacher::AttachEngine3D
  Height = 10
  Placement = pos=(0,5,-8) rot=(1,0,0;1.5708rad)
  Radius = 3.1
FEATURE [Part::Cut] Cut016
  Base = -> Cone003
  Refine = true
  Tool = -> Fusion006
FEATURE [Part::Cut] Cut028
  Base = -> Cut016
  Placement = pos=(307.5,98.5,187.5) rot=(0,1,0;1.5708rad)
  Refine = true
  Tool = -> Cylinder221
FEATURE [Part::Cylinder] Cylinder222  label="Cylinder375"
  Angle = 360
  AttacherType = Attacher::AttachEngine3D
  Height = 1
  Placement = pos=(306.5,98.5,187.5) rot=(0,1,0;1.5708rad)
  Radius = 8
FEATURE [Part::Cut] Cut441
  Base = -> Cut028
  Refine = true
  Tool = -> Cylinder222
FEATURE [Part::Cylinder] Cylinder223  label="Cylinder376"
  Angle = 360
  AttacherType = Attacher::AttachEngine3D
  Height = 14
  Placement = pos=(184,47,128) rot=(1,0,0;1.5708rad)
  Radius = 1
FEATURE [Part::Cylinder] Cylinder224  label="Cylinder377"
  Angle = 360
  AttacherType = Attacher::AttachEngine3D
  Height = 1.6
  Placement = pos=(184,47,128) rot=(1,0,0;1.5708rad)
  Radius = 2.1
FEATURE [Part::MultiFuse] Fusion248002050011
  Placement = pos=(124,59,65) rot=(0,0,1;0rad)
  Refine = true
  Shapes = -> [Cylinder223,Cylinder224]
FEATURE [Part::Fillet] Fillet271
  Base = -> Box427
  Edges = 4 edges r=3: [Edge9,Edge10,Edge11,Edge12]
FEATURE [Part::Cylinder] Cylinder225  label="Cylinder378"
  Angle = 360
  AttacherType = Attacher::AttachEngine3D
  Height = 14
  Placement = pos=(184,47,128) rot=(1,0,0;1.5708rad)
  Radius = 1
FEATURE [Part::Cylinder] Cylinder226  label="Cylinder379"
  Angle = 360
  AttacherType = Attacher::AttachEngine3D
  Height = 1.6
  Placement = pos=(184,47,128) rot=(1,0,0;1.5708rad)
  Radius = 2.1
FEATURE [Part::MultiFuse] Fusion248002050012
  Placement = pos=(154,59,65) rot=(0,0,1;0rad)
  Refine = true
  Shapes = -> [Cylinder225,Cylinder226]
FEATURE [Part::Cylinder] Cylinder227  label="Cylinder380"
  Angle = 360
  AttacherType = Attacher::AttachEngine3D
  Height = 14
  Placement = pos=(184,47,128) rot=(1,0,0;1.5708rad)
  Radius = 1
FEATURE [Part::Cylinder] Cylinder228  label="Cylinder381"
  Angle = 360
  AttacherType = Attacher::AttachEngine3D
  Height = 1.6
  Placement = pos=(184,47,128) rot=(1,0,0;1.5708rad)
  Radius = 2.1
FEATURE [Part::MultiFuse] Fusion248002050013
  Placement = pos=(124,59,54) rot=(0,0,1;0rad)
  Refine = true
  Shapes = -> [Cylinder227,Cylinder228]
FEATURE [Part::Cylinder] Cylinder229  label="Cylinder382"
  Angle = 360
  AttacherType = Attacher::AttachEngine3D
  Height = 14
  Placement = pos=(184,47,128) rot=(1,0,0;1.5708rad)
  Radius = 1
FEATURE [Part::Cylinder] Cylinder230  label="Cylinder383"
  Angle = 360
  AttacherType = Attacher::AttachEngine3D
  Height = 1.6
  Placement = pos=(184,47,128) rot=(1,0,0;1.5708rad)
  Radius = 2.1
FEATURE [Part::MultiFuse] Fusion248002050014
  Placement = pos=(154,59,54) rot=(0,0,1;0rad)
  Refine = true
  Shapes = -> [Cylinder229,Cylinder230]
FEATURE [Part::MultiFuse] Fusion248002050015
  Placement = pos=(0,1,0) rot=(0,0,1;0rad)
  Refine = true
  Shapes = -> [Fusion248002050011,Fusion248002050012,Fusion248002050013,Fusion248002050014]
FEATURE [Part::MultiFuse] Fusion248002050016
  Refine = true
  Shapes = -> [Cut441,Fillet271]
FEATURE [Part::MultiFuse] Fusion248002050017
  Refine = true
  Shapes = -> [Cut440,Fusion248002050010,Fusion248002050015]
FEATURE [Part::Cut] Cut442
  Base = -> Fusion248002050016
  Refine = true
  Tool = -> Fusion248002050017
FEATURE [Part::Box] Box429  label="Cube655"
  AttacherType = Attacher::AttachEngine3D
  Height = 15
  Length = 54
  Placement = pos=(294.5,91,180) rot=(0,0,1;0rad)
  Width = 10.5
FEATURE [Part::Box] Box430  label="Cube656"
  AttacherType = Attacher::AttachEngine3D
  Height = 15
  Length = 39
  Placement = pos=(306.5,101.5,180) rot=(0,0,1;0rad)
  Width = 4.5
FEATURE [Part::Box] Box431  label="Cube657"
  AttacherType = Attacher::AttachEngine3D
  Height = 15
  Length = 39
  Placement = pos=(306.5,91,180) rot=(0,0,1;0rad)
  Width = 15
FEATURE [Part::Cylinder] Cylinder231  label="Cylinder384"
  Angle = 360
  AttacherType = Attacher::AttachEngine3D
  Height = 27
  Radius = 8
FEATURE [Part::Box] Box432  label="Cube658"
  AttacherType = Attacher::AttachEngine3D
  Height = 27
  Length = 10.4
  Placement = pos=(-5.2,-6.2,0) rot=(0,0,1;0rad)
  Width = 12.4
FEATURE [Part::Cylinder] Cylinder232  label="Cylinder385"
  Angle = 360
  AttacherType = Attacher::AttachEngine3D
  Height = 17
  Radius = 8
FEATURE [Part::Cylinder] Cylinder233  label="Cylinder386"
  Angle = 360
  AttacherType = Attacher::AttachEngine3D
  Height = 17
  Radius = 6.5
FEATURE [Part::Cut] Cut443
  Base = -> Cylinder232
  Refine = true
  Tool = -> Cylinder233
FEATURE [Part::Fillet] Fillet272
  Base = -> Box432
  Edges = 4 edges r=1: [Edge1,Edge3,Edge5,Edge7]
FEATURE [Part::Cut] Cut444
  Base = -> Cylinder231
  Refine = true
  Tool = -> Fillet272
FEATURE [Part::MultiFuse] Fusion248002050018
  Refine = true
  Shapes = -> [Cut443,Cut444]
FEATURE [Part::Cylinder] Cylinder234  label="Cylinder387"
  Angle = 360
  AttacherType = Attacher::AttachEngine3D
  Height = 27
  Radius = 8
FEATURE [Part::Cut] Cut445  label="cylinder-motor-extender001"
  Base = -> Cylinder234
  Placement = pos=(309.5,98.5,187.5) rot=(0,1,0;1.5708rad)
  Refine = true
  Tool = -> Fusion248002050018
FEATURE [Part::Cylinder] Cylinder235  label="Cylinder388"
  Angle = 360
  AttacherType = Attacher::AttachEngine3D
  Height = 3
  Placement = pos=(333.5,98.5,186.5) rot=(0,1,0;1.5708rad)
  Radius = 5
FEATURE [Part::Cylinder] Cylinder236  label="Cylinder389"
  Angle = 360
  AttacherType = Attacher::AttachEngine3D
  Height = 6
  Placement = pos=(336.5,98.5,186.5) rot=(0,1,0;1.5708rad)
  Radius = 6.1
FEATURE [Part::MultiFuse] Fusion248002050019
  Placement = pos=(3,0,1) rot=(0,0,1;0rad)
  Refine = true
  Shapes = -> [Cylinder235,Cylinder236]
FEATURE [Part::Cone] Cone004
  Angle = 360
  AttacherType = Attacher::AttachEngine3D
  Height = 13
  Placement = pos=(0,0,-13) rot=(0,0,1;0rad)
  Radius1 = 5
  Radius2 = 7.5
FEATURE [Part::Box] Box433  label="Cube659"
  AttacherType = Attacher::AttachEngine3D
  Height = 12
  Length = 16
  Placement = pos=(-8,3,-12) rot=(0,0,1;0rad)
  Width = 10
FEATURE [Part::Box] Box434  label="Cube660"
  AttacherType = Attacher::AttachEngine3D
  Height = 12
  Length = 16
  Placement = pos=(-8,-13,-12) rot=(0,0,1;0rad)
  Width = 10
FEATURE [Part::MultiFuse] Fusion248002050020
  Placement = pos=(0,0,-1) rot=(0,0,1;0rad)
  Refine = true
  Shapes = -> [Box434,Box433]
FEATURE [Part::Cylinder] Cylinder237  label="Cylinder390"
  Angle = 360
  AttacherType = Attacher::AttachEngine3D
  Height = 10
  Placement = pos=(0,5,-8) rot=(1,0,0;1.5708rad)
  Radius = 3.1
FEATURE [Part::Cut] Cut446
  Base = -> Cone004
  Refine = true
  Tool = -> Fusion248002050020
FEATURE [Part::Cut] Cut447
  Base = -> Cut446
  Placement = pos=(307.5,98.5,187.5) rot=(0,1,0;1.5708rad)
  Refine = true
  Tool = -> Cylinder237
FEATURE [Part::Cylinder] Cylinder238  label="Cylinder391"
  Angle = 360
  AttacherType = Attacher::AttachEngine3D
  Height = 1
  Placement = pos=(306.5,98.5,187.5) rot=(0,1,0;1.5708rad)
  Radius = 8
FEATURE [Part::Cut] Cut448
  Base = -> Cut447
  Refine = true
  Tool = -> Cylinder238
FEATURE [Part::Cylinder] Cylinder239  label="Cylinder392"
  Angle = 360
  AttacherType = Attacher::AttachEngine3D
  Height = 14
  Placement = pos=(184,47,128) rot=(1,0,0;1.5708rad)
  Radius = 1
FEATURE [Part::Cylinder] Cylinder240  label="Cylinder393"
  Angle = 360
  AttacherType = Attacher::AttachEngine3D
  Height = 1.6
  Placement = pos=(184,47,128) rot=(1,0,0;1.5708rad)
  Radius = 2.1
FEATURE [Part::MultiFuse] Fusion248002050021
  Placement = pos=(124,59,65) rot=(0,0,1;0rad)
  Refine = true
  Shapes = -> [Cylinder239,Cylinder240]
FEATURE [Part::Fillet] Fillet273
  Base = -> Box431
  Edges = 4 edges r=3: [Edge9,Edge10,Edge11,Edge12]
FEATURE [Part::Cylinder] Cylinder241  label="Cylinder394"
  Angle = 360
  AttacherType = Attacher::AttachEngine3D
  Height = 14
  Placement = pos=(184,47,128) rot=(1,0,0;1.5708rad)
  Radius = 1
FEATURE [Part::Cylinder] Cylinder242  label="Cylinder395"
  Angle = 360
  AttacherType = Attacher::AttachEngine3D
  Height = 1.6
  Placement = pos=(184,47,128) rot=(1,0,0;1.5708rad)
  Radius = 2.1
FEATURE [Part::MultiFuse] Fusion248002050022
  Placement = pos=(154,59,65) rot=(0,0,1;0rad)
  Refine = true
  Shapes = -> [Cylinder241,Cylinder242]
FEATURE [Part::Cylinder] Cylinder243  label="Cylinder396"
  Angle = 360
  AttacherType = Attacher::AttachEngine3D
  Height = 14
  Placement = pos=(184,47,128) rot=(1,0,0;1.5708rad)
  Radius = 1
FEATURE [Part::Cylinder] Cylinder244  label="Cylinder397"
  Angle = 360
  AttacherType = Attacher::AttachEngine3D
  Height = 1.6
  Placement = pos=(184,47,128) rot=(1,0,0;1.5708rad)
  Radius = 2.1
FEATURE [Part::MultiFuse] Fusion248002050023
  Placement = pos=(124,59,54) rot=(0,0,1;0rad)
  Refine = true
  Shapes = -> [Cylinder243,Cylinder244]
FEATURE [Part::Cylinder] Cylinder245  label="Cylinder398"
  Angle = 360
  AttacherType = Attacher::AttachEngine3D
  Height = 14
  Placement = pos=(184,47,128) rot=(1,0,0;1.5708rad)
  Radius = 1
FEATURE [Part::Cylinder] Cylinder246  label="Cylinder399"
  Angle = 360
  AttacherType = Attacher::AttachEngine3D
  Height = 1.6
  Placement = pos=(184,47,128) rot=(1,0,0;1.5708rad)
  Radius = 2.1
FEATURE [Part::MultiFuse] Fusion248002050024
  Placement = pos=(154,59,54) rot=(0,0,1;0rad)
  Refine = true
  Shapes = -> [Cylinder245,Cylinder246]
FEATURE [Part::MultiFuse] Fusion248002050025
  Placement = pos=(0,1,0) rot=(0,0,1;0rad)
  Refine = true
  Shapes = -> [Fusion248002050021,Fusion248002050022,Fusion248002050023,Fusion248002050024]
FEATURE [Part::MultiFuse] Fusion248002050026
  Refine = true
  Shapes = -> [Cut448,Fillet273]
FEATURE [Part::MultiFuse] Fusion248002050027
  Refine = true
  Shapes = -> [Cut445,Fusion248002050019,Fusion248002050025]
FEATURE [Part::Cut] Cut449
  Base = -> Fusion248002050026
  Refine = true
  Tool = -> Fusion248002050027
FEATURE [Part::Cut] Cut450  label="extender-cylinder-motor-holder-left"
  Base = -> Cut442
  Placement = pos=(12,0,2) rot=(0,0,1;0rad)
  Refine = true
  Tool = -> Box429
FEATURE [Part::Cut] Cut451  label="extender-cylinder-motor-holder-right_"
  Base = -> Cut449
  Refine = true
  Tool = -> Box430
FEATURE [Part::Box] Box435  label="Cube661"
  AttacherType = Attacher::AttachEngine3D
  Height = 5
  Length = 2
  Placement = pos=(309.5,91,185) rot=(0,0,1;0rad)
  Width = 5
FEATURE [Part::Cut] Cut452  label="extender-cylinder-motor-holder-right"
  Base = -> Cut451
  Placement = pos=(12,0,2) rot=(0,0,1;0rad)
  Refine = true
  Tool = -> Box435
FEATURE [Part::Box] Box436  label="Cube662"
  AttacherType = Attacher::AttachEngine3D
  Height = 4
  Length = 8
  Placement = pos=(483.5,94.5,179.5) rot=(0,0,1;0rad)
  Width = 8
FEATURE [Part::Cylinder] Cylinder247  label="Cylinder400"
  Angle = 360
  AttacherType = Attacher::AttachEngine3D
  Height = 5
  Placement = pos=(483.5,98.5,187.5) rot=(0,1,0;1.5708rad)
  Radius = 6.1
FEATURE [Part::Cut] Cut453
  Base = -> Box436
  Refine = true
  Tool = -> Cylinder247
FEATURE [Part::MultiFuse] Fusion248002050028  label="extender-cylinder-front-mount"
  Placement = pos=(12,0,2) rot=(0,0,1;0rad)
  Refine = true
  Shapes = -> [Cut437,Cut453]
FEATURE [Part::Box] Box437  label="Cube663"
  AttacherType = Attacher::AttachEngine3D
  Height = 20
  Length = 180
  Placement = pos=(319,93.5,155) rot=(0,0,1;0rad)
  Width = 10
FEATURE [Part::Box] Box438  label="Cube664"
  AttacherType = Attacher::AttachEngine3D
  Height = 18
  Length = 180
  Placement = pos=(319,94.5,156) rot=(0,0,1;0rad)
  Width = 8
FEATURE [Part::Cut] Cut454  label="externder-arm-ALU"
  Base = -> Box437
  Placement = pos=(15.5,0,2) rot=(0,0,1;0rad)
  Refine = true
  Tool = -> Box438
FEATURE [Part::Box] Box439  label="Cube665"
  AttacherType = Attacher::AttachEngine3D
  Height = 29
  Length = 13
  Placement = pos=(491.5,91,149) rot=(0,0,1;0rad)
  Width = 15
FEATURE [Part::Cylinder] Cylinder248  label="Cylinder401"
  Angle = 360
  AttacherType = Attacher::AttachEngine3D
  Height = 6
  Placement = pos=(498,98.5,149) rot=(0,0,1;0rad)
  Radius = 5.6
FEATURE [Part::Box] Box440  label="Cube666"
  AttacherType = Attacher::AttachEngine3D
  Height = 13
  Length = 10
  Placement = pos=(494.5,91,178) rot=(0,0,1;0rad)
  Width = 4.3
FEATURE [Part::Cylinder] Cylinder249  label="extender-arm-cylinder"
  Angle = 360
  AttacherType = Attacher::AttachEngine3D
  Height = 140
  Placement = pos=(374,98.5,189.5) rot=(0,1,0;1.5708rad)
  Radius = 3.1
FEATURE [Part::Box] Box441  label="Cube667"
  AttacherType = Attacher::AttachEngine3D
  Height = 20.8
  Length = 11
  Placement = pos=(491.5,93.1,154.6) rot=(0,0,1;0rad)
  Width = 10.8
FEATURE [Part::Cut] Cut456
  Base = -> Box439
  Refine = true
  Tool = -> Box441
FEATURE [Part::Cut] Cut457
  Base = -> Cut456
  Refine = true
  Tool = -> Cylinder248
FEATURE [Part::Cylinder] Cylinder250  label="Cylinder403"
  Angle = 360
  AttacherType = Attacher::AttachEngine3D
  Height = 17
  Placement = pos=(498,107,152) rot=(1,0,0;1.5708rad)
  Radius = 1.25
FEATURE [Part::Cylinder] Cylinder251  label="Cylinder404"
  Angle = 360
  AttacherType = Attacher::AttachEngine3D
  Height = 17
  Placement = pos=(499.5,107,188) rot=(1,0,0;1.5708rad)
  Radius = 1.25
FEATURE [Part::Cylinder] Cylinder252  label="Cylinder405"
  Angle = 360
  AttacherType = Attacher::AttachEngine3D
  Height = 17
  Placement = pos=(498,107,165) rot=(1,0,0;1.5708rad)
  Radius = 1.25
FEATURE [Part::Box] Box442  label="Cube668"
  AttacherType = Attacher::AttachEngine3D
  Height = 13
  Length = 10
  Placement = pos=(494.5,101.7,178) rot=(0,0,1;0rad)
  Width = 4.3
FEATURE [Part::MultiFuse] Fusion248002050030
  Refine = true
  Shapes = -> [Box440,Box442]
FEATURE [Part::Chamfer] Chamfer110
  Base = -> Fusion248002050030
  Edges = 2 edges r=3: [Edge6,Edge18]
FEATURE [Part::Fillet] Fillet274
  Base = -> Chamfer110
  Edges = 4 edges r=3: [Edge9,Edge15,Edge24,Edge30]
FEATURE [Part::Cut] Cut460
  Base = -> Fillet274
  Refine = true
  Tool = -> Cylinder251
FEATURE [Part::Box] Box443  label="Cube669"
  AttacherType = Attacher::AttachEngine3D
  Height = 6
  Length = 11
  Placement = pos=(487,92.9,149) rot=(0,0,1;0rad)
  Width = 11.2
FEATURE [Part::MultiFuse] Fusion248002050031
  Refine = true
  Shapes = -> [Cylinder250,Cylinder252]
FEATURE [Part::Cut] Cut461
  Base = -> Cut457
  Refine = true
  Tool = -> Fusion248002050031
FEATURE [Part::Cut] Cut462
  Base = -> Cut461
  Refine = true
  Tool = -> Box443
FEATURE [Part::MultiFuse] Fusion248002050032
  Refine = true
  Shapes = -> [Cut462,Cut460]
FEATURE [Part::Chamfer] Chamfer111  label="extender-arm-head"
  Base = -> Fusion248002050032
  Edges = 2 edges r=1: [Edge109,Edge110]
  Placement = pos=(12,0,2) rot=(0,0,1;0rad)
FEATURE [Part::Cylinder] Cylinder253  label="Cylinder406"
  Angle = 360
  AttacherType = Attacher::AttachEngine3D
  Height = 12
  Placement = pos=(13,12.5,-3) rot=(0,0,1;0rad)
  Radius = 1.25
FEATURE [Part::Cylinder] Cylinder254  label="Cylinder407"
  Angle = 360
  AttacherType = Attacher::AttachEngine3D
  Height = 11
  Placement = pos=(9,18,-2) rot=(0,0,1;0rad)
  Radius = 1.25
FEATURE [Part::Cylinder] Cylinder255  label="Cylinder408"
  Angle = 360
  AttacherType = Attacher::AttachEngine3D
  Height = 11
  Placement = pos=(9,7,-2) rot=(0,0,1;0rad)
  Radius = 1.25
FEATURE [Part::Cylinder] Cylinder256  label="Cylinder409"
  Angle = 360
  AttacherType = Attacher::AttachEngine3D
  Height = 11
  Placement = pos=(18,18,-2) rot=(0,0,1;0rad)
  Radius = 1.25
FEATURE [Part::Cylinder] Cylinder257  label="Cylinder410"
  Angle = 360
  AttacherType = Attacher::AttachEngine3D
  Height = 11
  Placement = pos=(18,7,-2) rot=(0,0,1;0rad)
  Radius = 1.25
FEATURE [Part::MultiFuse] Fusion248002050033
  Placement = pos=(150,60,39) rot=(0,0,1;0rad)
  Refine = true
  Shapes = -> [Cylinder253,Cylinder254,Cylinder255,Cylinder257,Cylinder256]
FEATURE [Part::Cylinder] Cylinder258  label="Cylinder411"
  Angle = 360
  AttacherType = Attacher::AttachEngine3D
  Height = 20
  Placement = pos=(163,72.5,42) rot=(0,0,1;0rad)
  Radius = 9.3
FEATURE [Part::Box] Box444  label="Cube670"
  AttacherType = Attacher::AttachEngine3D
  Height = 13
  Length = 22
  Placement = pos=(152,61.5,39) rot=(0,0,1;0rad)
  Width = 22
FEATURE [Part::Cut] Cut463
  Base = -> Box444
  Refine = true
  Tool = -> Cylinder258
FEATURE [Part::Cut] Cut464  label="crane-rotating-axis-HOLES"
  Base = -> Cut463
  Placement = pos=(12,0,3) rot=(0,0,1;0rad)
  Refine = true
  Tool = -> Fusion248002050033
FEATURE [Part::Cylinder] Cylinder1075  label="Cylinder1414"
  Angle = 360
  AttacherType = Attacher::AttachEngine3D
  Height = 11.5
  Placement = pos=(133,85,5.5) rot=(0,1,0;1.5708rad)
  Radius = 5.5
FEATURE [Part::Cylinder] Cylinder1076  label="Cylinder1304"
  Angle = 360
  AttacherType = Attacher::AttachEngine3D
  Height = 11.5
  Placement = pos=(218,85,-6.75) rot=(0,1,0;1.5708rad)
  Radius = 5.5
FEATURE [Part::Cylinder] Cylinder1077  label="Cylinder1415"
  Angle = 360
  AttacherType = Attacher::AttachEngine3D
  Height = 74
  Placement = pos=(144.5,85,5.5) rot=(0,1,0;1.7366rad)
  Radius = 2.5
FEATURE [Part::MultiFuse] Fusion248002049  label="gearbox-prop-shaft"
  Refine = true
  Shapes = -> [Cylinder1075,Cylinder1077,Cylinder1076]
FEATURE [Part::Feature] Fusion281001  label="kipper"
  shape: bbox 313 x 186 x 59 mm, 528 faces, 2 solids (baked)
FEATURE [Part::Cylinder] Cylinder1080  label="Cylinder1416"
  Angle = 360
  AttacherType = Attacher::AttachEngine3D
  Height = 27
  Radius = 8
FEATURE [Part::Box] Box448  label="Cube674"
  AttacherType = Attacher::AttachEngine3D
  Height = 27
  Length = 10.4
  Placement = pos=(-5.2,-6.2,0) rot=(0,0,1;0rad)
  Width = 12.4
FEATURE [Part::Cylinder] Cylinder1081  label="Cylinder1417"
  Angle = 360
  AttacherType = Attacher::AttachEngine3D
  Height = 17
  Radius = 8
FEATURE [Part::Cylinder] Cylinder1082  label="Cylinder1418"
  Angle = 360
  AttacherType = Attacher::AttachEngine3D
  Height = 17
  Radius = 6.5
FEATURE [Part::Cut] Cut466
  Base = -> Cylinder1081
  Refine = true
  Tool = -> Cylinder1082
FEATURE [Part::Fillet] Fillet275
  Base = -> Box448
  Edges = 4 edges r=1: [Edge1,Edge3,Edge5,Edge7]
FEATURE [Part::Cut] Cut467
  Base = -> Cylinder1080
  Refine = true
  Tool = -> Fillet275
FEATURE [Part::MultiFuse] Fusion248002050035
  Refine = true
  Shapes = -> [Cut466,Cut467]
FEATURE [Part::Cylinder] Cylinder1083  label="Cylinder1419"
  Angle = 360
  AttacherType = Attacher::AttachEngine3D
  Height = 27
  Radius = 8
FEATURE [Part::Cut] Cut468  label="cylinder-motor-supports-001"
  Base = -> Cylinder1083
  Placement = pos=(175,76,18) rot=(1,0,0;1.5708rad)
  Refine = true
  Tool = -> Fusion248002050035
FEATURE [Part::Cylinder] Cylinder1084  label="Cylinder1420"
  Angle = 360
  AttacherType = Attacher::AttachEngine3D
  Height = 27
  Radius = 8
FEATURE [Part::Box] Box449  label="Cube675"
  AttacherType = Attacher::AttachEngine3D
  Height = 27
  Length = 10.4
  Placement = pos=(-5.2,-6.2,0) rot=(0,0,1;0rad)
  Width = 12.4
FEATURE [Part::Cylinder] Cylinder1085  label="Cylinder1421"
  Angle = 360
  AttacherType = Attacher::AttachEngine3D
  Height = 17
  Radius = 8
FEATURE [Part::Cylinder] Cylinder1086  label="Cylinder1422"
  Angle = 360
  AttacherType = Attacher::AttachEngine3D
  Height = 17
  Radius = 6.5
FEATURE [Part::Cut] Cut469
  Base = -> Cylinder1085
  Refine = true
  Tool = -> Cylinder1086
FEATURE [Part::Fillet] Fillet276
  Base = -> Box449
  Edges = 4 edges r=1: [Edge1,Edge3,Edge5,Edge7]
FEATURE [Part::Cut] Cut470
  Base = -> Cylinder1084
  Refine = true
  Tool = -> Fillet276
FEATURE [Part::MultiFuse] Fusion248002050036
  Refine = true
  Shapes = -> [Cut469,Cut470]
FEATURE [Part::Cylinder] Cylinder1087  label="Cylinder1423"
  Angle = 360
  AttacherType = Attacher::AttachEngine3D
  Height = 27
  Radius = 8
FEATURE [Part::Cut] Cut471  label="cylinder-motor-supports-002"
  Base = -> Cylinder1087
  Placement = pos=(175,114,18) rot=(-1,0,0;1.5708rad)
  Refine = true
  Tool = -> Fusion248002050036
FEATURE [Part::Cylinder] Cylinder1088  label="Cylinder1424"
  Angle = 360
  AttacherType = Attacher::AttachEngine3D
  Height = 63
  Placement = pos=(175,49,18) rot=(1,0,0;1.5708rad)
  Radius = 1.5
FEATURE [Part::Cylinder] Cylinder1089  label="Cylinder1425"
  Angle = 360
  AttacherType = Attacher::AttachEngine3D
  Height = 63
  Placement = pos=(175,204,18) rot=(1,0,0;1.5708rad)
  Radius = 1.5
FEATURE [Part::MultiFuse] Fusion248002050037  label="crane-stabilizers-opener-motor-left"
  Placement = pos=(172,-42.5,185.8) rot=(0,1,0;1.5708rad)
  Refine = true
  Shapes = -> [Cut471,Cylinder1089]
FEATURE [Part::MultiFuse] Fusion248002050038  label="crane-stabilizers-opener-motor-right"
  Placement = pos=(172,22.5,196.2) rot=(0,1,0;1.5708rad)
  Refine = true
  Shapes = -> [Cut468,Cylinder1088]
FEATURE [Part::MultiFuse] Fusion138  label="right-rear-wing"
  Placement = pos=(0,0,3) rot=(0,0,1;0rad)
  Refine = true
FEATURE [Part::Mirroring] Part__Mirroring018  label="left-rear-wing"
  Base = (0,0,0)
  Normal = (0,1,0)
  Placement = pos=(0,170,3) rot=(0,0,1;0rad)
FEATURE [Part::Box] Box450  label="Cube676"
  AttacherType = Attacher::AttachEngine3D
  Height = 20.5
  Length = 10.6
  Placement = pos=(181,-7,5.75) rot=(0,0,1;0rad)
  Width = 184
FEATURE [Part::Cylinder] Cylinder1090  label="Cylinder1426"
  Angle = 360
  AttacherType = Attacher::AttachEngine3D
  Height = 7
  Placement = pos=(168.5,72.5,2) rot=(0,0,1;0rad)
  Radius = 6.75
FEATURE [Part::Cylinder] Cylinder1091  label="Cylinder1427"
  Angle = 360
  AttacherType = Attacher::AttachEngine3D
  Height = 15
  Placement = pos=(168.5,72.5,8) rot=(0,0,1;0rad)
  Radius = 4
FEATURE [Part::Box] Box451  label="Cube677"
  AttacherType = Attacher::AttachEngine3D
  Height = 26
  Length = 16
  Placement = pos=(178.25,10,2) rot=(0,0,1;0rad)
  Width = 150
FEATURE [Part::Cylinder] Cylinder1092  label="Cylinder1428"
  Angle = 360
  AttacherType = Attacher::AttachEngine3D
  Height = 5
  Placement = pos=(168.5,72.5,23) rot=(0,0,1;0rad)
  Radius = 8.2
FEATURE [Part::Cylinder] Cylinder1093  label="Cylinder1429"
  Angle = 360
  AttacherType = Attacher::AttachEngine3D
  Height = 5
  Placement = pos=(168.5,72.5,9) rot=(0,0,1;0rad)
  Radius = 6.6
FEATURE [Part::MultiFuse] Fusion248002050039
  Placement = pos=(3,0,0) rot=(0,0,1;0rad)
  Refine = true
  Shapes = -> [Cylinder1090,Cylinder1091,Cylinder1092,Cylinder1093]
FEATURE [Part::Box] Box452  label="Cube678"
  AttacherType = Attacher::AttachEngine3D
  Height = 26
  Length = 27.25
  Placement = pos=(151,57,2) rot=(0,0,1;0rad)
  Width = 56
FEATURE [Part::Cylinder] Cylinder1094  label="Cylinder1430"
  Angle = 360
  AttacherType = Attacher::AttachEngine3D
  Height = 74
  Placement = pos=(144.5,85,5.5) rot=(0,1,0;1.7366rad)
  Radius = 4
FEATURE [Part::Box] Box453  label="Cube679"
  AttacherType = Attacher::AttachEngine3D
  Height = 10
  Length = 8
  Placement = pos=(150,78.5,-4.5) rot=(0,0,1;0rad)
  Width = 13
FEATURE [Part::Cylinder] Cylinder1095  label="Cylinder1431"
  Angle = 360
  AttacherType = Attacher::AttachEngine3D
  Height = 25
  Placement = pos=(133,85,5.5) rot=(0,1,0;1.5708rad)
  Radius = 6.5
FEATURE [Part::MultiFuse] Fusion248002050041
  Refine = true
  Shapes = -> [Box453,Cylinder1094,Cylinder1095]
FEATURE [Part::Cut] Cut472
  Base = -> Box451
  Refine = true
  Tool = -> Box450
FEATURE [Part::Cut] Cut473
  Base = -> Box452
  Refine = true
  Tool = -> Fusion248002050039
FEATURE [Part::Box] Box454  label="Cube680"
  AttacherType = Attacher::AttachEngine3D
  Height = 26
  Length = 16
  Placement = pos=(178.25,69,2) rot=(0,0,1;0rad)
  Width = 32
FEATURE [Part::Box] Box455  label="Cube681"
  AttacherType = Attacher::AttachEngine3D
  Height = 26
  Length = 16
  Placement = pos=(178.25,70,2) rot=(0,0,1;0rad)
  Width = 30
FEATURE [Part::Cut] Cut474
  Base = -> Cut472
  Refine = true
  Tool = -> Box455
FEATURE [Part::Cylinder] Cylinder1098  label="Cylinder1432"
  Angle = 360
  AttacherType = Attacher::AttachEngine3D
  Height = 5
  Placement = pos=(186.5,103,8.8) rot=(1,0,0;1.5708rad)
  Radius = 4
FEATURE [Part::Box] Box456  label="Cube682"
  AttacherType = Attacher::AttachEngine3D
  Height = 20.8
  Length = 12.5
  Placement = pos=(180.25,71.5,3.6) rot=(0,0,1;0rad)
  Width = 27
FEATURE [Part::Cylinder] Cylinder1099  label="Cylinder1433"
  Angle = 360
  AttacherType = Attacher::AttachEngine3D
  Height = 5
  Placement = pos=(186.5,72,19.2) rot=(1,0,0;1.5708rad)
  Radius = 4
FEATURE [Part::MultiFuse] Fusion248002050043
  Placement = pos=(0,0,2) rot=(0,0,1;0rad)
  Refine = true
  Shapes = -> [Cylinder1098,Box456,Cylinder1099]
FEATURE [Part::Cut] Cut475
  Base = -> Box454
  Refine = true
  Tool = -> Fusion248002050043
FEATURE [Part::MultiFuse] Fusion248002050044
  Refine = true
  Shapes = -> [Cut473,Cut474,Cut475]
FEATURE [Part::Cut] Cut476
  Base = -> Fusion248002050044
  Refine = true
  Tool = -> Fusion248002050041
FEATURE [Part::Box] Box461  label="Cube687"
  AttacherType = Attacher::AttachEngine3D
  Height = 3.75
  Length = 19.75
  Placement = pos=(178,57,2) rot=(0,0,1;0rad)
  Width = 56
FEATURE [Part::Cylinder] Cylinder1101  label="Cylinder1434"
  Angle = 360
  AttacherType = Attacher::AttachEngine3D
  Height = 15
  Placement = pos=(177,90,2) rot=(0,0,1;0rad)
  Radius = 1
FEATURE [Part::Box] Box458  label="Cube684"
  AttacherType = Attacher::AttachEngine3D
  Height = 3.75
  Length = 20
  Placement = pos=(174.25,10,2) rot=(0,0,1;0rad)
  Width = 150
FEATURE [Part::Cut] Cut477
  Base = -> Cut476
  Refine = true
  Tool = -> Box458
FEATURE [Part::Box] Box463  label="Cube689"
  AttacherType = Attacher::AttachEngine3D
  Height = 1.75
  Length = 16
  Placement = pos=(181.75,10,4) rot=(0,0,1;0rad)
  Width = 150
FEATURE [Part::Cylinder] Cylinder1102  label="Cylinder1435"
  Angle = 360
  AttacherType = Attacher::AttachEngine3D
  Height = 74
  Placement = pos=(148,85,5.5) rot=(0,1,0;1.7366rad)
  Radius = 4
FEATURE [Part::Cylinder] Cylinder1103  label="Cylinder1436"
  Angle = 360
  AttacherType = Attacher::AttachEngine3D
  Height = 15
  Placement = pos=(177,80,2) rot=(0,0,1;0rad)
  Radius = 1
FEATURE [Part::Cylinder] Cylinder1106  label="Cylinder1437"
  Angle = 360
  AttacherType = Attacher::AttachEngine3D
  Height = 15
  Placement = pos=(179,158,2) rot=(0,0,1;0rad)
  Radius = 1
FEATURE [Part::Cylinder] Cylinder1107  label="Cylinder1438"
  Angle = 360
  AttacherType = Attacher::AttachEngine3D
  Height = 12
  Placement = pos=(179,158,3.75) rot=(0,0,1;0rad)
  Radius = 2
FEATURE [Part::Cylinder] Cylinder1108  label="Cylinder1439"
  Angle = 360
  AttacherType = Attacher::AttachEngine3D
  Height = 1.75
  Placement = pos=(179,158,2) rot=(0,0,1;0rad)
  Radius = 2
FEATURE [Part::Cylinder] Cylinder1109  label="Cylinder1440"
  Angle = 360
  AttacherType = Attacher::AttachEngine3D
  Height = 12
  Placement = pos=(193.5,158,3.75) rot=(0,0,1;0rad)
  Radius = 2
FEATURE [Part::Cylinder] Cylinder1110  label="Cylinder1441"
  Angle = 360
  AttacherType = Attacher::AttachEngine3D
  Height = 1.75
  Placement = pos=(193.5,158,2) rot=(0,0,1;0rad)
  Radius = 2
FEATURE [Part::Cylinder] Cylinder1111  label="Cylinder1442"
  Angle = 360
  AttacherType = Attacher::AttachEngine3D
  Height = 15
  Placement = pos=(193.5,158,2) rot=(0,0,1;0rad)
  Radius = 1
FEATURE [Part::MultiFuse] Fusion248002050048
  Refine = true
  Shapes = -> [Cylinder1110,Cylinder1108]
FEATURE [Part::MultiFuse] Fusion248002050050
  Refine = true
  Shapes = -> [Cylinder1107,Cylinder1109]
FEATURE [Part::Cylinder] Cylinder1112  label="Cylinder1443"
  Angle = 360
  AttacherType = Attacher::AttachEngine3D
  Height = 15
  Placement = pos=(179,158,2) rot=(0,0,1;0rad)
  Radius = 1
FEATURE [Part::Cylinder] Cylinder1113  label="Cylinder1444"
  Angle = 360
  AttacherType = Attacher::AttachEngine3D
  Height = 15
  Placement = pos=(193.5,158,2) rot=(0,0,1;0rad)
  Radius = 1
FEATURE [Part::MultiFuse] Fusion248002050051
  Refine = true
  Shapes = -> [Cylinder1106,Cylinder1111]
FEATURE [Part::MultiFuse] Fusion248002050052
  Placement = pos=(0,-25,0) rot=(0,0,1;0rad)
  Refine = true
  Shapes = -> [Cylinder1112,Cylinder1113]
FEATURE [Part::Cylinder] Cylinder1114  label="Cylinder1445"
  Angle = 360
  AttacherType = Attacher::AttachEngine3D
  Height = 1.75
  Placement = pos=(179,158,2) rot=(0,0,1;0rad)
  Radius = 2
FEATURE [Part::Cylinder] Cylinder1115  label="Cylinder1446"
  Angle = 360
  AttacherType = Attacher::AttachEngine3D
  Height = 1.75
  Placement = pos=(193.5,158,2) rot=(0,0,1;0rad)
  Radius = 2
FEATURE [Part::MultiFuse] Fusion248002050053
  Placement = pos=(0,-25,0) rot=(0,0,1;0rad)
  Refine = true
  Shapes = -> [Cylinder1115,Cylinder1114]
FEATURE [Part::Cylinder] Cylinder1116  label="Cylinder1447"
  Angle = 360
  AttacherType = Attacher::AttachEngine3D
  Height = 1.75
  Placement = pos=(179,158,2) rot=(0,0,1;0rad)
  Radius = 2
FEATURE [Part::Cylinder] Cylinder1117  label="Cylinder1448"
  Angle = 360
  AttacherType = Attacher::AttachEngine3D
  Height = 1.75
  Placement = pos=(193.5,158,2) rot=(0,0,1;0rad)
  Radius = 2
FEATURE [Part::MultiFuse] Fusion248002050054
  Placement = pos=(0,-121,0) rot=(0,0,1;0rad)
  Refine = true
  Shapes = -> [Cylinder1117,Cylinder1116]
FEATURE [Part::Cylinder] Cylinder1118  label="Cylinder1449"
  Angle = 360
  AttacherType = Attacher::AttachEngine3D
  Height = 1.75
  Placement = pos=(179,158,2) rot=(0,0,1;0rad)
  Radius = 2
FEATURE [Part::Cylinder] Cylinder1119  label="Cylinder1450"
  Angle = 360
  AttacherType = Attacher::AttachEngine3D
  Height = 1.75
  Placement = pos=(193.5,158,2) rot=(0,0,1;0rad)
  Radius = 2
FEATURE [Part::MultiFuse] Fusion248002050055
  Placement = pos=(0,-146,0) rot=(0,0,1;0rad)
  Refine = true
  Shapes = -> [Cylinder1119,Cylinder1118]
FEATURE [Part::Cylinder] Cylinder1122  label="Cylinder1451"
  Angle = 360
  AttacherType = Attacher::AttachEngine3D
  Height = 12
  Placement = pos=(179,158,3.75) rot=(0,0,1;0rad)
  Radius = 2
FEATURE [Part::Cylinder] Cylinder1123  label="Cylinder1452"
  Angle = 360
  AttacherType = Attacher::AttachEngine3D
  Height = 12
  Placement = pos=(193.5,158,3.75) rot=(0,0,1;0rad)
  Radius = 2
FEATURE [Part::MultiFuse] Fusion248002050057
  Placement = pos=(0,-25,0) rot=(0,0,1;0rad)
  Refine = true
  Shapes = -> [Cylinder1122,Cylinder1123]
FEATURE [Part::Cylinder] Cylinder1124  label="Cylinder1453"
  Angle = 360
  AttacherType = Attacher::AttachEngine3D
  Height = 12
  Placement = pos=(179,158,3.75) rot=(0,0,1;0rad)
  Radius = 2
FEATURE [Part::Cylinder] Cylinder1125  label="Cylinder1454"
  Angle = 360
  AttacherType = Attacher::AttachEngine3D
  Height = 12
  Placement = pos=(193.5,158,3.75) rot=(0,0,1;0rad)
  Radius = 2
FEATURE [Part::MultiFuse] Fusion248002050058
  Placement = pos=(0,-121,0) rot=(0,0,1;0rad)
  Refine = true
  Shapes = -> [Cylinder1124,Cylinder1125]
FEATURE [Part::Cylinder] Cylinder1126  label="Cylinder1455"
  Angle = 360
  AttacherType = Attacher::AttachEngine3D
  Height = 12
  Placement = pos=(179,158,3.75) rot=(0,0,1;0rad)
  Radius = 2
FEATURE [Part::Cylinder] Cylinder1127  label="Cylinder1456"
  Angle = 360
  AttacherType = Attacher::AttachEngine3D
  Height = 12
  Placement = pos=(193.5,158,3.75) rot=(0,0,1;0rad)
  Radius = 2
FEATURE [Part::MultiFuse] Fusion248002050059
  Placement = pos=(0,-146,0) rot=(0,0,1;0rad)
  Refine = true
  Shapes = -> [Cylinder1126,Cylinder1127]
FEATURE [Part::Cylinder] Cylinder1131  label="Cylinder1457"
  Angle = 360
  AttacherType = Attacher::AttachEngine3D
  Height = 15
  Placement = pos=(179,158,2) rot=(0,0,1;0rad)
  Radius = 1
FEATURE [Part::Cylinder] Cylinder1132  label="Cylinder1458"
  Angle = 360
  AttacherType = Attacher::AttachEngine3D
  Height = 15
  Placement = pos=(193.5,158,2) rot=(0,0,1;0rad)
  Radius = 1
FEATURE [Part::Cylinder] Cylinder1133  label="Cylinder1459"
  Angle = 360
  AttacherType = Attacher::AttachEngine3D
  Height = 15
  Placement = pos=(179,158,2) rot=(0,0,1;0rad)
  Radius = 1
FEATURE [Part::Cylinder] Cylinder1134  label="Cylinder1460"
  Angle = 360
  AttacherType = Attacher::AttachEngine3D
  Height = 15
  Placement = pos=(193.5,158,2) rot=(0,0,1;0rad)
  Radius = 1
FEATURE [Part::MultiFuse] Fusion248002050065
  Placement = pos=(0,-121,0) rot=(0,0,1;0rad)
  Refine = true
  Shapes = -> [Cylinder1131,Cylinder1132]
FEATURE [Part::MultiFuse] Fusion248002050066
  Placement = pos=(0,-146,0) rot=(0,0,1;0rad)
  Refine = true
  Shapes = -> [Cylinder1133,Cylinder1134]
FEATURE [Part::Cylinder] Cylinder1137  label="Cylinder1461"
  Angle = 360
  AttacherType = Attacher::AttachEngine3D
  Height = 12
  Placement = pos=(177,90,2) rot=(0,0,1;0rad)
  Radius = 1
FEATURE [Part::Cylinder] Cylinder1138  label="Cylinder1462"
  Angle = 360
  AttacherType = Attacher::AttachEngine3D
  Height = 12
  Placement = pos=(177,80,2) rot=(0,0,1;0rad)
  Radius = 1
FEATURE [Part::Cylinder] Cylinder1141  label="Cylinder1463"
  Angle = 360
  AttacherType = Attacher::AttachEngine3D
  Height = 12
  Placement = pos=(179,158,2) rot=(0,0,1;0rad)
  Radius = 1
FEATURE [Part::Cylinder] Cylinder1142  label="Cylinder1464"
  Angle = 360
  AttacherType = Attacher::AttachEngine3D
  Height = 12
  Placement = pos=(193.5,158,2) rot=(0,0,1;0rad)
  Radius = 1
FEATURE [Part::Cylinder] Cylinder1143  label="Cylinder1465"
  Angle = 360
  AttacherType = Attacher::AttachEngine3D
  Height = 12
  Placement = pos=(179,158,2) rot=(0,0,1;0rad)
  Radius = 1
FEATURE [Part::Cylinder] Cylinder1144  label="Cylinder1466"
  Angle = 360
  AttacherType = Attacher::AttachEngine3D
  Height = 12
  Placement = pos=(193.5,158,2) rot=(0,0,1;0rad)
  Radius = 1
FEATURE [Part::MultiFuse] Fusion248002050069
  Refine = true
  Shapes = -> [Cylinder1141,Cylinder1142]
FEATURE [Part::MultiFuse] Fusion248002050070
  Placement = pos=(0,-25,0) rot=(0,0,1;0rad)
  Refine = true
  Shapes = -> [Cylinder1143,Cylinder1144]
FEATURE [Part::Cylinder] Cylinder1145  label="Cylinder1467"
  Angle = 360
  AttacherType = Attacher::AttachEngine3D
  Height = 12
  Placement = pos=(179,158,2) rot=(0,0,1;0rad)
  Radius = 1
FEATURE [Part::Cylinder] Cylinder1146  label="Cylinder1468"
  Angle = 360
  AttacherType = Attacher::AttachEngine3D
  Height = 12
  Placement = pos=(193.5,158,2) rot=(0,0,1;0rad)
  Radius = 1
FEATURE [Part::Cylinder] Cylinder1147  label="Cylinder1469"
  Angle = 360
  AttacherType = Attacher::AttachEngine3D
  Height = 12
  Placement = pos=(179,158,2) rot=(0,0,1;0rad)
  Radius = 1
FEATURE [Part::Cylinder] Cylinder1148  label="Cylinder1470"
  Angle = 360
  AttacherType = Attacher::AttachEngine3D
  Height = 12
  Placement = pos=(193.5,158,2) rot=(0,0,1;0rad)
  Radius = 1
FEATURE [Part::MultiFuse] Fusion248002050072
  Placement = pos=(0,-121,0) rot=(0,0,1;0rad)
  Refine = true
  Shapes = -> [Cylinder1145,Cylinder1146]
FEATURE [Part::MultiFuse] Fusion248002050073
  Placement = pos=(0,-146,0) rot=(0,0,1;0rad)
  Refine = true
  Shapes = -> [Cylinder1147,Cylinder1148]
FEATURE [Part::Box] Box464  label="Cube690"
  AttacherType = Attacher::AttachEngine3D
  Height = 10
  Length = 11
  Placement = pos=(140,57,2) rot=(0,0,1;0rad)
  Width = 8
FEATURE [Part::Box] Box465  label="Cube691"
  AttacherType = Attacher::AttachEngine3D
  Height = 10
  Length = 11
  Placement = pos=(140,105,2) rot=(0,0,1;0rad)
  Width = 8
FEATURE [Part::MultiFuse] Fusion248002050078
  Refine = true
  Shapes = -> [Box465,Box464]
FEATURE [Part::Fillet] Fillet277
  Base = -> Fusion248002050078
  Edges = 4 edges r=3: [Edge1,Edge3,Edge13,Edge15]
FEATURE [Part::Cylinder] Cylinder1152  label="Cylinder1471"
  Angle = 360
  AttacherType = Attacher::AttachEngine3D
  Height = 10
  Placement = pos=(145,61,2) rot=(0,0,1;0rad)
  Radius = 1.6
FEATURE [Part::Cylinder] Cylinder1153  label="Cylinder1472"
  Angle = 360
  AttacherType = Attacher::AttachEngine3D
  Height = 10
  Placement = pos=(145,109,2) rot=(0,0,1;0rad)
  Radius = 1.6
FEATURE [Part::MultiFuse] Fusion248002050079
  Refine = true
  Shapes = -> [Cylinder1153,Cylinder1152]
FEATURE [Part::Cut] Cut481
  Base = -> Fillet277
  Refine = true
  Tool = -> Fusion248002050079
FEATURE [Part::Box] Box466  label="Cube692"
  AttacherType = Attacher::AttachEngine3D
  Height = 10
  Length = 11
  Placement = pos=(140,57,2) rot=(0,0,1;0rad)
  Width = 8
FEATURE [Part::Box] Box467  label="Cube693"
  AttacherType = Attacher::AttachEngine3D
  Height = 10
  Length = 11
  Placement = pos=(140,105,2) rot=(0,0,1;0rad)
  Width = 8
FEATURE [Part::MultiFuse] Fusion248002050081
  Refine = true
  Shapes = -> [Box467,Box466]
FEATURE [Part::Fillet] Fillet278
  Base = -> Fusion248002050081
  Edges = 4 edges r=3: [Edge1,Edge3,Edge13,Edge15]
FEATURE [Part::Cylinder] Cylinder1154  label="Cylinder1473"
  Angle = 360
  AttacherType = Attacher::AttachEngine3D
  Height = 10
  Placement = pos=(145,61,2) rot=(0,0,1;0rad)
  Radius = 1.6
FEATURE [Part::Cylinder] Cylinder1155  label="Cylinder1474"
  Angle = 360
  AttacherType = Attacher::AttachEngine3D
  Height = 10
  Placement = pos=(145,109,2) rot=(0,0,1;0rad)
  Radius = 1.6
FEATURE [Part::MultiFuse] Fusion248002050082
  Refine = true
  Shapes = -> [Cylinder1155,Cylinder1154]
FEATURE [Part::Cut] Cut482
  Base = -> Fillet278
  Placement = pos=(344.25,170,0) rot=(0,0,1;3.14159rad)
  Refine = true
  Tool = -> Fusion248002050082
FEATURE [Part::Cylinder] Cylinder1156  label="Cylinder1475"
  Angle = 360
  AttacherType = Attacher::AttachEngine3D
  Height = 10
  Placement = pos=(150,60,21) rot=(0,1,0;1.5708rad)
  Radius = 1.25
FEATURE [Part::Cylinder] Cylinder1157  label="Cylinder1476"
  Angle = 360
  AttacherType = Attacher::AttachEngine3D
  Height = 10
  Placement = pos=(150,110,21) rot=(0,1,0;1.5708rad)
  Radius = 1.25
FEATURE [Part::Cylinder] Cylinder1158  label="Cylinder1477"
  Angle = 360
  AttacherType = Attacher::AttachEngine3D
  Height = 10
  Placement = pos=(150,100,16) rot=(0,1,0;1.5708rad)
  Radius = 1.25
FEATURE [Part::Cylinder] Cylinder1159  label="Cylinder1478"
  Angle = 360
  AttacherType = Attacher::AttachEngine3D
  Height = 8
  Placement = pos=(150,70,16) rot=(0,1,0;1.5708rad)
  Radius = 1.25
FEATURE [Part::MultiFuse] Fusion248002050083
  Refine = true
  Shapes = -> [Cylinder1159,Cylinder1157,Cylinder1158,Cylinder1156]
FEATURE [Part::Box] Box468  label="Cube694"
  AttacherType = Attacher::AttachEngine3D
  Height = 0.6
  Length = 10.6
  Placement = pos=(181,10,24.25) rot=(0,0,1;0rad)
  Width = 59
FEATURE [Part::Box] Box469  label="Cube695"
  AttacherType = Attacher::AttachEngine3D
  Height = 0.6
  Length = 10.6
  Placement = pos=(181,101,24.25) rot=(0,0,1;0rad)
  Width = 59
FEATURE [Part::Box] Box470  label="Cube696"
  AttacherType = Attacher::AttachEngine3D
  Height = 0.65
  Length = 10.5
  Placement = pos=(181,10,24.25) rot=(0,0,1;0rad)
  Width = 59
FEATURE [Part::Box] Box471  label="Cube697"
  AttacherType = Attacher::AttachEngine3D
  Height = 0.65
  Length = 10.5
  Placement = pos=(181,101,24.25) rot=(0,0,1;0rad)
  Width = 59
FEATURE [Part::MultiFuse] Fusion248002050084
  Placement = pos=(0,0,2) rot=(0,0,1;0rad)
  Refine = true
  Shapes = -> [Box468,Box469]
FEATURE [Part::MultiFuse] Fusion248002050085  label="crane-mount-stabilizer-internal"
  Placement = pos=(3.5,0,2) rot=(0,0,1;0rad)
  Refine = true
  Shapes = -> [Box470,Box471]
FEATURE [Part::MultiFuse] Fusion248002050087
  Refine = true
  Shapes = -> [Cylinder1101,Cylinder1103]
FEATURE [Part::MultiFuse] Fusion248002050088
  Placement = pos=(3.5,0,2) rot=(0,0,1;0rad)
  Refine = true
  Shapes = -> [Fusion248002050048,Fusion248002050053,Fusion248002050054,Fusion248002050055]
FEATURE [Part::MultiFuse] Fusion248002050089
  Placement = pos=(3.5,0,0) rot=(0,0,1;0rad)
  Refine = true
  Shapes = -> [Fusion248002050087,Fusion248002050051,Fusion248002050052,Fusion248002050065,Fusion248002050066]
FEATURE [Part::MultiFuse] Fusion248002050091
  Placement = pos=(1,0,0) rot=(0,0,1;0rad)
  Refine = true
  Shapes = -> [Cut482,Cut481]
FEATURE [Part::MultiFuse] Fusion248002050092
  Refine = true
  Shapes = -> [Cylinder1137,Cylinder1138]
FEATURE [Part::MultiFuse] Fusion248002050093
  Placement = pos=(0,0,2) rot=(0,0,1;0rad)
  Refine = true
  Shapes = -> [Fusion248002050092,Fusion248002050073,Fusion248002050072,Fusion248002050070,Fusion248002050069]
FEATURE [Part::MultiFuse] Fusion248002050094
  Refine = true
  Shapes = -> [Fusion248002050058,Fusion248002050050,Fusion248002050059,Fusion248002050057]
FEATURE [Part::Chamfer] Chamfer112
  Base = -> Fusion248002050094
  Edges = 8 edges r=1.5: [Edge1,Edge4,Edge7,Edge10,Edge13,Edge16,Edge19,Edge22]
  Placement = pos=(0,0,2) rot=(0,0,1;0rad)
FEATURE [Part::MultiFuse] Fusion248002050095
  Refine = true
  Shapes = -> [Cut477,Chamfer112]
FEATURE [Part::Cut] Cut486
  Base = -> Fusion248002050095
  Refine = true
  Tool = -> Fusion248002050093
FEATURE [Part::MultiFuse] Fusion248002050096
  Refine = true
  Shapes = -> [Cut486,Fusion248002050091]
FEATURE [Part::Box] Box472  label="Cube698"
  AttacherType = Attacher::AttachEngine3D
  Height = 5
  Length = 10
  Placement = pos=(185,71.5,7) rot=(0,0,1;0rad)
  Width = 2
FEATURE [Part::Box] Box473  label="Cube699"
  AttacherType = Attacher::AttachEngine3D
  Height = 5
  Length = 10
  Placement = pos=(185,96.5,17) rot=(0,0,1;0rad)
  Width = 2
FEATURE [Part::MultiFuse] Fusion248002050097
  Refine = true
  Shapes = -> [Box472,Box473]
FEATURE [Part::Box] Box474  label="Cube700"
  AttacherType = Attacher::AttachEngine3D
  Height = 50
  Length = 35
  Placement = pos=(150,100,31) rot=(0,0,1;0rad)
  Width = 65
FEATURE [Part::Cylinder] Cylinder1160  label="Cylinder1479"
  Angle = 360
  AttacherType = Attacher::AttachEngine3D
  Height = 10
  Placement = pos=(164,113,18) rot=(1,0,0;1.5708rad)
  Radius = 1.25
FEATURE [Part::Cylinder] Cylinder1161  label="Cylinder1480"
  Angle = 360
  AttacherType = Attacher::AttachEngine3D
  Height = 10
  Placement = pos=(164,113,7) rot=(1,0,0;1.5708rad)
  Radius = 1.25
FEATURE [Part::MultiFuse] Fusion248002050098
  Placement = pos=(5,0,2) rot=(0,0,1;0rad)
  Refine = true
  Shapes = -> [Cylinder1160,Cylinder1161]
FEATURE [Part::Fillet] Fillet279
  Base = -> Fusion248002050097
  Edges = 8 edges r=0.8: [Edge9,Edge10,Edge11,Edge12,Edge21,Edge22,Edge23,Edge24]
  Placement = pos=(0,0,2) rot=(0,0,1;0rad)
FEATURE [Part::Box] Box475  label="Cube701"
  AttacherType = Attacher::AttachEngine3D
  Height = 47
  Length = 32
  Placement = pos=(151.5,104.5,32.5) rot=(0,0,1;0rad)
  Width = 63.5
FEATURE [Part::Fillet] Fillet280
  Base = -> Box474
  Edges = 4 edges r=5: [Edge2,Edge4,Edge6,Edge8]
FEATURE [Part::Fillet] Fillet281
  Base = -> Box475
  Edges = 4 edges r=3: [Edge2,Edge4,Edge6,Edge8]
  Placement = pos=(0,-6,0) rot=(0,0,1;0rad)
FEATURE [Part::Box] Box476  label="Cube702"
  AttacherType = Attacher::AttachEngine3D
  Height = 48
  Length = 33
  Placement = pos=(151,104,32) rot=(0,0,1;0rad)
  Width = 1
FEATURE [Part::Fillet] Fillet282
  Base = -> Box476
  Edges = 4 edges r=4: [Edge2,Edge4,Edge6,Edge8]
  Placement = pos=(0,60,0) rot=(0,0,1;0rad)
FEATURE [Part::Cut] Cut491
  Base = -> Fillet280
  Refine = true
  Tool = -> Fillet282
FEATURE [Part::Cut] Cut492
  Base = -> Cut491
  Placement = pos=(11.5,0,0) rot=(0,0,1;0rad)
  Refine = true
  Tool = -> Fillet281
FEATURE [Part::Cylinder] Cylinder971  label="Cylinder1022"
  Angle = 360
  AttacherType = Attacher::AttachEngine3D
  Height = 2
  Placement = pos=(235,162,0) rot=(0,0,1;0rad)
  Radius = 4
FEATURE [Part::Cylinder] Cylinder972  label="Cylinder1023"
  Angle = 360
  AttacherType = Attacher::AttachEngine3D
  Height = 3
  Placement = pos=(235,162,-1) rot=(0,0,1;0rad)
  Radius = 3
FEATURE [Part::MultiFuse] Fusion630
  Refine = true
  Shapes = -> [Cylinder971,Cylinder972]
FEATURE [Part::Fillet] Fillet391
  Base = -> Fusion630
  Edges = 2 edges r=0.5: [Edge1,Edge3]
  Placement = pos=(-63.5,-5,81.5) rot=(0,0,1;0rad)
FEATURE [Part::Cylinder] Cylinder1162  label="Cylinder1481"
  Angle = 360
  AttacherType = Attacher::AttachEngine3D
  Height = 10
  Placement = pos=(145,61,2) rot=(0,0,1;0rad)
  Radius = 1.25
FEATURE [Part::Cylinder] Cylinder1163  label="Cylinder1482"
  Angle = 360
  AttacherType = Attacher::AttachEngine3D
  Height = 10
  Placement = pos=(145,109,2) rot=(0,0,1;0rad)
  Radius = 1.25
FEATURE [Part::MultiFuse] Fusion248002050099
  Refine = true
  Shapes = -> [Cylinder1163,Cylinder1162]
FEATURE [Part::Cylinder] Cylinder1164  label="Cylinder1483"
  Angle = 360
  AttacherType = Attacher::AttachEngine3D
  Height = 10
  Placement = pos=(145,61,2) rot=(0,0,1;0rad)
  Radius = 1.25
FEATURE [Part::Cylinder] Cylinder1165  label="Cylinder1484"
  Angle = 360
  AttacherType = Attacher::AttachEngine3D
  Height = 10
  Placement = pos=(145,109,2) rot=(0,0,1;0rad)
  Radius = 1.25
FEATURE [Part::MultiFuse] Fusion248002050100
  Placement = pos=(54.25,0,0) rot=(0,0,1;0rad)
  Refine = true
  Shapes = -> [Cylinder1165,Cylinder1164]
FEATURE [Part::MultiFuse] Fusion248002050101
  Placement = pos=(0,0,-5) rot=(0,0,1;0rad)
  Refine = true
  Shapes = -> [Fusion248002050099,Fusion248002050100]
FEATURE [Part::Box] Box477  label="Cube703"
  AttacherType = Attacher::AttachEngine3D
  Height = 2
  Length = 62
  Placement = pos=(141,57,2) rot=(0,0,1;0rad)
  Width = 10
FEATURE [Part::Box] Box478  label="Cube704"
  AttacherType = Attacher::AttachEngine3D
  Height = 2
  Length = 62
  Placement = pos=(141,103,2) rot=(0,0,1;0rad)
  Width = 10
FEATURE [Part::Box] Box479  label="Cube705"
  AttacherType = Attacher::AttachEngine3D
  Height = 2
  Length = 8
  Placement = pos=(141,57,2) rot=(0,0,1;0rad)
  Width = 56
FEATURE [Part::Box] Box480  label="Cube706"
  AttacherType = Attacher::AttachEngine3D
  Height = 2
  Length = 8
  Placement = pos=(195,57,2) rot=(0,0,1;0rad)
  Width = 56
FEATURE [Part::Box] Box481  label="Cube707"
  AttacherType = Attacher::AttachEngine3D
  Height = 2
  Length = 62
  Placement = pos=(141,65,0.5) rot=(0,0,1;0rad)
  Width = 2
FEATURE [Part::Box] Box482  label="Cube708"
  AttacherType = Attacher::AttachEngine3D
  Height = 2
  Length = 62
  Placement = pos=(141,103,0.5) rot=(0,0,1;0rad)
  Width = 2
FEATURE [Part::MultiFuse] Fusion248002050102
  Refine = true
  Shapes = -> [Box477,Box478,Box481,Box482,Box480,Box479]
FEATURE [Part::Cut] Cut493  label="crane-mount-main-HOLES"
  Base = -> Fusion248002050102
  Placement = pos=(4.5,0,0) rot=(0,0,1;0rad)
  Refine = true
  Tool = -> Fusion248002050101
FEATURE [Part::Cylinder] Cylinder1168  label="Cylinder1485"
  Angle = 360
  AttacherType = Attacher::AttachEngine3D
  Height = 76
  Placement = pos=(138,107,29.5) rot=(1,0,0;1.5708rad)
  Radius = 4.9
FEATURE [Part::Box] Box483  label="Cube709"
  AttacherType = Attacher::AttachEngine3D
  Height = 14
  Length = 14
  Placement = pos=(140.75,-5,22.5) rot=(0,0,1;0rad)
  Width = 180
FEATURE [Part::Cut] Cut387  label="air-intake-upper-01"
  Placement = pos=(0,0,3) rot=(0,0,1;0rad)
  Refine = true
FEATURE [Part::Cut] Cut014234  label="air-intake-lower-03"
  Refine = true
FEATURE [App::DocumentObjectGroup] Group  label="truck"
  Group = -> [Part__Mirroring018,Fusion138,Fusion231,Fusion654001,Chamfer108,Fusion248002050001,Cut397,Cut398,Fusion281001,Fusion248002049,Cut387,Cut014234]
FEATURE [Part::Cylinder] Cylinder1169  label="Cylinder1486"
  Angle = 360
  AttacherType = Attacher::AttachEngine3D
  Height = 50
  Placement = pos=(175,72.5,17) rot=(0,0,1;0rad)
  Radius = 2.5
FEATURE [Part::Box] Box485  label="Cube711"
  AttacherType = Attacher::AttachEngine3D
  Height = 3
  Length = 4
  Placement = pos=(169.5,60.5,179) rot=(0,0,1;0rad)
  Width = 24
FEATURE [Part::Cylinder] Cylinder1170  label="Cylinder1487"
  Angle = 360
  AttacherType = Attacher::AttachEngine3D
  Height = 10
  Placement = pos=(-7,3,30) rot=(0,0,1;0rad)
  Radius = 1
FEATURE [Part::Cylinder] Cylinder1171  label="Cylinder1488"
  Angle = 360
  AttacherType = Attacher::AttachEngine3D
  Height = 10
  Placement = pos=(-7,22,30) rot=(0,0,1;0rad)
  Radius = 1
FEATURE [Part::MultiFuse] Fusion248002050103
  Placement = pos=(178.5,60,147) rot=(0,0,1;0rad)
  Refine = true
  Shapes = -> [Cylinder1171,Cylinder1170]
FEATURE [Part::Cut] Cut014235
  Base = -> Box485
  Refine = true
  Tool = -> Fusion248002050103
FEATURE [Part::Cylinder] Cylinder1172  label="Cylinder1489"
  Angle = 360
  AttacherType = Attacher::AttachEngine3D
  Height = 4
  Placement = pos=(165,64,180) rot=(0,1,0;1.5708rad)
  Radius = 0.9
FEATURE [Part::Box] Box486  label="Cube712"
  AttacherType = Attacher::AttachEngine3D
  Height = 1
  Length = 4
  Placement = pos=(165,63.1,179) rot=(0,0,1;0rad)
  Width = 1.8
FEATURE [Part::MultiFuse] Fusion248002050104
  Refine = true
  Shapes = -> [Box486,Cylinder1172]
FEATURE [Part::Cylinder] Cylinder1173  label="Cylinder1490"
  Angle = 360
  AttacherType = Attacher::AttachEngine3D
  Height = 4
  Placement = pos=(165,64,180) rot=(0,1,0;1.5708rad)
  Radius = 0.9
FEATURE [Part::Box] Box487  label="Cube713"
  AttacherType = Attacher::AttachEngine3D
  Height = 1
  Length = 4
  Placement = pos=(165,63.1,179) rot=(0,0,1;0rad)
  Width = 1.8
FEATURE [Part::MultiFuse] Fusion248002050105
  Placement = pos=(0,2.5,0) rot=(0,0,1;0rad)
  Refine = true
  Shapes = -> [Box487,Cylinder1173]
FEATURE [Part::Cylinder] Cylinder1174  label="Cylinder1491"
  Angle = 360
  AttacherType = Attacher::AttachEngine3D
  Height = 4
  Placement = pos=(165,64,180) rot=(0,1,0;1.5708rad)
  Radius = 0.9
FEATURE [Part::Box] Box488  label="Cube714"
  AttacherType = Attacher::AttachEngine3D
  Height = 1
  Length = 4
  Placement = pos=(165,63.1,179) rot=(0,0,1;0rad)
  Width = 1.8
FEATURE [Part::MultiFuse] Fusion248002050106
  Placement = pos=(0,5,0) rot=(0,0,1;0rad)
  Refine = true
  Shapes = -> [Box488,Cylinder1174]
FEATURE [Part::Cylinder] Cylinder1175  label="Cylinder1492"
  Angle = 360
  AttacherType = Attacher::AttachEngine3D
  Height = 4
  Placement = pos=(165,64,180) rot=(0,1,0;1.5708rad)
  Radius = 0.9
FEATURE [Part::Box] Box489  label="Cube715"
  AttacherType = Attacher::AttachEngine3D
  Height = 1
  Length = 4
  Placement = pos=(165,63.1,179) rot=(0,0,1;0rad)
  Width = 1.8
FEATURE [Part::MultiFuse] Fusion248002050107
  Placement = pos=(0,7.5,0) rot=(0,0,1;0rad)
  Refine = true
  Shapes = -> [Box489,Cylinder1175]
FEATURE [Part::Cylinder] Cylinder1176  label="Cylinder1493"
  Angle = 360
  AttacherType = Attacher::AttachEngine3D
  Height = 4
  Placement = pos=(165,64,180) rot=(0,1,0;1.5708rad)
  Radius = 0.9
FEATURE [Part::Box] Box490  label="Cube716"
  AttacherType = Attacher::AttachEngine3D
  Height = 1
  Length = 4
  Placement = pos=(165,63.1,179) rot=(0,0,1;0rad)
  Width = 1.8
FEATURE [Part::MultiFuse] Fusion248002050108
  Placement = pos=(0,10,0) rot=(0,0,1;0rad)
  Refine = true
  Shapes = -> [Box490,Cylinder1176]
FEATURE [Part::Cylinder] Cylinder1177  label="Cylinder1494"
  Angle = 360
  AttacherType = Attacher::AttachEngine3D
  Height = 4
  Placement = pos=(165,64,180) rot=(0,1,0;1.5708rad)
  Radius = 0.9
FEATURE [Part::Box] Box491  label="Cube717"
  AttacherType = Attacher::AttachEngine3D
  Height = 1
  Length = 4
  Placement = pos=(165,63.1,179) rot=(0,0,1;0rad)
  Width = 1.8
FEATURE [Part::MultiFuse] Fusion248002050109
  Placement = pos=(0,12.5,0) rot=(0,0,1;0rad)
  Refine = true
  Shapes = -> [Box491,Cylinder1177]
FEATURE [Part::MultiFuse] Fusion248002050110
  Placement = pos=(4.5,2.25,0) rot=(0,0,1;0rad)
  Refine = true
  Shapes = -> [Fusion248002050104,Fusion248002050105,Fusion248002050106,Fusion248002050109,Fusion248002050107,Fusion248002050108]
FEATURE [Part::Box] Box492  label="Cube718"
  AttacherType = Attacher::AttachEngine3D
  Height = 3
  Length = 4
  Placement = pos=(169.5,60.5,179) rot=(0,0,1;0rad)
  Width = 24
FEATURE [Part::Cylinder] Cylinder1178  label="Cylinder1495"
  Angle = 360
  AttacherType = Attacher::AttachEngine3D
  Height = 10
  Placement = pos=(-7,3,30) rot=(0,0,1;0rad)
  Radius = 1
FEATURE [Part::Cylinder] Cylinder1179  label="Cylinder1496"
  Angle = 360
  AttacherType = Attacher::AttachEngine3D
  Height = 10
  Placement = pos=(-7,22,30) rot=(0,0,1;0rad)
  Radius = 1
FEATURE [Part::MultiFuse] Fusion248002050111
  Placement = pos=(178.5,60,147) rot=(0,0,1;0rad)
  Refine = true
  Shapes = -> [Cylinder1179,Cylinder1178]
FEATURE [Part::Cut] Cut014237
  Base = -> Box492
  Refine = true
  Tool = -> Fusion248002050111
FEATURE [Part::Cylinder] Cylinder1180  label="Cylinder1497"
  Angle = 360
  AttacherType = Attacher::AttachEngine3D
  Height = 4
  Placement = pos=(165,64,180) rot=(0,1,0;1.5708rad)
  Radius = 0.9
FEATURE [Part::Box] Box493  label="Cube719"
  AttacherType = Attacher::AttachEngine3D
  Height = 1
  Length = 4
  Placement = pos=(165,63.1,179) rot=(0,0,1;0rad)
  Width = 1.8
FEATURE [Part::MultiFuse] Fusion248002050112
  Refine = true
  Shapes = -> [Box493,Cylinder1180]
FEATURE [Part::Cylinder] Cylinder1181  label="Cylinder1498"
  Angle = 360
  AttacherType = Attacher::AttachEngine3D
  Height = 4
  Placement = pos=(165,64,180) rot=(0,1,0;1.5708rad)
  Radius = 0.9
FEATURE [Part::Box] Box494  label="Cube720"
  AttacherType = Attacher::AttachEngine3D
  Height = 1
  Length = 4
  Placement = pos=(165,63.1,179) rot=(0,0,1;0rad)
  Width = 1.8
FEATURE [Part::MultiFuse] Fusion248002050113
  Placement = pos=(0,2.25,0) rot=(0,0,1;0rad)
  Refine = true
  Shapes = -> [Box494,Cylinder1181]
FEATURE [Part::Cylinder] Cylinder1182  label="Cylinder1499"
  Angle = 360
  AttacherType = Attacher::AttachEngine3D
  Height = 4
  Placement = pos=(165,64,180) rot=(0,1,0;1.5708rad)
  Radius = 0.9
FEATURE [Part::Box] Box495  label="Cube721"
  AttacherType = Attacher::AttachEngine3D
  Height = 1
  Length = 4
  Placement = pos=(165,63.1,179) rot=(0,0,1;0rad)
  Width = 1.8
FEATURE [Part::MultiFuse] Fusion248002050114
  Placement = pos=(0,4.5,0) rot=(0,0,1;0rad)
  Refine = true
  Shapes = -> [Box495,Cylinder1182]
FEATURE [Part::Cylinder] Cylinder1183  label="Cylinder1500"
  Angle = 360
  AttacherType = Attacher::AttachEngine3D
  Height = 4
  Placement = pos=(165,64,180) rot=(0,1,0;1.5708rad)
  Radius = 0.9
FEATURE [Part::Box] Box496  label="Cube722"
  AttacherType = Attacher::AttachEngine3D
  Height = 1
  Length = 4
  Placement = pos=(165,63.1,179) rot=(0,0,1;0rad)
  Width = 1.8
FEATURE [Part::MultiFuse] Fusion248002050115
  Placement = pos=(0,9,0) rot=(0,0,1;0rad)
  Refine = true
  Shapes = -> [Box496,Cylinder1183]
FEATURE [Part::Cylinder] Cylinder1184  label="Cylinder1501"
  Angle = 360
  AttacherType = Attacher::AttachEngine3D
  Height = 4
  Placement = pos=(165,64,180) rot=(0,1,0;1.5708rad)
  Radius = 0.9
FEATURE [Part::Box] Box497  label="Cube723"
  AttacherType = Attacher::AttachEngine3D
  Height = 1
  Length = 4
  Placement = pos=(165,63.1,179) rot=(0,0,1;0rad)
  Width = 1.8
FEATURE [Part::MultiFuse] Fusion248002050116
  Placement = pos=(0,11.25,0) rot=(0,0,1;0rad)
  Refine = true
  Shapes = -> [Box497,Cylinder1184]
FEATURE [Part::Cylinder] Cylinder1185  label="Cylinder1502"
  Angle = 360
  AttacherType = Attacher::AttachEngine3D
  Height = 4
  Placement = pos=(165,64,180) rot=(0,1,0;1.5708rad)
  Radius = 0.9
FEATURE [Part::Box] Box498  label="Cube724"
  AttacherType = Attacher::AttachEngine3D
  Height = 1
  Length = 4
  Placement = pos=(165,63.1,179) rot=(0,0,1;0rad)
  Width = 1.8
FEATURE [Part::MultiFuse] Fusion248002050117
  Placement = pos=(0,6.75,0) rot=(0,0,1;0rad)
  Refine = true
  Shapes = -> [Box498,Cylinder1185]
FEATURE [Part::Cylinder] Cylinder1186  label="Cylinder1503"
  Angle = 360
  AttacherType = Attacher::AttachEngine3D
  Height = 4
  Placement = pos=(165,64,180) rot=(0,1,0;1.5708rad)
  Radius = 0.9
FEATURE [Part::Box] Box499  label="Cube725"
  AttacherType = Attacher::AttachEngine3D
  Height = 1
  Length = 4
  Placement = pos=(165,63.1,179) rot=(0,0,1;0rad)
  Width = 1.8
FEATURE [Part::MultiFuse] Fusion248002050118
  Placement = pos=(0,13.5,0) rot=(0,0,1;0rad)
  Refine = true
  Shapes = -> [Box499,Cylinder1186]
FEATURE [Part::Cylinder] Cylinder1187  label="Cylinder1504"
  Angle = 360
  AttacherType = Attacher::AttachEngine3D
  Height = 4
  Placement = pos=(165,64,180) rot=(0,1,0;1.5708rad)
  Radius = 0.9
FEATURE [Part::Box] Box500  label="Cube726"
  AttacherType = Attacher::AttachEngine3D
  Height = 1
  Length = 4
  Placement = pos=(165,63.1,179) rot=(0,0,1;0rad)
  Width = 1.8
FEATURE [Part::MultiFuse] Fusion248002050119
  Placement = pos=(0,15.75,0) rot=(0,0,1;0rad)
  Refine = true
  Shapes = -> [Box500,Cylinder1187]
FEATURE [Part::MultiFuse] Fusion248002050120
  Placement = pos=(4.5,0.6,0) rot=(0,0,1;0rad)
  Refine = true
  Shapes = -> [Fusion248002050112,Fusion248002050118,Fusion248002050119,Fusion248002050116,Fusion248002050114,Fusion248002050117,Fusion248002050113,Fusion248002050115]
FEATURE [Part::Cylinder] Cylinder1189  label="Cylinder1505"
  Angle = 360
  AttacherType = Attacher::AttachEngine3D
  Height = 27
  Radius = 8
FEATURE [Part::Box] Box501  label="Cube727"
  AttacherType = Attacher::AttachEngine3D
  Height = 27
  Length = 10.4
  Placement = pos=(-5.2,-6.2,0) rot=(0,0,1;0rad)
  Width = 12.4
FEATURE [Part::Cylinder] Cylinder1190  label="Cylinder1506"
  Angle = 360
  AttacherType = Attacher::AttachEngine3D
  Height = 17
  Radius = 8
FEATURE [Part::Cylinder] Cylinder1191  label="Cylinder1507"
  Angle = 360
  AttacherType = Attacher::AttachEngine3D
  Height = 17
  Radius = 6.5
FEATURE [Part::Cut] Cut014239
  Base = -> Cylinder1190
  Refine = true
  Tool = -> Cylinder1191
FEATURE [Part::Fillet] Fillet395
  Base = -> Box501
  Edges = 4 edges r=1: [Edge1,Edge3,Edge5,Edge7]
FEATURE [Part::Cut] Cut014240
  Base = -> Cylinder1189
  Refine = true
  Tool = -> Fillet395
FEATURE [Part::MultiFuse] Fusion248002050121
  Refine = true
  Shapes = -> [Cut014239,Cut014240]
FEATURE [Part::Cylinder] Cylinder1192  label="Cylinder1508"
  Angle = 360
  AttacherType = Attacher::AttachEngine3D
  Height = 27
  Radius = 8
FEATURE [Part::Cut] Cut014241  label="cylinder-motor-supports-003"
  Base = -> Cylinder1192
  Placement = pos=(175,76,18) rot=(1,0,0;1.5708rad)
  Refine = true
  Tool = -> Fusion248002050121
FEATURE [Part::Cylinder] Cylinder1193  label="Cylinder1509"
  Angle = 360
  AttacherType = Attacher::AttachEngine3D
  Height = 150
  Placement = pos=(175,49,18) rot=(1,0,0;1.5708rad)
  Radius = 2.5
FEATURE [Part::Fillet] Fillet396
  Base = -> Cut014237
  Edges = 4 edges r=1.99: [Edge1,Edge3,Edge6,Edge13]
FEATURE [Part::Fillet] Fillet397
  Base = -> Cut014235
  Edges = 4 edges r=1.99: [Edge1,Edge3,Edge6,Edge13]
FEATURE [Part::Cut] Cut014244  label="crane-secondary-arm-wires-holder"
  Base = -> Fillet397
  Placement = pos=(7.5,0,2) rot=(0,0,1;0rad)
  Refine = true
  Tool = -> Fusion248002050110
FEATURE [App::DocumentObjectGroup] Group002  label="secondary-arm"
  Group = -> [Cut037,Cut038,Fusion081,Fusion083,Cut060,Fusion051,Cut014244]
FEATURE [Part::Cut] Cut014245  label="crane-main-arm-wires-holder"
  Base = -> Fillet396
  Placement = pos=(348,0,17) rot=(0,-1,0;1.76278rad)
  Refine = true
  Tool = -> Fusion248002050120
FEATURE [App::DocumentObjectGroup] Group001  label="main-arm"
  Group = -> [Fusion044,Cut085,Fusion080,Fusion082,Cut464,Cylinder198,Cylinder210,Cut014245,Cylinder1169]
FEATURE [Part::Cylinder] Cylinder1194  label="Cylinder1510"
  Angle = 360
  AttacherType = Attacher::AttachEngine3D
  Height = 5
  Placement = pos=(171.5,72.5,23) rot=(0,0,1;0rad)
  Radius = 8.2
FEATURE [Part::Cylinder] Cylinder1195  label="Cylinder1511"
  Angle = 360
  AttacherType = Attacher::AttachEngine3D
  Height = 7
  Placement = pos=(175,72.5,2) rot=(0,0,1;0rad)
  Radius = 6.75
FEATURE [Part::MultiFuse] Fusion248002050123
  Refine = true
  Shapes = -> [Box461,Box463]
FEATURE [Part::Cut] Cut014248
  Base = -> Fusion248002050123
  Refine = true
  Tool = -> Cylinder1102
FEATURE [Part::MultiFuse] Fusion248002050124
  Refine = true
  Shapes = -> [Cut014248,Fusion248002050088]
FEATURE [Part::Cut] Cut014249
  Base = -> Fusion248002050124
  Refine = true
  Tool = -> Fusion248002050089
FEATURE [Part::Cut] Cut014250  label="crane-mount-stabilizer-base"
  Base = -> Cut014249
  Refine = true
  Tool = -> Cylinder1195
FEATURE [Part::Cylinder] Cylinder1196  label="Cylinder1512"
  Angle = 360
  AttacherType = Attacher::AttachEngine3D
  Height = 10
  Placement = pos=(161,113,24) rot=(1,0,0;1.5708rad)
  Radius = 1.25
FEATURE [Part::Cylinder] Cylinder1197  label="Cylinder1513"
  Angle = 360
  AttacherType = Attacher::AttachEngine3D
  Height = 10
  Placement = pos=(161,67,24) rot=(1,0,0;1.5708rad)
  Radius = 1.25
FEATURE [Part::MultiFuse] Fusion248002050126
  Refine = true
  Shapes = -> [Cylinder1197,Cylinder1196]
FEATURE [Part::Box] Box502  label="Cube728"
  AttacherType = Attacher::AttachEngine3D
  Height = 13
  Length = 3.5
  Placement = pos=(188.25,65,5) rot=(0,0,1;0rad)
  Width = 10
FEATURE [Part::Cylinder] Cylinder1198  label="Cylinder1514"
  Angle = 360
  AttacherType = Attacher::AttachEngine3D
  Height = 150
  Placement = pos=(151.5,-4,31.5) rot=(-1,0,0;1.5708rad)
  Radius = 6
FEATURE [Part::Cylinder] Cylinder1199  label="Cylinder1515"
  Angle = 360
  AttacherType = Attacher::AttachEngine3D
  Height = 180
  Placement = pos=(151.5,175,31.5) rot=(1,0,0;1.5708rad)
  Radius = 5
FEATURE [Part::Cut] Cut014254
  Base = -> Cylinder1198
  Placement = pos=(0.5,0,0) rot=(0,0,1;0rad)
  Refine = true
  Tool = -> Cylinder1199
FEATURE [Part::Cut] Cut495
  Base = -> Cylinder1168
  Placement = pos=(14,0,2) rot=(0,0,1;0rad)
  Refine = true
  Tool = -> Box483
FEATURE [Part::Box] Box503  label="Cube729"
  AttacherType = Attacher::AttachEngine3D
  Height = 10
  Length = 14
  Placement = pos=(155,42,27.5) rot=(0,0,1;0rad)
  Width = 60
FEATURE [Part::Fillet] Fillet398
  Base = -> Box503
  Edges = 2 edges r=4: [Edge1,Edge3]
  Placement = pos=(-0.25,0,0) rot=(0,0,1;0rad)
FEATURE [Part::Cut] Cut014255  label="crane-rotating-cylinder"
  Base = -> Cut014254
  Placement = pos=(0,-2,0) rot=(0,0,1;0rad)
  Refine = true
  Tool = -> Fillet398
FEATURE [Part::Cylinder] Cylinder1200  label="Cylinder1516"
  Angle = 360
  AttacherType = Attacher::AttachEngine3D
  Height = 180
  Placement = pos=(151.5,175,31.5) rot=(1,0,0;1.5708rad)
  Radius = 8
FEATURE [Part::Cylinder] Cylinder1201  label="Cylinder1517"
  Angle = 360
  AttacherType = Attacher::AttachEngine3D
  Height = 180
  Placement = pos=(151.5,175,31.5) rot=(1,0,0;1.5708rad)
  Radius = 4.9
FEATURE [Part::Cut] Cut014256
  Base = -> Cylinder1200
  Placement = pos=(0.5,0,0) rot=(0,0,1;0rad)
  Refine = true
  Tool = -> Cylinder1201
FEATURE [Part::Cut] Cut014257
  Base = -> Fusion248002050008
  Refine = true
  Tool = -> Cut014256
FEATURE [Part::MultiFuse] Fusion248002050127  label="crane-rotating-cylinder-motor"
  Placement = pos=(-23,98,13.5) rot=(0,0,1;0rad)
  Refine = true
  Shapes = -> [Cut014241,Cylinder1193]
FEATURE [Part::MultiFuse] Fusion248002050128
  Refine = true
  Shapes = -> [Cut495,Cut014257]
FEATURE [Part::Cylinder] Cylinder1202  label="Cylinder1518"
  Angle = 360
  AttacherType = Attacher::AttachEngine3D
  Height = 150
  Placement = pos=(152,153,31.5) rot=(1,0,0;1.5708rad)
  Radius = 2.6
FEATURE [Part::Cut] Cut014258
  Base = -> Fusion248002050128
  Refine = true
  Tool = -> Cylinder1202
FEATURE [Part::Box] Box504  label="Cube730"
  AttacherType = Attacher::AttachEngine3D
  Height = 14
  Length = 14
  Placement = pos=(143.75,-5,13.5) rot=(0,0,1;0rad)
  Width = 180
FEATURE [Part::Cut] Cut014259  label="crane-rotating-cylinder-rack"
  Base = -> Cut014258
  Refine = true
  Tool = -> Box504
FEATURE [Part::Box] Box505  label="Cube731"
  AttacherType = Attacher::AttachEngine3D
  Height = 20
  Length = 18
  Placement = pos=(143,52,19) rot=(0,0,1;0rad)
  Width = 5
FEATURE [Part::Box] Box506  label="Cube732"
  AttacherType = Attacher::AttachEngine3D
  Height = 10
  Length = 4
  Placement = pos=(150.5,52,17) rot=(0,0,1;0rad)
  Width = 11
FEATURE [Part::Box] Box507  label="Cube733"
  AttacherType = Attacher::AttachEngine3D
  Height = 11
  Length = 18
  Placement = pos=(150.5,52,17) rot=(0,0,1;0rad)
  Width = 5
FEATURE [Part::MultiFuse] Fusion248002050129
  Refine = true
  Shapes = -> [Box505,Box506,Box507]
FEATURE [Part::Cylinder] Cylinder1203  label="Cylinder1519"
  Angle = 360
  AttacherType = Attacher::AttachEngine3D
  Height = 20
  Placement = pos=(152,46,31.5) rot=(-1,0,0;1.5708rad)
  Radius = 6
FEATURE [Part::Cut] Cut014260
  Base = -> Fusion248002050129
  Refine = true
  Tool = -> Cylinder1203
FEATURE [Part::Fillet] Fillet399
  Base = -> Cut014260
  Edges = 2 edges r=5: [Edge34,Edge35]
FEATURE [Part::Cylinder] Cylinder1204  label="Cylinder1520"
  Angle = 360
  AttacherType = Attacher::AttachEngine3D
  Height = 10
  Placement = pos=(150,60,21) rot=(0,1,0;1.5708rad)
  Radius = 1.6
FEATURE [Part::Cylinder] Cylinder1209  label="Cylinder1521"
  Angle = 360
  AttacherType = Attacher::AttachEngine3D
  Height = 10
  Placement = pos=(164.5,62,24) rot=(1,0,0;1.5708rad)
  Radius = 1.6
FEATURE [Part::MultiFuse] Fusion248002050130
  Refine = true
  Shapes = -> [Cylinder1204,Cylinder1209]
FEATURE [Part::Cut] Cut014261
  Base = -> Fillet399
  Refine = true
  Tool = -> Fusion248002050130
FEATURE [Part::Chamfer] Chamfer114
  Base = -> Cut014261
  Edges = 1 edges r=7.49: [Edge33]
FEATURE [Part::Fillet] Fillet400
  Base = -> Chamfer114
  Edges = 1 edges r=10: [Edge17]
FEATURE [Part::Chamfer] Chamfer115
  Base = -> Fillet400
  Edges = 1 edges r=1.99: [Edge33]
FEATURE [Part::Cylinder] Cylinder1213  label="Cylinder1522"
  Angle = 360
  AttacherType = Attacher::AttachEngine3D
  Height = 10
  Placement = pos=(143,54.5,32) rot=(0,1,0;1.5708rad)
  Radius = 1.25
FEATURE [Part::Cut] Cut014262
  Base = -> Chamfer115
  Refine = true
  Tool = -> Cylinder1213
FEATURE [Part::Chamfer] Chamfer116  label="crane-rotating-cylinder-holder-left_"
  Base = -> Cut014262
  Edges = 1 edges r=5: [Edge49]
FEATURE [Part::Box] Box508  label="Cube734"
  AttacherType = Attacher::AttachEngine3D
  Height = 20
  Length = 18
  Placement = pos=(143,52,19) rot=(0,0,1;0rad)
  Width = 5
FEATURE [Part::Box] Box509  label="Cube735"
  AttacherType = Attacher::AttachEngine3D
  Height = 10
  Length = 4
  Placement = pos=(150.5,52,17) rot=(0,0,1;0rad)
  Width = 11
FEATURE [Part::Box] Box510  label="Cube736"
  AttacherType = Attacher::AttachEngine3D
  Height = 11
  Length = 18
  Placement = pos=(150.5,52,17) rot=(0,0,1;0rad)
  Width = 5
FEATURE [Part::MultiFuse] Fusion248002050131
  Refine = true
  Shapes = -> [Box508,Box509,Box510]
FEATURE [Part::Cylinder] Cylinder1214  label="Cylinder1523"
  Angle = 360
  AttacherType = Attacher::AttachEngine3D
  Height = 20
  Placement = pos=(152,46,31.5) rot=(-1,0,0;1.5708rad)
  Radius = 6
FEATURE [Part::Cut] Cut014263
  Base = -> Fusion248002050131
  Refine = true
  Tool = -> Cylinder1214
FEATURE [Part::Fillet] Fillet401
  Base = -> Cut014263
  Edges = 2 edges r=5: [Edge34,Edge35]
FEATURE [Part::Cylinder] Cylinder1215  label="Cylinder1524"
  Angle = 360
  AttacherType = Attacher::AttachEngine3D
  Height = 10
  Placement = pos=(150,60,21) rot=(0,1,0;1.5708rad)
  Radius = 1.6
FEATURE [Part::Cylinder] Cylinder1216  label="Cylinder1525"
  Angle = 360
  AttacherType = Attacher::AttachEngine3D
  Height = 10
  Placement = pos=(164.5,62,24) rot=(1,0,0;1.5708rad)
  Radius = 1.6
FEATURE [Part::MultiFuse] Fusion248002050132
  Refine = true
  Shapes = -> [Cylinder1215,Cylinder1216]
FEATURE [Part::Cut] Cut014264
  Base = -> Fillet401
  Refine = true
  Tool = -> Fusion248002050132
FEATURE [Part::Chamfer] Chamfer117
  Base = -> Cut014264
  Edges = 1 edges r=7.49: [Edge33]
FEATURE [Part::Fillet] Fillet402
  Base = -> Chamfer117
  Edges = 1 edges r=10: [Edge17]
FEATURE [Part::Chamfer] Chamfer118
  Base = -> Fillet402
  Edges = 1 edges r=1.99: [Edge33]
FEATURE [Part::Cylinder] Cylinder1217  label="Cylinder1526"
  Angle = 360
  AttacherType = Attacher::AttachEngine3D
  Height = 10
  Placement = pos=(143,54.5,32) rot=(0,1,0;1.5708rad)
  Radius = 1.25
FEATURE [Part::Cut] Cut014265
  Base = -> Chamfer118
  Refine = true
  Tool = -> Cylinder1217
FEATURE [Part::Chamfer] Chamfer119
  Base = -> Cut014265
  Edges = 1 edges r=5: [Edge49]
FEATURE [Part::Mirroring] Part__Mirroring  label="crane-rotating-cylinder-holder-right_"
  Base = (0,0,0)
  Normal = (0,1,0)
  Placement = pos=(0,170,0) rot=(0,0,1;0rad)
  Source = -> Chamfer119
FEATURE [Part::Box] Box517  label="Cube743"
  AttacherType = Attacher::AttachEngine3D
  Height = 15
  Length = 39
  Placement = pos=(306.5,91,180) rot=(0,0,1;0rad)
  Width = 15
FEATURE [Part::Cylinder] Cylinder1235  label="Cylinder1527"
  Angle = 360
  AttacherType = Attacher::AttachEngine3D
  Height = 27
  Radius = 8
FEATURE [Part::Box] Box518  label="Cube744"
  AttacherType = Attacher::AttachEngine3D
  Height = 27
  Length = 10.4
  Placement = pos=(-5.2,-6.2,0) rot=(0,0,1;0rad)
  Width = 12.4
FEATURE [Part::Cylinder] Cylinder1236  label="Cylinder1528"
  Angle = 360
  AttacherType = Attacher::AttachEngine3D
  Height = 17
  Radius = 8
FEATURE [Part::Cylinder] Cylinder1237  label="Cylinder1529"
  Angle = 360
  AttacherType = Attacher::AttachEngine3D
  Height = 17
  Radius = 6.5
FEATURE [Part::Cut] Cut014273
  Base = -> Cylinder1236
  Refine = true
  Tool = -> Cylinder1237
FEATURE [Part::Fillet] Fillet405
  Base = -> Box518
  Edges = 4 edges r=1: [Edge1,Edge3,Edge5,Edge7]
FEATURE [Part::Cut] Cut014274
  Base = -> Cylinder1235
  Refine = true
  Tool = -> Fillet405
FEATURE [Part::MultiFuse] Fusion248002050143
  Refine = true
  Shapes = -> [Cut014273,Cut014274]
FEATURE [Part::Cylinder] Cylinder1238  label="Cylinder1530"
  Angle = 360
  AttacherType = Attacher::AttachEngine3D
  Height = 27
  Radius = 8
FEATURE [Part::Cut] Cut014275  label="cylinder-motor-extender003"
  Base = -> Cylinder1238
  Placement = pos=(309.5,98.5,187.5) rot=(0,1,0;1.5708rad)
  Refine = true
  Tool = -> Fusion248002050143
FEATURE [Part::Cylinder] Cylinder1239  label="Cylinder1531"
  Angle = 360
  AttacherType = Attacher::AttachEngine3D
  Height = 3
  Placement = pos=(333.5,98.5,186.5) rot=(0,1,0;1.5708rad)
  Radius = 5
FEATURE [Part::Cylinder] Cylinder1240  label="Cylinder1532"
  Angle = 360
  AttacherType = Attacher::AttachEngine3D
  Height = 6
  Placement = pos=(336.5,98.5,186.5) rot=(0,1,0;1.5708rad)
  Radius = 6.1
FEATURE [Part::MultiFuse] Fusion248002050144
  Placement = pos=(3,0,1) rot=(0,0,1;0rad)
  Refine = true
  Shapes = -> [Cylinder1239,Cylinder1240]
FEATURE [Part::Cylinder] Cylinder1243  label="Cylinder1533"
  Angle = 360
  AttacherType = Attacher::AttachEngine3D
  Height = 14
  Placement = pos=(184,47,128) rot=(1,0,0;1.5708rad)
  Radius = 1
FEATURE [Part::Cylinder] Cylinder1244  label="Cylinder1534"
  Angle = 360
  AttacherType = Attacher::AttachEngine3D
  Height = 1.6
  Placement = pos=(184,47,128) rot=(1,0,0;1.5708rad)
  Radius = 2.1
FEATURE [Part::MultiFuse] Fusion248002050146
  Placement = pos=(124,59,65) rot=(0,0,1;0rad)
  Refine = true
  Shapes = -> [Cylinder1243,Cylinder1244]
FEATURE [Part::Fillet] Fillet406
  Base = -> Box517
  Edges = 4 edges r=3: [Edge9,Edge10,Edge11,Edge12]
  Placement = pos=(53.5,489,-156) rot=(0,0,-1;1.5708rad)
FEATURE [Part::Cylinder] Cylinder1245  label="Cylinder1535"
  Angle = 360
  AttacherType = Attacher::AttachEngine3D
  Height = 14
  Placement = pos=(184,47,128) rot=(1,0,0;1.5708rad)
  Radius = 1
FEATURE [Part::Cylinder] Cylinder1246  label="Cylinder1536"
  Angle = 360
  AttacherType = Attacher::AttachEngine3D
  Height = 1.6
  Placement = pos=(184,47,128) rot=(1,0,0;1.5708rad)
  Radius = 2.1
FEATURE [Part::MultiFuse] Fusion248002050147
  Placement = pos=(154,59,65) rot=(0,0,1;0rad)
  Refine = true
  Shapes = -> [Cylinder1245,Cylinder1246]
FEATURE [Part::Cylinder] Cylinder1247  label="Cylinder1537"
  Angle = 360
  AttacherType = Attacher::AttachEngine3D
  Height = 14
  Placement = pos=(184,47,128) rot=(1,0,0;1.5708rad)
  Radius = 1
FEATURE [Part::Cylinder] Cylinder1248  label="Cylinder1538"
  Angle = 360
  AttacherType = Attacher::AttachEngine3D
  Height = 1.6
  Placement = pos=(184,47,128) rot=(1,0,0;1.5708rad)
  Radius = 2.1
FEATURE [Part::MultiFuse] Fusion248002050148
  Placement = pos=(124,59,54) rot=(0,0,1;0rad)
  Refine = true
  Shapes = -> [Cylinder1247,Cylinder1248]
FEATURE [Part::Cylinder] Cylinder1249  label="Cylinder1539"
  Angle = 360
  AttacherType = Attacher::AttachEngine3D
  Height = 14
  Placement = pos=(184,47,128) rot=(1,0,0;1.5708rad)
  Radius = 1
FEATURE [Part::Cylinder] Cylinder1250  label="Cylinder1540"
  Angle = 360
  AttacherType = Attacher::AttachEngine3D
  Height = 1.6
  Placement = pos=(184,47,128) rot=(1,0,0;1.5708rad)
  Radius = 2.1
FEATURE [Part::MultiFuse] Fusion248002050149
  Placement = pos=(154,59,54) rot=(0,0,1;0rad)
  Refine = true
  Shapes = -> [Cylinder1249,Cylinder1250]
FEATURE [Part::MultiFuse] Fusion248002050150
  Placement = pos=(0,1,0) rot=(0,0,1;0rad)
  Refine = true
  Shapes = -> [Fusion248002050146,Fusion248002050147,Fusion248002050148,Fusion248002050149]
FEATURE [Part::MultiFuse] Fusion248002050152
  Placement = pos=(53.5,489,-156) rot=(0,0,-1;1.5708rad)
  Refine = true
  Shapes = -> [Cut014275,Fusion248002050144,Fusion248002050150]
FEATURE [Part::Cut] Cut014276
  Base = -> Fillet406
  Placement = pos=(0,-5.5,0) rot=(0,0,1;0rad)
  Refine = true
  Tool = -> Fusion248002050152
FEATURE [Part::Box] Box519  label="Cube745"
  AttacherType = Attacher::AttachEngine3D
  Height = 5
  Length = 2
  Placement = pos=(144,174,29) rot=(0,0,-1;1.5708rad)
  Width = 5
FEATURE [Part::Cut] Cut014277
  Base = -> Cut014276
  Refine = true
  Tool = -> Box519
FEATURE [Part::Box] Box520  label="Cube746"
  AttacherType = Attacher::AttachEngine3D
  Height = 15
  Length = 39
  Placement = pos=(155,138,24) rot=(0,0,1;1.5708rad)
  Width = 10.5
FEATURE [Part::Box] Box521  label="Cube747"
  AttacherType = Attacher::AttachEngine3D
  Height = 15
  Length = 39
  Placement = pos=(165.5,138,24) rot=(0,0,1;1.5708rad)
  Width = 10.5
FEATURE [Part::Box] Box522  label="Cube748"
  AttacherType = Attacher::AttachEngine3D
  Height = 15
  Length = 39
  Placement = pos=(306.5,91,180) rot=(0,0,1;0rad)
  Width = 15
FEATURE [Part::Cylinder] Cylinder1251  label="Cylinder1541"
  Angle = 360
  AttacherType = Attacher::AttachEngine3D
  Height = 27
  Radius = 8
FEATURE [Part::Box] Box523  label="Cube749"
  AttacherType = Attacher::AttachEngine3D
  Height = 27
  Length = 10.4
  Placement = pos=(-5.2,-6.2,0) rot=(0,0,1;0rad)
  Width = 12.4
FEATURE [Part::Cylinder] Cylinder1252  label="Cylinder1542"
  Angle = 360
  AttacherType = Attacher::AttachEngine3D
  Height = 17
  Radius = 8
FEATURE [Part::Cylinder] Cylinder1253  label="Cylinder1543"
  Angle = 360
  AttacherType = Attacher::AttachEngine3D
  Height = 17
  Radius = 6.5
FEATURE [Part::Cut] Cut014278
  Base = -> Cylinder1252
  Refine = true
  Tool = -> Cylinder1253
FEATURE [Part::Fillet] Fillet407
  Base = -> Box523
  Edges = 4 edges r=1: [Edge1,Edge3,Edge5,Edge7]
FEATURE [Part::Cut] Cut014279
  Base = -> Cylinder1251
  Refine = true
  Tool = -> Fillet407
FEATURE [Part::MultiFuse] Fusion248002050153
  Refine = true
  Shapes = -> [Cut014278,Cut014279]
FEATURE [Part::Cylinder] Cylinder1254  label="Cylinder1544"
  Angle = 360
  AttacherType = Attacher::AttachEngine3D
  Height = 27
  Radius = 8
FEATURE [Part::Cut] Cut014280  label="cylinder-motor-extender004"
  Base = -> Cylinder1254
  Placement = pos=(309.5,98.5,187.5) rot=(0,1,0;1.5708rad)
  Refine = true
  Tool = -> Fusion248002050153
FEATURE [Part::Cylinder] Cylinder1255  label="Cylinder1545"
  Angle = 360
  AttacherType = Attacher::AttachEngine3D
  Height = 3
  Placement = pos=(333.5,98.5,186.5) rot=(0,1,0;1.5708rad)
  Radius = 5
FEATURE [Part::Cylinder] Cylinder1256  label="Cylinder1546"
  Angle = 360
  AttacherType = Attacher::AttachEngine3D
  Height = 6
  Placement = pos=(336.5,98.5,186.5) rot=(0,1,0;1.5708rad)
  Radius = 6.1
FEATURE [Part::MultiFuse] Fusion248002050154
  Placement = pos=(3,0,1) rot=(0,0,1;0rad)
  Refine = true
  Shapes = -> [Cylinder1255,Cylinder1256]
FEATURE [Part::Cylinder] Cylinder1257  label="Cylinder1547"
  Angle = 360
  AttacherType = Attacher::AttachEngine3D
  Height = 14
  Placement = pos=(184,47,128) rot=(1,0,0;1.5708rad)
  Radius = 1
FEATURE [Part::Cylinder] Cylinder1258  label="Cylinder1548"
  Angle = 360
  AttacherType = Attacher::AttachEngine3D
  Height = 1.6
  Placement = pos=(184,47,128) rot=(1,0,0;1.5708rad)
  Radius = 2.1
FEATURE [Part::MultiFuse] Fusion248002050155
  Placement = pos=(124,59,65) rot=(0,0,1;0rad)
  Refine = true
  Shapes = -> [Cylinder1257,Cylinder1258]
FEATURE [Part::Fillet] Fillet408
  Base = -> Box522
  Edges = 4 edges r=3: [Edge9,Edge10,Edge11,Edge12]
  Placement = pos=(53.5,489,-156) rot=(0,0,-1;1.5708rad)
FEATURE [Part::Cylinder] Cylinder1259  label="Cylinder1549"
  Angle = 360
  AttacherType = Attacher::AttachEngine3D
  Height = 14
  Placement = pos=(184,47,128) rot=(1,0,0;1.5708rad)
  Radius = 1
FEATURE [Part::Cylinder] Cylinder1260  label="Cylinder1550"
  Angle = 360
  AttacherType = Attacher::AttachEngine3D
  Height = 1.6
  Placement = pos=(184,47,128) rot=(1,0,0;1.5708rad)
  Radius = 2.1
FEATURE [Part::MultiFuse] Fusion248002050156
  Placement = pos=(154,59,65) rot=(0,0,1;0rad)
  Refine = true
  Shapes = -> [Cylinder1259,Cylinder1260]
FEATURE [Part::Cylinder] Cylinder1261  label="Cylinder1551"
  Angle = 360
  AttacherType = Attacher::AttachEngine3D
  Height = 14
  Placement = pos=(184,47,128) rot=(1,0,0;1.5708rad)
  Radius = 1
FEATURE [Part::Cylinder] Cylinder1262  label="Cylinder1552"
  Angle = 360
  AttacherType = Attacher::AttachEngine3D
  Height = 1.6
  Placement = pos=(184,47,128) rot=(1,0,0;1.5708rad)
  Radius = 2.1
FEATURE [Part::MultiFuse] Fusion248002050157
  Placement = pos=(124,59,54) rot=(0,0,1;0rad)
  Refine = true
  Shapes = -> [Cylinder1261,Cylinder1262]
FEATURE [Part::Cylinder] Cylinder1263  label="Cylinder1553"
  Angle = 360
  AttacherType = Attacher::AttachEngine3D
  Height = 14
  Placement = pos=(184,47,128) rot=(1,0,0;1.5708rad)
  Radius = 1
FEATURE [Part::Cylinder] Cylinder1264  label="Cylinder1554"
  Angle = 360
  AttacherType = Attacher::AttachEngine3D
  Height = 1.6
  Placement = pos=(184,47,128) rot=(1,0,0;1.5708rad)
  Radius = 2.1
FEATURE [Part::MultiFuse] Fusion248002050158
  Placement = pos=(154,59,54) rot=(0,0,1;0rad)
  Refine = true
  Shapes = -> [Cylinder1263,Cylinder1264]
FEATURE [Part::MultiFuse] Fusion248002050159
  Placement = pos=(0,1,0) rot=(0,0,1;0rad)
  Refine = true
  Shapes = -> [Fusion248002050155,Fusion248002050156,Fusion248002050157,Fusion248002050158]
FEATURE [Part::MultiFuse] Fusion248002050160
  Placement = pos=(53.5,489,-156) rot=(0,0,-1;1.5708rad)
  Refine = true
  Shapes = -> [Cut014280,Fusion248002050154,Fusion248002050159]
FEATURE [Part::Cut] Cut014281
  Base = -> Fillet408
  Placement = pos=(0,-5.5,0) rot=(0,0,1;0rad)
  Refine = true
  Tool = -> Fusion248002050160
FEATURE [Part::Box] Box524  label="Cube750"
  AttacherType = Attacher::AttachEngine3D
  Height = 5
  Length = 2
  Placement = pos=(144,174,29) rot=(0,0,-1;1.5708rad)
  Width = 5
FEATURE [Part::Cut] Cut014282
  Base = -> Cut014281
  Refine = true
  Tool = -> Box524
FEATURE [Part::Cut] Cut014283  label="rotating-cylinder-motor-holder-rear"
  Base = -> Cut014277
  Refine = true
  Tool = -> Box520
FEATURE [Part::Cut] Cut014284  label="rotating-cylinder-motor-holder-front"
  Base = -> Cut014282
  Refine = true
  Tool = -> Box521
FEATURE [Part::Box] Box525  label="Cube751"
  AttacherType = Attacher::AttachEngine3D
  Height = 29
  Length = 4
  Placement = pos=(324.5,107,152.5) rot=(0,0,1;0rad)
  Width = 3
FEATURE [Part::Cylinder] Cylinder1265  label="Cylinder1555"
  Angle = 360
  AttacherType = Attacher::AttachEngine3D
  Height = 10
  Placement = pos=(326.5,106,154.5) rot=(-1,0,0;1.5708rad)
  Radius = 1
FEATURE [Part::Cylinder] Cylinder1266  label="Cylinder1556"
  Angle = 360
  AttacherType = Attacher::AttachEngine3D
  Height = 10
  Placement = pos=(326.5,106,179.5) rot=(-1,0,0;1.5708rad)
  Radius = 1
FEATURE [Part::Cylinder] Cylinder1269  label="Cylinder1557"
  Angle = 360
  AttacherType = Attacher::AttachEngine3D
  Height = 4
  Placement = pos=(165,64,180) rot=(0,1,0;1.5708rad)
  Radius = 0.9
FEATURE [Part::Box] Box528  label="Cube754"
  AttacherType = Attacher::AttachEngine3D
  Height = 1
  Length = 4
  Placement = pos=(165,63.1,179) rot=(0,0,1;0rad)
  Width = 1.8
FEATURE [Part::MultiFuse] Fusion248002050164
  Placement = pos=(0,5,0) rot=(0,0,1;0rad)
  Refine = true
  Shapes = -> [Box528,Cylinder1269]
FEATURE [Part::Cylinder] Cylinder1270  label="Cylinder1558"
  Angle = 360
  AttacherType = Attacher::AttachEngine3D
  Height = 4
  Placement = pos=(165,64,180) rot=(0,1,0;1.5708rad)
  Radius = 0.9
FEATURE [Part::Box] Box529  label="Cube755"
  AttacherType = Attacher::AttachEngine3D
  Height = 1
  Length = 4
  Placement = pos=(165,63.1,179) rot=(0,0,1;0rad)
  Width = 1.8
FEATURE [Part::MultiFuse] Fusion248002050165
  Placement = pos=(0,7.5,0) rot=(0,0,1;0rad)
  Refine = true
  Shapes = -> [Box529,Cylinder1270]
FEATURE [Part::Cylinder] Cylinder1271  label="Cylinder1559"
  Angle = 360
  AttacherType = Attacher::AttachEngine3D
  Height = 4
  Placement = pos=(165,64,180) rot=(0,1,0;1.5708rad)
  Radius = 0.9
FEATURE [Part::Box] Box530  label="Cube756"
  AttacherType = Attacher::AttachEngine3D
  Height = 1
  Length = 4
  Placement = pos=(165,63.1,179) rot=(0,0,1;0rad)
  Width = 1.8
FEATURE [Part::MultiFuse] Fusion248002050166
  Placement = pos=(0,10,0) rot=(0,0,1;0rad)
  Refine = true
  Shapes = -> [Box530,Cylinder1271]
FEATURE [Part::Cylinder] Cylinder1272  label="Cylinder1560"
  Angle = 360
  AttacherType = Attacher::AttachEngine3D
  Height = 4
  Placement = pos=(165,64,180) rot=(0,1,0;1.5708rad)
  Radius = 0.9
FEATURE [Part::Box] Box531  label="Cube757"
  AttacherType = Attacher::AttachEngine3D
  Height = 1
  Length = 4
  Placement = pos=(165,63.1,179) rot=(0,0,1;0rad)
  Width = 1.8
FEATURE [Part::MultiFuse] Fusion248002050167
  Placement = pos=(0,12.5,0) rot=(0,0,1;0rad)
  Refine = true
  Shapes = -> [Box531,Cylinder1272]
FEATURE [Part::MultiFuse] Fusion248002050169
  Refine = true
  Shapes = -> [Cylinder1265,Cylinder1266]
FEATURE [Part::Cut] Cut014285
  Base = -> Box525
  Refine = true
  Tool = -> Fusion248002050169
FEATURE [Part::Fillet] Fillet409
  Base = -> Cut014285
  Edges = 4 edges r=1.99: [Edge2,Edge4,Edge11,Edge16]
FEATURE [Part::MultiFuse] Fusion248002050170
  Placement = pos=(159.5,-72,244) rot=(-1,0,0;1.5708rad)
  Refine = true
  Shapes = -> [Fusion248002050164,Fusion248002050165,Fusion248002050167,Fusion248002050166]
FEATURE [Part::Cut] Cut014286  label="crane-extender-arm-wires-holder"
  Base = -> Fillet409
  Placement = pos=(150,0,0) rot=(0,0,1;0rad)
  Refine = true
  Tool = -> Fusion248002050170
FEATURE [Part::FeaturePython] RefineLinearExtrude007  # WARN: FeaturePython — macro-defined, semantics opaque (R4)
FEATURE [Part::Extrusion] LinearExtrude007
  Base = -> RefineLinearExtrude007
  Dir = (0,0,6)
  DirMode = 0
  FaceMakerClass = Part::FaceMakerExtrusion
  LengthFwd = 0
  LengthRev = 0
  Placement = pos=(121,29,26.5) rot=(0,0,1;0rad)
  Solid = true
  Symmetric = false
FEATURE [Part::Box] Box532  label="Cube758"
  AttacherType = Attacher::AttachEngine3D
  Height = 6
  Length = 1
  Placement = pos=(141.5,31,26.5) rot=(0,0,1;0rad)
  Width = 76
FEATURE [Part::Box] Box533  label="Cube759"
  AttacherType = Attacher::AttachEngine3D
  Height = 6
  Length = 5
  Placement = pos=(141.5,107,26.5) rot=(0,0,1;0rad)
  Width = 8
FEATURE [Part::Cut] Cut014287
  Base = -> LinearExtrude007
  Refine = true
  Tool = -> Box533
FEATURE [Part::MultiFuse] Fusion248002050171
  Placement = pos=(12,0,2) rot=(0,0,1;0rad)
  Refine = true
  Shapes = -> [Cut014287,Box532]
FEATURE [Part::Cylinder] Cylinder1273  label="Cylinder1561"
  Angle = 360
  AttacherType = Attacher::AttachEngine3D
  Height = 76
  Placement = pos=(138,107,29.5) rot=(1,0,0;1.5708rad)
  Radius = 4.9
FEATURE [Part::Box] Box534  label="Cube760"
  AttacherType = Attacher::AttachEngine3D
  Height = 14
  Length = 14
  Placement = pos=(140.75,-5,22.5) rot=(0,0,1;0rad)
  Width = 180
FEATURE [Part::Cut] Cut014288
  Base = -> Cylinder1273
  Placement = pos=(14,0,2) rot=(0,0,1;0rad)
  Refine = true
  Tool = -> Box534
FEATURE [Part::Cylinder] Cylinder1274  label="Cylinder1562"
  Angle = 360
  AttacherType = Attacher::AttachEngine3D
  Height = 180
  Placement = pos=(151.5,175,31.5) rot=(1,0,0;1.5708rad)
  Radius = 8
FEATURE [Part::Cylinder] Cylinder1275  label="Cylinder1563"
  Angle = 360
  AttacherType = Attacher::AttachEngine3D
  Height = 180
  Placement = pos=(151.5,175,31.5) rot=(1,0,0;1.5708rad)
  Radius = 4.9
FEATURE [Part::Cut] Cut014289
  Base = -> Cylinder1274
  Placement = pos=(0.5,0,0) rot=(0,0,1;0rad)
  Refine = true
  Tool = -> Cylinder1275
FEATURE [Part::Cut] Cut014290
  Base = -> Fusion248002050171
  Refine = true
  Tool = -> Cut014289
FEATURE [Part::MultiFuse] Fusion248002050172
  Refine = true
  Shapes = -> [Cut014288,Cut014290]
FEATURE [Part::Cylinder] Cylinder1276  label="Cylinder1564"
  Angle = 360
  AttacherType = Attacher::AttachEngine3D
  Height = 150
  Placement = pos=(152,153,31.5) rot=(1,0,0;1.5708rad)
  Radius = 2
FEATURE [Part::Box] Box535  label="Cube761"
  AttacherType = Attacher::AttachEngine3D
  Height = 14
  Length = 14
  Placement = pos=(143.75,-5,13) rot=(0,0,1;0rad)
  Width = 180
FEATURE [Part::Cut] Cut014291
  Base = -> Fusion248002050172
  Refine = true
  Tool = -> Cylinder1276
FEATURE [Part::Box] Box536  label="Cube762"
  AttacherType = Attacher::AttachEngine3D
  Height = 14
  Length = 14
  Placement = pos=(143.5,28,23) rot=(0,0,1;0rad)
  Width = 10
FEATURE [Part::Cut] Cut014292
  Base = -> Cut014291
  Refine = true
  Tool = -> Box535
FEATURE [Part::Cut] Cut014293
  Base = -> Cut014292
  Refine = true
  Tool = -> Box536
FEATURE [Part::Cylinder] Cylinder1277  label="Cylinder1565"
  Angle = 360
  AttacherType = Attacher::AttachEngine3D
  Height = 7
  Placement = pos=(152,-1,31.5) rot=(1,0,0;1.5708rad)
  Radius = 4.9
FEATURE [Part::Cylinder] Cylinder1278  label="Cylinder1566"
  Angle = 360
  AttacherType = Attacher::AttachEngine3D
  Height = 2
  Placement = pos=(152,-6,31.5) rot=(1,0,0;1.5708rad)
  Radius = 6
FEATURE [Part::MultiFuse] Fusion248002050173
  Refine = true
  Shapes = -> [Cylinder1277,Cylinder1278]
FEATURE [Part::Cylinder] Cylinder1279  label="Cylinder1567"
  Angle = 360
  AttacherType = Attacher::AttachEngine3D
  Height = 2
  Placement = pos=(152,-1,31.5) rot=(1,0,0;1.5708rad)
  Radius = 2
FEATURE [Part::Cylinder] Cylinder1280  label="Cylinder1568"
  Angle = 360
  AttacherType = Attacher::AttachEngine3D
  Height = 10
  Placement = pos=(152,107,31.5) rot=(1,0,0;1.5708rad)
  Radius = 3
FEATURE [Part::Cut] Cut014294  label="crane-rotating-cylinder-cap"
  Base = -> Fusion248002050173
  Refine = true
  Tool = -> Cylinder1279
FEATURE [Part::Cut] Cut014295  label="crane-rotating-cylinder-rack-01"
  Base = -> Cut014293
  Refine = true
  Tool = -> Cylinder1280
FEATURE [Part::Cylinder] Cylinder1295  label="Cylinder1569"
  Angle = 360
  AttacherType = Attacher::AttachEngine3D
  Height = 3
  Placement = pos=(189.75,2.5,-57) rot=(0,0,1;0rad)
  Radius = 8
FEATURE [Part::Box] Box414  label="floor"
  AttacherType = Attacher::AttachEngine3D
  Height = 1
  Length = 600
  Placement = pos=(-10,-15,-93) rot=(0,0,1;0rad)
  Width = 200
FEATURE [Part::Cylinder] Cylinder1296  label="crane-stabilizers-cylinder-left-ALU"
  Angle = 360
  AttacherType = Attacher::AttachEngine3D
  Height = 45
  Placement = pos=(189.75,2.5,-50) rot=(0,0,1;0rad)
  Radius = 6
FEATURE [Part::Cylinder] Cylinder1297  label="Cylinder1570"
  Angle = 360
  AttacherType = Attacher::AttachEngine3D
  Height = 5
  Placement = pos=(189.75,2.5,-57) rot=(0,0,1;0rad)
  Radius = 5
FEATURE [Part::MultiFuse] Fusion248002050182
  Refine = true
  Shapes = -> [Cylinder1297,Cylinder1295]
FEATURE [Part::Cylinder] Cylinder1298  label="Cylinder1571"
  Angle = 360
  AttacherType = Attacher::AttachEngine3D
  Height = 4
  Placement = pos=(189.75,2.5,-56) rot=(0,0,1;0rad)
  Radius = 4
FEATURE [Part::Cut] Cut014300  label="crane-stabilizers-foot-left"
  Base = -> Fusion248002050182
  Refine = true
  Tool = -> Cylinder1298
FEATURE [Part::Cylinder] Cylinder1299  label="crane-stabilizers-piston-left-ALU"
  Angle = 360
  AttacherType = Attacher::AttachEngine3D
  Height = 46
  Placement = pos=(189.75,2.5,-57) rot=(0,0,1;0rad)
  Radius = 4
FEATURE [Part::Cylinder] Cylinder1300  label="Cylinder1572"
  Angle = 360
  AttacherType = Attacher::AttachEngine3D
  Height = 45
  Placement = pos=(189.75,2.5,-50) rot=(0,0,1;0rad)
  Radius = 4.9
FEATURE [Part::Cylinder] Cylinder1301  label="Cylinder1573"
  Angle = 360
  AttacherType = Attacher::AttachEngine3D
  Height = 2
  Placement = pos=(189.75,2.5,-52) rot=(0,0,1;0rad)
  Radius = 6
FEATURE [Part::MultiFuse] Fusion248002050183
  Refine = true
  Shapes = -> [Cylinder1301,Cylinder1300]
FEATURE [Part::Cylinder] Cylinder1302  label="Cylinder1574"
  Angle = 360
  AttacherType = Attacher::AttachEngine3D
  Height = 47
  Placement = pos=(189.75,2.5,-52) rot=(0,0,1;0rad)
  Radius = 4.2
FEATURE [Part::Cut] Cut014301
  Base = -> Fusion248002050183
  Refine = true
  Tool = -> Cylinder1302
FEATURE [Part::Box] Box539  label="Cube765"
  AttacherType = Attacher::AttachEngine3D
  Height = 45
  Length = 2
  Placement = pos=(193,1,-48) rot=(0,0,1;0rad)
  Width = 3
FEATURE [Part::Cut] Cut014302  label="crane-stabilizers-inner-chambre-left"
  Base = -> Cut014301
  Refine = true
  Tool = -> Box539
FEATURE [Part::Box] Box540  label="Cube766"
  AttacherType = Attacher::AttachEngine3D
  Height = 17.8
  Length = 7.8
  Placement = pos=(185.95,10,7.1) rot=(0,0,1;0rad)
  Width = 20
FEATURE [Part::Box] Box541  label="Cube767"
  AttacherType = Attacher::AttachEngine3D
  Height = 20
  Length = 18
  Placement = pos=(143,52,19) rot=(0,0,1;0rad)
  Width = 5
FEATURE [Part::Box] Box543  label="Cube769"
  AttacherType = Attacher::AttachEngine3D
  Height = 11
  Length = 31
  Placement = pos=(150.5,52,17) rot=(0,0,1;0rad)
  Width = 5
FEATURE [Part::Cylinder] Cylinder1303  label="Cylinder1575"
  Angle = 360
  AttacherType = Attacher::AttachEngine3D
  Height = 20
  Placement = pos=(152,46,31.5) rot=(-1,0,0;1.5708rad)
  Radius = 6.15
FEATURE [Part::Cylinder] Cylinder1305  label="Cylinder1576"
  Angle = 360
  AttacherType = Attacher::AttachEngine3D
  Height = 10
  Placement = pos=(164.5,62,24) rot=(1,0,0;1.5708rad)
  Radius = 1.6
FEATURE [Part::Cylinder] Cylinder1306  label="Cylinder1577"
  Angle = 360
  AttacherType = Attacher::AttachEngine3D
  Height = 10
  Placement = pos=(143,54.5,32) rot=(0,1,0;1.5708rad)
  Radius = 1.25
FEATURE [Part::Cylinder] Cylinder1307  label="Cylinder1578"
  Angle = 360
  AttacherType = Attacher::AttachEngine3D
  Height = 10
  Placement = pos=(177.5,62,24) rot=(1,0,0;1.5708rad)
  Radius = 1.6
FEATURE [Part::MultiFuse] Fusion248002050184
  Refine = true
  Shapes = -> [Cylinder1307,Cylinder1305]
FEATURE [Part::MultiFuse] Fusion248002050185
  Refine = true
  Shapes = -> [Box543,Box541]
FEATURE [Part::Cut] Cut014303
  Base = -> Fusion248002050185
  Refine = true
  Tool = -> Fusion248002050184
FEATURE [Part::Cut] Cut014304
  Base = -> Cut014303
  Refine = true
  Tool = -> Cylinder1303
FEATURE [Part::Cut] Cut014305
  Base = -> Cut014304
  Refine = true
  Tool = -> Cylinder1306
FEATURE [Part::Chamfer] Chamfer120
  Base = -> Cut014305
  Edges = 1 edges r=1.99: [Edge1]
FEATURE [Part::Chamfer] Chamfer121
  Base = -> Chamfer120
  Edges = 1 edges r=7.49: [Edge31]
FEATURE [Part::Fillet] Fillet412
  Base = -> Chamfer121
  Edges = 2 edges r=5: [Edge22,Edge26]
FEATURE [Part::Fillet] Fillet413  label="crane-rotating-cylinder-holder-left"
  Base = -> Fillet412
  Edges = 1 edges r=10: [Edge18]
FEATURE [Part::Box] Box544  label="Cube770"
  AttacherType = Attacher::AttachEngine3D
  Height = 20
  Length = 18
  Placement = pos=(143,52,19) rot=(0,0,1;0rad)
  Width = 5
FEATURE [Part::Box] Box545  label="Cube771"
  AttacherType = Attacher::AttachEngine3D
  Height = 11
  Length = 31
  Placement = pos=(150.5,52,17) rot=(0,0,1;0rad)
  Width = 5
FEATURE [Part::Cylinder] Cylinder1308  label="Cylinder1579"
  Angle = 360
  AttacherType = Attacher::AttachEngine3D
  Height = 20
  Placement = pos=(152,46,31.5) rot=(-1,0,0;1.5708rad)
  Radius = 6.15
FEATURE [Part::Cylinder] Cylinder1309  label="Cylinder1580"
  Angle = 360
  AttacherType = Attacher::AttachEngine3D
  Height = 10
  Placement = pos=(164.5,62,24) rot=(1,0,0;1.5708rad)
  Radius = 1.6
FEATURE [Part::Cylinder] Cylinder1310  label="Cylinder1581"
  Angle = 360
  AttacherType = Attacher::AttachEngine3D
  Height = 10
  Placement = pos=(143,54.5,32) rot=(0,1,0;1.5708rad)
  Radius = 1.25
FEATURE [Part::Cylinder] Cylinder1311  label="Cylinder1582"
  Angle = 360
  AttacherType = Attacher::AttachEngine3D
  Height = 10
  Placement = pos=(177.5,62,24) rot=(1,0,0;1.5708rad)
  Radius = 1.6
FEATURE [Part::MultiFuse] Fusion248002050186
  Refine = true
  Shapes = -> [Cylinder1311,Cylinder1309]
FEATURE [Part::MultiFuse] Fusion248002050187
  Refine = true
  Shapes = -> [Box545,Box544]
FEATURE [Part::Cut] Cut014306
  Base = -> Fusion248002050187
  Refine = true
  Tool = -> Fusion248002050186
FEATURE [Part::Cut] Cut014307
  Base = -> Cut014306
  Refine = true
  Tool = -> Cylinder1308
FEATURE [Part::Cut] Cut014308
  Base = -> Cut014307
  Refine = true
  Tool = -> Cylinder1310
FEATURE [Part::Chamfer] Chamfer122
  Base = -> Cut014308
  Edges = 1 edges r=1.99: [Edge1]
FEATURE [Part::Chamfer] Chamfer123
  Base = -> Chamfer122
  Edges = 1 edges r=7.49: [Edge31]
FEATURE [Part::Fillet] Fillet414
  Base = -> Chamfer123
  Edges = 2 edges r=5: [Edge22,Edge26]
FEATURE [Part::Fillet] Fillet415
  Base = -> Fillet414
  Edges = 1 edges r=10: [Edge18]
  Placement = pos=(0,61,0) rot=(0,0,1;0rad)
FEATURE [Part::Cylinder] Cylinder1312  label="Cylinder1583"
  Angle = 360
  AttacherType = Attacher::AttachEngine3D
  Height = 10
  Placement = pos=(172.5,118,20) rot=(1,0,0;1.5708rad)
  Radius = 1.6
FEATURE [Part::Cut] Cut014309  label="crane-rotating-cylinder-holder-right"
  Base = -> Fillet415
  Refine = true
  Tool = -> Cylinder1312
FEATURE [App::DocumentObjectGroup] Group005  label="rotation"
  Group = -> [Cut014255,Fusion248002050127,Cut014259,Cut014283,Cut014284,Cut014295,Cut014294,Chamfer109,Cut014309,Fillet413]
FEATURE [Part::Cylinder] Cylinder1313  label="Cylinder1584"
  Angle = 360
  AttacherType = Attacher::AttachEngine3D
  Height = 10
  Placement = pos=(177.5,113,24) rot=(1,0,0;1.5708rad)
  Radius = 1.25
FEATURE [Part::Cylinder] Cylinder1314  label="Cylinder1585"
  Angle = 360
  AttacherType = Attacher::AttachEngine3D
  Height = 7
  Placement = pos=(177.5,64,24) rot=(1,0,0;1.5708rad)
  Radius = 1.25
FEATURE [Part::MultiFuse] Fusion248002050188
  Refine = true
  Shapes = -> [Cylinder1314,Cylinder1313]
FEATURE [Part::Cylinder] Cylinder1315  label="Cylinder1586"
  Angle = 360
  AttacherType = Attacher::AttachEngine3D
  Height = 27
  Radius = 8
FEATURE [Part::Box] Box547  label="Cube773"
  AttacherType = Attacher::AttachEngine3D
  Height = 27
  Length = 10.4
  Placement = pos=(-5.2,-6.2,0) rot=(0,0,1;0rad)
  Width = 12.4
FEATURE [Part::Cylinder] Cylinder1316  label="Cylinder1587"
  Angle = 360
  AttacherType = Attacher::AttachEngine3D
  Height = 17
  Radius = 8
FEATURE [Part::Cylinder] Cylinder1317  label="Cylinder1588"
  Angle = 360
  AttacherType = Attacher::AttachEngine3D
  Height = 17
  Radius = 6.5
FEATURE [Part::Cut] Cut014312
  Base = -> Cylinder1316
  Refine = true
  Tool = -> Cylinder1317
FEATURE [Part::Fillet] Fillet416
  Base = -> Box547
  Edges = 4 edges r=1: [Edge1,Edge3,Edge5,Edge7]
FEATURE [Part::Cut] Cut014313
  Base = -> Cylinder1315
  Refine = true
  Tool = -> Fillet416
FEATURE [Part::MultiFuse] Fusion248002050189
  Refine = true
  Shapes = -> [Cut014312,Cut014313]
FEATURE [Part::Cylinder] Cylinder1318  label="Cylinder1589"
  Angle = 360
  AttacherType = Attacher::AttachEngine3D
  Height = 27
  Radius = 8
FEATURE [Part::Cut] Cut014314  label="cylinder-motor-extender006"
  Base = -> Cylinder1318
  Placement = pos=(309.5,98.5,187.5) rot=(0,1,0;1.5708rad)
  Refine = true
  Tool = -> Fusion248002050189
FEATURE [Part::Cylinder] Cylinder1319  label="Cylinder1590"
  Angle = 360
  AttacherType = Attacher::AttachEngine3D
  Height = 3
  Placement = pos=(333.5,98.5,186.5) rot=(0,1,0;1.5708rad)
  Radius = 5
FEATURE [Part::Cylinder] Cylinder1320  label="Cylinder1591"
  Angle = 360
  AttacherType = Attacher::AttachEngine3D
  Height = 6
  Placement = pos=(336.5,98.5,186.5) rot=(0,1,0;1.5708rad)
  Radius = 6.1
FEATURE [Part::MultiFuse] Fusion248002050190
  Placement = pos=(3,0,1) rot=(0,0,1;0rad)
  Refine = true
  Shapes = -> [Cylinder1319,Cylinder1320]
FEATURE [Part::Cylinder] Cylinder1321  label="Cylinder1592"
  Angle = 360
  AttacherType = Attacher::AttachEngine3D
  Height = 14
  Placement = pos=(184,47,128) rot=(1,0,0;1.5708rad)
  Radius = 0.9
FEATURE [Part::Cylinder] Cylinder1322  label="Cylinder1593"
  Angle = 360
  AttacherType = Attacher::AttachEngine3D
  Height = 1.6
  Placement = pos=(184,47,128) rot=(1,0,0;1.5708rad)
  Radius = 2.1
FEATURE [Part::MultiFuse] Fusion248002050191
  Placement = pos=(124,59,65) rot=(0,0,1;0rad)
  Refine = true
  Shapes = -> [Cylinder1321,Cylinder1322]
FEATURE [Part::Cylinder] Cylinder1323  label="Cylinder1594"
  Angle = 360
  AttacherType = Attacher::AttachEngine3D
  Height = 14
  Placement = pos=(184,47,128) rot=(1,0,0;1.5708rad)
  Radius = 0.9
FEATURE [Part::Cylinder] Cylinder1324  label="Cylinder1595"
  Angle = 360
  AttacherType = Attacher::AttachEngine3D
  Height = 1.6
  Placement = pos=(184,47,128) rot=(1,0,0;1.5708rad)
  Radius = 2.1
FEATURE [Part::MultiFuse] Fusion248002050192
  Placement = pos=(154,59,65) rot=(0,0,1;0rad)
  Refine = true
  Shapes = -> [Cylinder1323,Cylinder1324]
FEATURE [Part::Cylinder] Cylinder1325  label="Cylinder1596"
  Angle = 360
  AttacherType = Attacher::AttachEngine3D
  Height = 14
  Placement = pos=(184,47,128) rot=(1,0,0;1.5708rad)
  Radius = 0.9
FEATURE [Part::Cylinder] Cylinder1326  label="Cylinder1597"
  Angle = 360
  AttacherType = Attacher::AttachEngine3D
  Height = 1.6
  Placement = pos=(184,47,128) rot=(1,0,0;1.5708rad)
  Radius = 2.1
FEATURE [Part::MultiFuse] Fusion248002050193
  Placement = pos=(124,59,54) rot=(0,0,1;0rad)
  Refine = true
  Shapes = -> [Cylinder1325,Cylinder1326]
FEATURE [Part::Cylinder] Cylinder1327  label="Cylinder1598"
  Angle = 360
  AttacherType = Attacher::AttachEngine3D
  Height = 14
  Placement = pos=(184,47,128) rot=(1,0,0;1.5708rad)
  Radius = 0.9
FEATURE [Part::Cylinder] Cylinder1328  label="Cylinder1599"
  Angle = 360
  AttacherType = Attacher::AttachEngine3D
  Height = 1.6
  Placement = pos=(184,47,128) rot=(1,0,0;1.5708rad)
  Radius = 2.1
FEATURE [Part::MultiFuse] Fusion248002050194
  Placement = pos=(154,59,54) rot=(0,0,1;0rad)
  Refine = true
  Shapes = -> [Cylinder1327,Cylinder1328]
FEATURE [Part::MultiFuse] Fusion248002050195
  Placement = pos=(0,1,0) rot=(0,0,1;0rad)
  Refine = true
  Shapes = -> [Fusion248002050191,Fusion248002050192,Fusion248002050193,Fusion248002050194]
FEATURE [Part::MultiFuse] Fusion248002050196
  Placement = pos=(91.25,190,334.5) rot=(0.57735,0.57735,-0.57735;2.0944rad)
  Refine = true
  Shapes = -> [Cut014314,Fusion248002050190,Fusion248002050195]
FEATURE [Part::Box] Box546  label="Cube772"
  AttacherType = Attacher::AttachEngine3D
  Height = 39
  Length = 11.5
  Placement = pos=(182.25,-5,-11) rot=(0,0,1;0rad)
  Width = 15
FEATURE [Part::Box] Box548  label="Cube774"
  AttacherType = Attacher::AttachEngine3D
  Height = 39
  Length = 3.5
  Placement = pos=(193.75,-5,-11) rot=(0,0,1;0rad)
  Width = 15
FEATURE [Part::Fillet] Fillet417
  Base = -> Box546
  Edges = 2 edges r=2: [Edge1,Edge3]
FEATURE [Part::Fillet] Fillet418
  Base = -> Box548
  Edges = 2 edges r=2: [Edge5,Edge7]
FEATURE [Part::Cylinder] Cylinder1329  label="Cylinder1600"
  Angle = 360
  AttacherType = Attacher::AttachEngine3D
  Height = 27
  Radius = 8
FEATURE [Part::Box] Box549  label="Cube775"
  AttacherType = Attacher::AttachEngine3D
  Height = 27
  Length = 10.4
  Placement = pos=(-5.2,-6.2,0) rot=(0,0,1;0rad)
  Width = 12.4
FEATURE [Part::Cylinder] Cylinder1330  label="Cylinder1601"
  Angle = 360
  AttacherType = Attacher::AttachEngine3D
  Height = 17
  Radius = 8
FEATURE [Part::Cylinder] Cylinder1331  label="Cylinder1602"
  Angle = 360
  AttacherType = Attacher::AttachEngine3D
  Height = 17
  Radius = 6.5
FEATURE [Part::Cut] Cut014315
  Base = -> Cylinder1330
  Refine = true
  Tool = -> Cylinder1331
FEATURE [Part::Fillet] Fillet419
  Base = -> Box549
  Edges = 4 edges r=1: [Edge1,Edge3,Edge5,Edge7]
FEATURE [Part::Cut] Cut014316
  Base = -> Cylinder1329
  Refine = true
  Tool = -> Fillet419
FEATURE [Part::MultiFuse] Fusion248002050197
  Refine = true
  Shapes = -> [Cut014315,Cut014316]
FEATURE [Part::Cylinder] Cylinder1332  label="Cylinder1603"
  Angle = 360
  AttacherType = Attacher::AttachEngine3D
  Height = 27
  Radius = 8
FEATURE [Part::Cut] Cut014317  label="cylinder-motor-extender007"
  Base = -> Cylinder1332
  Placement = pos=(309.5,98.5,187.5) rot=(0,1,0;1.5708rad)
  Refine = true
  Tool = -> Fusion248002050197
FEATURE [Part::Cylinder] Cylinder1333  label="Cylinder1604"
  Angle = 360
  AttacherType = Attacher::AttachEngine3D
  Height = 3
  Placement = pos=(333.5,98.5,186.5) rot=(0,1,0;1.5708rad)
  Radius = 5
FEATURE [Part::Cylinder] Cylinder1334  label="Cylinder1605"
  Angle = 360
  AttacherType = Attacher::AttachEngine3D
  Height = 6
  Placement = pos=(336.5,98.5,186.5) rot=(0,1,0;1.5708rad)
  Radius = 6.1
FEATURE [Part::MultiFuse] Fusion248002050198
  Placement = pos=(3,0,1) rot=(0,0,1;0rad)
  Refine = true
  Shapes = -> [Cylinder1333,Cylinder1334]
FEATURE [Part::Cylinder] Cylinder1335  label="Cylinder1606"
  Angle = 360
  AttacherType = Attacher::AttachEngine3D
  Height = 14
  Placement = pos=(184,47,128) rot=(1,0,0;1.5708rad)
  Radius = 1.1
FEATURE [Part::Cylinder] Cylinder1336  label="Cylinder1607"
  Angle = 360
  AttacherType = Attacher::AttachEngine3D
  Height = 1.6
  Placement = pos=(184,47,128) rot=(1,0,0;1.5708rad)
  Radius = 2.1
FEATURE [Part::MultiFuse] Fusion248002050199
  Placement = pos=(124,59,65) rot=(0,0,1;0rad)
  Refine = true
  Shapes = -> [Cylinder1335,Cylinder1336]
FEATURE [Part::Cylinder] Cylinder1337  label="Cylinder1608"
  Angle = 360
  AttacherType = Attacher::AttachEngine3D
  Height = 14
  Placement = pos=(184,47,128) rot=(1,0,0;1.5708rad)
  Radius = 1.1
FEATURE [Part::Cylinder] Cylinder1338  label="Cylinder1609"
  Angle = 360
  AttacherType = Attacher::AttachEngine3D
  Height = 1.6
  Placement = pos=(184,47,128) rot=(1,0,0;1.5708rad)
  Radius = 2.1
FEATURE [Part::MultiFuse] Fusion248002050200
  Placement = pos=(154,59,65) rot=(0,0,1;0rad)
  Refine = true
  Shapes = -> [Cylinder1337,Cylinder1338]
FEATURE [Part::Cylinder] Cylinder1339  label="Cylinder1610"
  Angle = 360
  AttacherType = Attacher::AttachEngine3D
  Height = 14
  Placement = pos=(184,47,128) rot=(1,0,0;1.5708rad)
  Radius = 1.1
FEATURE [Part::Cylinder] Cylinder1340  label="Cylinder1611"
  Angle = 360
  AttacherType = Attacher::AttachEngine3D
  Height = 1.6
  Placement = pos=(184,47,128) rot=(1,0,0;1.5708rad)
  Radius = 2.1
FEATURE [Part::MultiFuse] Fusion248002050201
  Placement = pos=(124,59,54) rot=(0,0,1;0rad)
  Refine = true
  Shapes = -> [Cylinder1339,Cylinder1340]
FEATURE [Part::Cylinder] Cylinder1341  label="Cylinder1612"
  Angle = 360
  AttacherType = Attacher::AttachEngine3D
  Height = 14
  Placement = pos=(184,47,128) rot=(1,0,0;1.5708rad)
  Radius = 1.1
FEATURE [Part::Cylinder] Cylinder1342  label="Cylinder1613"
  Angle = 360
  AttacherType = Attacher::AttachEngine3D
  Height = 1.6
  Placement = pos=(184,47,128) rot=(1,0,0;1.5708rad)
  Radius = 2.1
FEATURE [Part::MultiFuse] Fusion248002050202
  Placement = pos=(154,59,54) rot=(0,0,1;0rad)
  Refine = true
  Shapes = -> [Cylinder1341,Cylinder1342]
FEATURE [Part::MultiFuse] Fusion248002050203
  Placement = pos=(0,1,0) rot=(0,0,1;0rad)
  Refine = true
  Shapes = -> [Fusion248002050199,Fusion248002050200,Fusion248002050201,Fusion248002050202]
FEATURE [Part::MultiFuse] Fusion248002050204
  Placement = pos=(91.25,190,334.5) rot=(0.57735,0.57735,-0.57735;2.0944rad)
  Refine = true
  Shapes = -> [Cut014317,Fusion248002050198,Fusion248002050203]
FEATURE [Part::Cut] Cut014318
  Base = -> Fillet417
  Refine = true
  Tool = -> Fusion248002050196
FEATURE [Part::Cut] Cut014319  label="crane-stabilizers-lifter-motor-holder-cover-left"
  Base = -> Fillet418
  Refine = true
  Tool = -> Fusion248002050204
FEATURE [Part::Cylinder] Cylinder1343  label="Cylinder1614"
  Angle = 360
  AttacherType = Attacher::AttachEngine3D
  Height = 50
  Placement = pos=(190,8.5,21.2) rot=(-1,0,0;1.5708rad)
  Radius = 3.15
FEATURE [Part::MultiFuse] Fusion248002050205
  Refine = true
  Shapes = -> [Cut014318,Box540]
FEATURE [Part::Cylinder] Cylinder1344  label="crane-stabilizers-opener-cylinder-right-ALU"
  Angle = 360
  AttacherType = Attacher::AttachEngine3D
  Height = 50
  Placement = pos=(190,111.5,10.8) rot=(-1,0,0;1.5708rad)
  Radius = 3.1
FEATURE [Part::Cylinder] Cylinder1345  label="crane-stabilizers-opener-cylinder-left-ALU"
  Angle = 360
  AttacherType = Attacher::AttachEngine3D
  Height = 50
  Placement = pos=(190,8.5,21.2) rot=(-1,0,0;1.5708rad)
  Radius = 3.1
FEATURE [Part::Cut] Cut014320  label="crane-stabilizers-lifter-motor-holder-left"
  Base = -> Fusion248002050205
  Refine = true
  Tool = -> Cylinder1343
FEATURE [Part::Cylinder] Cylinder1346  label="Cylinder1615"
  Angle = 360
  AttacherType = Attacher::AttachEngine3D
  Height = 50
  Placement = pos=(190,111.5,10.8) rot=(-1,0,0;1.5708rad)
  Radius = 3.15
FEATURE [Part::Box] Box550  label="Cube776"
  AttacherType = Attacher::AttachEngine3D
  Height = 17.8
  Length = 7.8
  Placement = pos=(185.95,10,7.1) rot=(0,0,1;0rad)
  Width = 20
FEATURE [Part::Cylinder] Cylinder1347  label="Cylinder1619"
  Angle = 360
  AttacherType = Attacher::AttachEngine3D
  Height = 27
  Radius = 8
FEATURE [Part::Box] Box551  label="Cube777"
  AttacherType = Attacher::AttachEngine3D
  Height = 27
  Length = 10.4
  Placement = pos=(-5.2,-6.2,0) rot=(0,0,1;0rad)
  Width = 12.4
FEATURE [Part::Cylinder] Cylinder1348  label="Cylinder1620"
  Angle = 360
  AttacherType = Attacher::AttachEngine3D
  Height = 17
  Radius = 8
FEATURE [Part::Cylinder] Cylinder1349  label="Cylinder1621"
  Angle = 360
  AttacherType = Attacher::AttachEngine3D
  Height = 17
  Radius = 6.5
FEATURE [Part::Cut] Cut014321
  Base = -> Cylinder1348
  Refine = true
  Tool = -> Cylinder1349
FEATURE [Part::Fillet] Fillet420
  Base = -> Box551
  Edges = 4 edges r=1: [Edge1,Edge3,Edge5,Edge7]
FEATURE [Part::Cut] Cut014322
  Base = -> Cylinder1347
  Refine = true
  Tool = -> Fillet420
FEATURE [Part::MultiFuse] Fusion248002050206
  Refine = true
  Shapes = -> [Cut014321,Cut014322]
FEATURE [Part::Cylinder] Cylinder1350  label="Cylinder1622"
  Angle = 360
  AttacherType = Attacher::AttachEngine3D
  Height = 27
  Radius = 8
FEATURE [Part::Cut] Cut014323  label="cylinder-motor-extender008"
  Base = -> Cylinder1350
  Placement = pos=(309.5,98.5,187.5) rot=(0,1,0;1.5708rad)
  Refine = true
  Tool = -> Fusion248002050206
FEATURE [Part::Cylinder] Cylinder1351  label="Cylinder1623"
  Angle = 360
  AttacherType = Attacher::AttachEngine3D
  Height = 3
  Placement = pos=(333.5,98.5,186.5) rot=(0,1,0;1.5708rad)
  Radius = 5
FEATURE [Part::Cylinder] Cylinder1352  label="Cylinder1624"
  Angle = 360
  AttacherType = Attacher::AttachEngine3D
  Height = 6
  Placement = pos=(336.5,98.5,186.5) rot=(0,1,0;1.5708rad)
  Radius = 6.1
FEATURE [Part::MultiFuse] Fusion248002050207
  Placement = pos=(3,0,1) rot=(0,0,1;0rad)
  Refine = true
  Shapes = -> [Cylinder1351,Cylinder1352]
FEATURE [Part::Cylinder] Cylinder1353  label="Cylinder1625"
  Angle = 360
  AttacherType = Attacher::AttachEngine3D
  Height = 14
  Placement = pos=(184,47,128) rot=(1,0,0;1.5708rad)
  Radius = 0.9
FEATURE [Part::Cylinder] Cylinder1354  label="Cylinder1626"
  Angle = 360
  AttacherType = Attacher::AttachEngine3D
  Height = 1.6
  Placement = pos=(184,47,128) rot=(1,0,0;1.5708rad)
  Radius = 2.1
FEATURE [Part::MultiFuse] Fusion248002050208
  Placement = pos=(124,59,65) rot=(0,0,1;0rad)
  Refine = true
  Shapes = -> [Cylinder1353,Cylinder1354]
FEATURE [Part::Cylinder] Cylinder1355  label="Cylinder1627"
  Angle = 360
  AttacherType = Attacher::AttachEngine3D
  Height = 14
  Placement = pos=(184,47,128) rot=(1,0,0;1.5708rad)
  Radius = 0.9
FEATURE [Part::Cylinder] Cylinder1356  label="Cylinder1628"
  Angle = 360
  AttacherType = Attacher::AttachEngine3D
  Height = 1.6
  Placement = pos=(184,47,128) rot=(1,0,0;1.5708rad)
  Radius = 2.1
FEATURE [Part::MultiFuse] Fusion248002050209
  Placement = pos=(154,59,65) rot=(0,0,1;0rad)
  Refine = true
  Shapes = -> [Cylinder1355,Cylinder1356]
FEATURE [Part::Cylinder] Cylinder1357  label="Cylinder1629"
  Angle = 360
  AttacherType = Attacher::AttachEngine3D
  Height = 14
  Placement = pos=(184,47,128) rot=(1,0,0;1.5708rad)
  Radius = 0.9
FEATURE [Part::Cylinder] Cylinder1358  label="Cylinder1630"
  Angle = 360
  AttacherType = Attacher::AttachEngine3D
  Height = 1.6
  Placement = pos=(184,47,128) rot=(1,0,0;1.5708rad)
  Radius = 2.1
FEATURE [Part::MultiFuse] Fusion248002050210
  Placement = pos=(124,59,54) rot=(0,0,1;0rad)
  Refine = true
  Shapes = -> [Cylinder1357,Cylinder1358]
FEATURE [Part::Cylinder] Cylinder1359  label="Cylinder1631"
  Angle = 360
  AttacherType = Attacher::AttachEngine3D
  Height = 14
  Placement = pos=(184,47,128) rot=(1,0,0;1.5708rad)
  Radius = 0.9
FEATURE [Part::Cylinder] Cylinder1360  label="Cylinder1632"
  Angle = 360
  AttacherType = Attacher::AttachEngine3D
  Height = 1.6
  Placement = pos=(184,47,128) rot=(1,0,0;1.5708rad)
  Radius = 2.1
FEATURE [Part::MultiFuse] Fusion248002050211
  Placement = pos=(154,59,54) rot=(0,0,1;0rad)
  Refine = true
  Shapes = -> [Cylinder1359,Cylinder1360]
FEATURE [Part::MultiFuse] Fusion248002050212
  Placement = pos=(0,1,0) rot=(0,0,1;0rad)
  Refine = true
  Shapes = -> [Fusion248002050208,Fusion248002050209,Fusion248002050210,Fusion248002050211]
FEATURE [Part::MultiFuse] Fusion248002050213
  Placement = pos=(91.25,190,334.5) rot=(0.57735,0.57735,-0.57735;2.0944rad)
  Refine = true
  Shapes = -> [Cut014323,Fusion248002050207,Fusion248002050212]
FEATURE [Part::Box] Box552  label="Cube778"
  AttacherType = Attacher::AttachEngine3D
  Height = 39
  Length = 11.5
  Placement = pos=(182.25,-5,-11) rot=(0,0,1;0rad)
  Width = 15
FEATURE [Part::Fillet] Fillet421
  Base = -> Box552
  Edges = 2 edges r=2: [Edge1,Edge3]
FEATURE [Part::Cut] Cut014324
  Base = -> Fillet421
  Refine = true
  Tool = -> Fusion248002050213
FEATURE [Part::MultiFuse] Fusion248002050214
  Refine = true
  Shapes = -> [Cut014324,Box550]
FEATURE [Part::Mirroring] Part__Mirroring037  label="Fusion248002050214 (Mirror #4)"
  Base = (0,0,0)
  Normal = (0,1,0)
  Placement = pos=(0,170,0) rot=(0,0,1;0rad)
  Source = -> Fusion248002050214
FEATURE [Part::Cut] Cut014325  label="crane-stabilizers-lifter-motor-holder-right"
  Base = -> Part__Mirroring037
  Refine = true
  Tool = -> Cylinder1346
FEATURE [Part::Box] Box553  label="Cube779"
  AttacherType = Attacher::AttachEngine3D
  Height = 39
  Length = 3.5
  Placement = pos=(193.75,-5,-11) rot=(0,0,1;0rad)
  Width = 15
FEATURE [Part::Fillet] Fillet422
  Base = -> Box553
  Edges = 2 edges r=2: [Edge5,Edge7]
FEATURE [Part::Cylinder] Cylinder1361  label="Cylinder1647"
  Angle = 360
  AttacherType = Attacher::AttachEngine3D
  Height = 27
  Radius = 8
FEATURE [Part::Box] Box554  label="Cube780"
  AttacherType = Attacher::AttachEngine3D
  Height = 27
  Length = 10.4
  Placement = pos=(-5.2,-6.2,0) rot=(0,0,1;0rad)
  Width = 12.4
FEATURE [Part::Cylinder] Cylinder1362  label="Cylinder1648"
  Angle = 360
  AttacherType = Attacher::AttachEngine3D
  Height = 17
  Radius = 8
FEATURE [Part::Cylinder] Cylinder1363  label="Cylinder1649"
  Angle = 360
  AttacherType = Attacher::AttachEngine3D
  Height = 17
  Radius = 6.5
FEATURE [Part::Cut] Cut014326
  Base = -> Cylinder1362
  Refine = true
  Tool = -> Cylinder1363
FEATURE [Part::Fillet] Fillet423
  Base = -> Box554
  Edges = 4 edges r=1: [Edge1,Edge3,Edge5,Edge7]
FEATURE [Part::Cut] Cut014327
  Base = -> Cylinder1361
  Refine = true
  Tool = -> Fillet423
FEATURE [Part::MultiFuse] Fusion248002050215
  Refine = true
  Shapes = -> [Cut014326,Cut014327]
FEATURE [Part::Cylinder] Cylinder1364  label="Cylinder1650"
  Angle = 360
  AttacherType = Attacher::AttachEngine3D
  Height = 27
  Radius = 8
FEATURE [Part::Cut] Cut014328  label="cylinder-motor-extender009"
  Base = -> Cylinder1364
  Placement = pos=(309.5,98.5,187.5) rot=(0,1,0;1.5708rad)
  Refine = true
  Tool = -> Fusion248002050215
FEATURE [Part::Cylinder] Cylinder1365  label="Cylinder1651"
  Angle = 360
  AttacherType = Attacher::AttachEngine3D
  Height = 3
  Placement = pos=(333.5,98.5,186.5) rot=(0,1,0;1.5708rad)
  Radius = 5
FEATURE [Part::Cylinder] Cylinder1366  label="Cylinder1652"
  Angle = 360
  AttacherType = Attacher::AttachEngine3D
  Height = 6
  Placement = pos=(336.5,98.5,186.5) rot=(0,1,0;1.5708rad)
  Radius = 6.1
FEATURE [Part::MultiFuse] Fusion248002050216
  Placement = pos=(3,0,1) rot=(0,0,1;0rad)
  Refine = true
  Shapes = -> [Cylinder1365,Cylinder1366]
FEATURE [Part::Cylinder] Cylinder1367  label="Cylinder1653"
  Angle = 360
  AttacherType = Attacher::AttachEngine3D
  Height = 14
  Placement = pos=(184,47,128) rot=(1,0,0;1.5708rad)
  Radius = 1.1
FEATURE [Part::Cylinder] Cylinder1368  label="Cylinder1654"
  Angle = 360
  AttacherType = Attacher::AttachEngine3D
  Height = 1.6
  Placement = pos=(184,47,128) rot=(1,0,0;1.5708rad)
  Radius = 2.1
FEATURE [Part::MultiFuse] Fusion248002050217
  Placement = pos=(124,59,65) rot=(0,0,1;0rad)
  Refine = true
  Shapes = -> [Cylinder1367,Cylinder1368]
FEATURE [Part::Cylinder] Cylinder1369  label="Cylinder1655"
  Angle = 360
  AttacherType = Attacher::AttachEngine3D
  Height = 14
  Placement = pos=(184,47,128) rot=(1,0,0;1.5708rad)
  Radius = 1.1
FEATURE [Part::Cylinder] Cylinder1370  label="Cylinder1656"
  Angle = 360
  AttacherType = Attacher::AttachEngine3D
  Height = 1.6
  Placement = pos=(184,47,128) rot=(1,0,0;1.5708rad)
  Radius = 2.1
FEATURE [Part::MultiFuse] Fusion248002050218
  Placement = pos=(154,59,65) rot=(0,0,1;0rad)
  Refine = true
  Shapes = -> [Cylinder1369,Cylinder1370]
FEATURE [Part::Cylinder] Cylinder1371  label="Cylinder1657"
  Angle = 360
  AttacherType = Attacher::AttachEngine3D
  Height = 14
  Placement = pos=(184,47,128) rot=(1,0,0;1.5708rad)
  Radius = 1.1
FEATURE [Part::Cylinder] Cylinder1372  label="Cylinder1658"
  Angle = 360
  AttacherType = Attacher::AttachEngine3D
  Height = 1.6
  Placement = pos=(184,47,128) rot=(1,0,0;1.5708rad)
  Radius = 2.1
FEATURE [Part::MultiFuse] Fusion248002050219
  Placement = pos=(124,59,54) rot=(0,0,1;0rad)
  Refine = true
  Shapes = -> [Cylinder1371,Cylinder1372]
FEATURE [Part::Cylinder] Cylinder1373  label="Cylinder1659"
  Angle = 360
  AttacherType = Attacher::AttachEngine3D
  Height = 14
  Placement = pos=(184,47,128) rot=(1,0,0;1.5708rad)
  Radius = 1.1
FEATURE [Part::Cylinder] Cylinder1374  label="Cylinder1660"
  Angle = 360
  AttacherType = Attacher::AttachEngine3D
  Height = 1.6
  Placement = pos=(184,47,128) rot=(1,0,0;1.5708rad)
  Radius = 2.1
FEATURE [Part::MultiFuse] Fusion248002050220
  Placement = pos=(154,59,54) rot=(0,0,1;0rad)
  Refine = true
  Shapes = -> [Cylinder1373,Cylinder1374]
FEATURE [Part::MultiFuse] Fusion248002050221
  Placement = pos=(0,1,0) rot=(0,0,1;0rad)
  Refine = true
  Shapes = -> [Fusion248002050217,Fusion248002050218,Fusion248002050219,Fusion248002050220]
FEATURE [Part::MultiFuse] Fusion248002050222
  Placement = pos=(91.25,190,334.5) rot=(0.57735,0.57735,-0.57735;2.0944rad)
  Refine = true
  Shapes = -> [Cut014328,Fusion248002050216,Fusion248002050221]
FEATURE [Part::Cut] Cut014329
  Base = -> Fillet422
  Refine = true
  Tool = -> Fusion248002050222
FEATURE [Part::Mirroring] Part__Mirroring038  label="crane-stabilizers-lifter-motor-holder-cover-right"
  Base = (0,0,0)
  Normal = (0,1,0)
  Placement = pos=(0,170,0) rot=(0,0,1;0rad)
  Source = -> Cut014329
FEATURE [Part::Cylinder] Cylinder1375  label="Cylinder1669"
  Angle = 360
  AttacherType = Attacher::AttachEngine3D
  Height = 3
  Placement = pos=(189.75,2.5,-57) rot=(0,0,1;0rad)
  Radius = 8
FEATURE [Part::Cylinder] Cylinder1376  label="crane-stabilizers-cylinder-right-ALU"
  Angle = 360
  AttacherType = Attacher::AttachEngine3D
  Height = 45
  Placement = pos=(189.75,167.5,-50) rot=(0,0,1;0rad)
  Radius = 6
FEATURE [Part::Cylinder] Cylinder1377  label="Cylinder1670"
  Angle = 360
  AttacherType = Attacher::AttachEngine3D
  Height = 5
  Placement = pos=(189.75,2.5,-57) rot=(0,0,1;0rad)
  Radius = 5
FEATURE [Part::MultiFuse] Fusion248002050223
  Refine = true
  Shapes = -> [Cylinder1377,Cylinder1375]
FEATURE [Part::Cylinder] Cylinder1378  label="Cylinder1671"
  Angle = 360
  AttacherType = Attacher::AttachEngine3D
  Height = 4
  Placement = pos=(189.75,2.5,-56) rot=(0,0,1;0rad)
  Radius = 4
FEATURE [Part::Cut] Cut014330  label="crane-stabilizers-foot-right"
  Base = -> Fusion248002050223
  Placement = pos=(0,165,0) rot=(0,0,1;0rad)
  Refine = true
  Tool = -> Cylinder1378
FEATURE [Part::Cylinder] Cylinder1379  label="crane-stabilizers-piston-right-ALU"
  Angle = 360
  AttacherType = Attacher::AttachEngine3D
  Height = 46
  Placement = pos=(189.75,167.5,-56) rot=(0,0,1;0rad)
  Radius = 4
FEATURE [Part::Cylinder] Cylinder1380  label="Cylinder1672"
  Angle = 360
  AttacherType = Attacher::AttachEngine3D
  Height = 45
  Placement = pos=(189.75,2.5,-50) rot=(0,0,1;0rad)
  Radius = 4.9
FEATURE [Part::Cylinder] Cylinder1381  label="Cylinder1673"
  Angle = 360
  AttacherType = Attacher::AttachEngine3D
  Height = 2
  Placement = pos=(189.75,2.5,-52) rot=(0,0,1;0rad)
  Radius = 6
FEATURE [Part::MultiFuse] Fusion248002050224
  Refine = true
  Shapes = -> [Cylinder1381,Cylinder1380]
FEATURE [Part::Cylinder] Cylinder1382  label="Cylinder1674"
  Angle = 360
  AttacherType = Attacher::AttachEngine3D
  Height = 47
  Placement = pos=(189.75,2.5,-52) rot=(0,0,1;0rad)
  Radius = 4.2
FEATURE [Part::Cut] Cut014331
  Base = -> Fusion248002050224
  Refine = true
  Tool = -> Cylinder1382
FEATURE [Part::Box] Box555  label="Cube781"
  AttacherType = Attacher::AttachEngine3D
  Height = 45
  Length = 2
  Placement = pos=(193,1,-48) rot=(0,0,1;0rad)
  Width = 3
FEATURE [Part::Cut] Cut014332  label="crane-stabilizers-inner-chambre-right"
  Base = -> Cut014331
  Placement = pos=(0,165,0) rot=(0,0,1;0rad)
  Refine = true
  Tool = -> Box555
FEATURE [Part::Cut] Cut014333
  Base = -> Fusion248002050096
  Refine = true
  Tool = -> Fusion248002050084
FEATURE [Part::Cut] Cut014334
  Base = -> Cut014333
  Refine = true
  Tool = -> Fillet279
FEATURE [Part::Cut] Cut014335
  Base = -> Cut014334
  Refine = true
  Tool = -> Cylinder1194
FEATURE [Part::Cut] Cut014336
  Base = -> Cut014335
  Refine = true
  Tool = -> Fusion248002050098
FEATURE [Part::Cut] Cut014337
  Base = -> Cut014336
  Placement = pos=(3.5,0,0) rot=(0,0,1;0rad)
  Refine = true
  Tool = -> Fusion248002050126
FEATURE [Part::Box] Box556  label="Cube782"
  AttacherType = Attacher::AttachEngine3D
  Height = 6
  Length = 3.5
  Placement = pos=(188.25,91,5) rot=(0,0,1;0rad)
  Width = 10
FEATURE [Part::MultiFuse] Fusion248002050225
  Refine = true
  Shapes = -> [Box502,Box556]
FEATURE [Part::Cut] Cut014338
  Base = -> Cut014337
  Refine = true
  Tool = -> Fusion248002050225
FEATURE [Part::Cut] Cut014339
  Base = -> Cut014338
  Refine = true
  Tool = -> Fusion248002050188
FEATURE [Part::Chamfer] Chamfer124
  Base = -> Cut014339
  Edges = 1 edges r=3: [Edge193]
FEATURE [Part::Chamfer] Chamfer126  label="crane-mount-main"
  Base = -> Chamfer124
  Edges = 3 edges r=3: [Edge19,Edge21,Edge22]
FEATURE [Part::Box] Box557  label="Cube783"
  AttacherType = Attacher::AttachEngine3D
  Height = 17
  Length = 12
  Placement = pos=(503.5,106,163) rot=(0,0,1;0rad)
  Width = 8
FEATURE [Part::Box] Box558  label="Cube784"
  AttacherType = Attacher::AttachEngine3D
  Height = 17
  Length = 100
  Placement = pos=(415.5,114,163) rot=(0,0,1;0rad)
  Width = 3
FEATURE [Part::Cylinder] Cylinder1383  label="Cylinder1675"
  Angle = 360
  AttacherType = Attacher::AttachEngine3D
  Height = 17
  Placement = pos=(510,118,167) rot=(1,0,0;1.5708rad)
  Radius = 1.6
FEATURE [Part::Cylinder] Cylinder1384  label="Cylinder1676"
  Angle = 360
  AttacherType = Attacher::AttachEngine3D
  Height = 17
  Placement = pos=(418,119,165) rot=(1,0,0;1.5708rad)
  Radius = 1
FEATURE [Part::Cylinder] Cylinder1385  label="Cylinder1677"
  Angle = 360
  AttacherType = Attacher::AttachEngine3D
  Height = 17
  Placement = pos=(418,119,178) rot=(1,0,0;1.5708rad)
  Radius = 1
FEATURE [Part::MultiFuse] Fusion248002050226
  Refine = true
  Shapes = -> [Cylinder1384,Cylinder1385]
FEATURE [Part::Box] Box559  label="Cube785"
  AttacherType = Attacher::AttachEngine3D
  Height = 17
  Length = 4
  Placement = pos=(416,116,163) rot=(0,0,1;0rad)
  Width = 3
FEATURE [Part::Cylinder] Cylinder1386  label="Cylinder1684"
  Angle = 360
  AttacherType = Attacher::AttachEngine3D
  Height = 10
  Placement = pos=(326.5,106,154.5) rot=(-1,0,0;1.5708rad)
  Radius = 1
FEATURE [Part::Cylinder] Cylinder1387  label="Cylinder1685"
  Angle = 360
  AttacherType = Attacher::AttachEngine3D
  Height = 10
  Placement = pos=(326.5,106,167.5) rot=(-1,0,0;1.5708rad)
  Radius = 1
FEATURE [Part::Cylinder] Cylinder1388  label="Cylinder1686"
  Angle = 360
  AttacherType = Attacher::AttachEngine3D
  Height = 4
  Placement = pos=(165,64,180) rot=(0,1,0;1.5708rad)
  Radius = 0.9
FEATURE [Part::Box] Box560  label="Cube786"
  AttacherType = Attacher::AttachEngine3D
  Height = 1
  Length = 4
  Placement = pos=(165,63.1,179) rot=(0,0,1;0rad)
  Width = 1.8
FEATURE [Part::MultiFuse] Fusion248002050227
  Placement = pos=(0,5,0) rot=(0,0,1;0rad)
  Refine = true
  Shapes = -> [Box560,Cylinder1388]
FEATURE [Part::Cylinder] Cylinder1389  label="Cylinder1687"
  Angle = 360
  AttacherType = Attacher::AttachEngine3D
  Height = 4
  Placement = pos=(165,64,180) rot=(0,1,0;1.5708rad)
  Radius = 0.9
FEATURE [Part::Box] Box561  label="Cube787"
  AttacherType = Attacher::AttachEngine3D
  Height = 1
  Length = 4
  Placement = pos=(165,63.1,179) rot=(0,0,1;0rad)
  Width = 1.8
FEATURE [Part::MultiFuse] Fusion248002050228
  Placement = pos=(0,7.5,0) rot=(0,0,1;0rad)
  Refine = true
  Shapes = -> [Box561,Cylinder1389]
FEATURE [Part::Cylinder] Cylinder1390  label="Cylinder1688"
  Angle = 360
  AttacherType = Attacher::AttachEngine3D
  Height = 4
  Placement = pos=(165,64,180) rot=(0,1,0;1.5708rad)
  Radius = 0.9
FEATURE [Part::Box] Box562  label="Cube788"
  AttacherType = Attacher::AttachEngine3D
  Height = 1
  Length = 4
  Placement = pos=(165,63.1,179) rot=(0,0,1;0rad)
  Width = 1.8
FEATURE [Part::MultiFuse] Fusion248002050229
  Placement = pos=(0,10,0) rot=(0,0,1;0rad)
  Refine = true
  Shapes = -> [Box562,Cylinder1390]
FEATURE [Part::Cylinder] Cylinder1391  label="Cylinder1689"
  Angle = 360
  AttacherType = Attacher::AttachEngine3D
  Height = 4
  Placement = pos=(165,64,180) rot=(0,1,0;1.5708rad)
  Radius = 0.9
FEATURE [Part::Box] Box563  label="Cube789"
  AttacherType = Attacher::AttachEngine3D
  Height = 1
  Length = 4
  Placement = pos=(165,63.1,179) rot=(0,0,1;0rad)
  Width = 1.8
FEATURE [Part::MultiFuse] Fusion248002050230
  Placement = pos=(0,12.5,0) rot=(0,0,1;0rad)
  Refine = true
  Shapes = -> [Box563,Cylinder1391]
FEATURE [Part::MultiFuse] Fusion248002050231
  Placement = pos=(91.5,5,10.5) rot=(0,0,1;0rad)
  Refine = true
  Shapes = -> [Cylinder1386,Cylinder1387]
FEATURE [Part::MultiFuse] Fusion248002050232
  Placement = pos=(251,-63.2,244.25) rot=(-1,0,0;1.5708rad)
  Refine = true
  Shapes = -> [Fusion248002050227,Fusion248002050228,Fusion248002050230,Fusion248002050229]
FEATURE [Part::Cut] Cut014340
  Base = -> Box559
  Refine = true
  Tool = -> Fusion248002050232
FEATURE [Part::Cut] Cut014341
  Base = -> Cut014340
  Refine = true
  Tool = -> Fusion248002050231
FEATURE [Part::Fillet] Fillet424  label="crane-extender-arm-bucket-wires-holder_01"
  Base = -> Cut014341
  Edges = 4 edges r=1.99: [Edge18,Edge20,Edge59,Edge64]
  Placement = pos=(0,1,0) rot=(0,0,1;0rad)
FEATURE [Part::MultiFuse] Fusion248002050233
  Refine = true
  Shapes = -> [Box557,Box558]
FEATURE [Part::Chamfer] Chamfer127
  Base = -> Fusion248002050233
  Edges = 1 edges: [Edge15 r1=15 r2=7]
FEATURE [Part::Chamfer] Chamfer128
  Base = -> Chamfer127
  Edges = 1 edges: [Edge20 r1=10 r2=4]
FEATURE [Part::Cylinder] Cylinder1392  label="Cylinder1690"
  Angle = 360
  AttacherType = Attacher::AttachEngine3D
  Height = 17
  Placement = pos=(510,118,154) rot=(1,0,0;1.5708rad)
  Radius = 1.6
FEATURE [Part::Box] Box564  label="Cube790"
  AttacherType = Attacher::AttachEngine3D
  Height = 17
  Length = 9
  Placement = pos=(505.5,106,151) rot=(0,0,1;0rad)
  Width = 2
FEATURE [Part::MultiFuse] Fusion248002050234
  Refine = true
  Shapes = -> [Chamfer128,Box564]
FEATURE [Part::Fillet] Fillet425
  Base = -> Fusion248002050234
  Edges = 2 edges r=3: [Edge1,Edge3]
FEATURE [Part::Cylinder] Cylinder1393  label="Cylinder1691"
  Angle = 360
  AttacherType = Attacher::AttachEngine3D
  Height = 5
  Placement = pos=(510,115,167) rot=(1,0,0;1.5708rad)
  Radius = 3.1
FEATURE [Part::MultiFuse] Fusion248002050235
  Refine = true
  Shapes = -> [Cylinder1392,Cylinder1383,Cylinder1393]
FEATURE [Part::Cylinder] Cylinder1394  label="Cylinder1694"
  Angle = 360
  AttacherType = Attacher::AttachEngine3D
  Height = 17
  Placement = pos=(418,119,165) rot=(1,0,0;1.5708rad)
  Radius = 1
FEATURE [Part::Cylinder] Cylinder1395  label="Cylinder1695"
  Angle = 360
  AttacherType = Attacher::AttachEngine3D
  Height = 17
  Placement = pos=(418,119,178) rot=(1,0,0;1.5708rad)
  Radius = 1
FEATURE [Part::MultiFuse] Fusion248002050236
  Placement = pos=(79,0,0) rot=(0,0,1;0rad)
  Refine = true
  Shapes = -> [Cylinder1394,Cylinder1395]
FEATURE [Part::Box] Box565  label="Cube791"
  AttacherType = Attacher::AttachEngine3D
  Height = 17
  Length = 4
  Placement = pos=(416,116,163) rot=(0,0,1;0rad)
  Width = 3
FEATURE [Part::Cylinder] Cylinder1396  label="Cylinder1702"
  Angle = 360
  AttacherType = Attacher::AttachEngine3D
  Height = 10
  Placement = pos=(326.5,106,154.5) rot=(-1,0,0;1.5708rad)
  Radius = 1
FEATURE [Part::Cylinder] Cylinder1397  label="Cylinder1703"
  Angle = 360
  AttacherType = Attacher::AttachEngine3D
  Height = 10
  Placement = pos=(326.5,106,167.5) rot=(-1,0,0;1.5708rad)
  Radius = 1
FEATURE [Part::Cylinder] Cylinder1398  label="Cylinder1704"
  Angle = 360
  AttacherType = Attacher::AttachEngine3D
  Height = 4
  Placement = pos=(165,64,180) rot=(0,1,0;1.5708rad)
  Radius = 0.9
FEATURE [Part::Box] Box566  label="Cube792"
  AttacherType = Attacher::AttachEngine3D
  Height = 1
  Length = 4
  Placement = pos=(165,63.1,179) rot=(0,0,1;0rad)
  Width = 1.8
FEATURE [Part::MultiFuse] Fusion248002050237
  Placement = pos=(0,5,0) rot=(0,0,1;0rad)
  Refine = true
  Shapes = -> [Box566,Cylinder1398]
FEATURE [Part::Cylinder] Cylinder1399  label="Cylinder1705"
  Angle = 360
  AttacherType = Attacher::AttachEngine3D
  Height = 4
  Placement = pos=(165,64,180) rot=(0,1,0;1.5708rad)
  Radius = 0.9
FEATURE [Part::Box] Box567  label="Cube793"
  AttacherType = Attacher::AttachEngine3D
  Height = 1
  Length = 4
  Placement = pos=(165,63.1,179) rot=(0,0,1;0rad)
  Width = 1.8
FEATURE [Part::MultiFuse] Fusion248002050238
  Placement = pos=(0,7.5,0) rot=(0,0,1;0rad)
  Refine = true
  Shapes = -> [Box567,Cylinder1399]
FEATURE [Part::Cylinder] Cylinder1400  label="Cylinder1706"
  Angle = 360
  AttacherType = Attacher::AttachEngine3D
  Height = 4
  Placement = pos=(165,64,180) rot=(0,1,0;1.5708rad)
  Radius = 0.9
FEATURE [Part::Box] Box568  label="Cube794"
  AttacherType = Attacher::AttachEngine3D
  Height = 1
  Length = 4
  Placement = pos=(165,63.1,179) rot=(0,0,1;0rad)
  Width = 1.8
FEATURE [Part::MultiFuse] Fusion248002050239
  Placement = pos=(0,10,0) rot=(0,0,1;0rad)
  Refine = true
  Shapes = -> [Box568,Cylinder1400]
FEATURE [Part::Cylinder] Cylinder1401  label="Cylinder1707"
  Angle = 360
  AttacherType = Attacher::AttachEngine3D
  Height = 4
  Placement = pos=(165,64,180) rot=(0,1,0;1.5708rad)
  Radius = 0.9
FEATURE [Part::Box] Box569  label="Cube795"
  AttacherType = Attacher::AttachEngine3D
  Height = 1
  Length = 4
  Placement = pos=(165,63.1,179) rot=(0,0,1;0rad)
  Width = 1.8
FEATURE [Part::MultiFuse] Fusion248002050240
  Placement = pos=(0,12.5,0) rot=(0,0,1;0rad)
  Refine = true
  Shapes = -> [Box569,Cylinder1401]
FEATURE [Part::MultiFuse] Fusion248002050241
  Placement = pos=(91.5,5,10.5) rot=(0,0,1;0rad)
  Refine = true
  Shapes = -> [Cylinder1396,Cylinder1397]
FEATURE [Part::MultiFuse] Fusion248002050242
  Placement = pos=(251,-63.2,244.25) rot=(-1,0,0;1.5708rad)
  Refine = true
  Shapes = -> [Fusion248002050237,Fusion248002050238,Fusion248002050240,Fusion248002050239]
FEATURE [Part::Cut] Cut014344
  Base = -> Box565
  Refine = true
  Tool = -> Fusion248002050242
FEATURE [Part::Cut] Cut014345
  Base = -> Cut014344
  Refine = true
  Tool = -> Fusion248002050241
FEATURE [Part::Fillet] Fillet427  label="crane-extender-arm-bucket-wires-holder"
  Base = -> Cut014345
  Edges = 4 edges r=1.99: [Edge18,Edge20,Edge59,Edge64]
  Placement = pos=(79,1,0) rot=(0,0,1;0rad)
FEATURE [Part::Cut] Cut014346
  Base = -> Fillet425
  Refine = true
  Tool = -> Fusion248002050235
FEATURE [Part::Cylinder] Cylinder1402  label="Cylinder1710"
  Angle = 360
  AttacherType = Attacher::AttachEngine3D
  Height = 3
  Placement = pos=(418,119,165) rot=(1,0,0;1.5708rad)
  Radius = 2
FEATURE [Part::Cylinder] Cylinder1403  label="Cylinder1711"
  Angle = 360
  AttacherType = Attacher::AttachEngine3D
  Height = 3
  Placement = pos=(418,119,178) rot=(1,0,0;1.5708rad)
  Radius = 2
FEATURE [Part::MultiFuse] Fusion248002050243
  Placement = pos=(0,-2,0) rot=(0,0,1;0rad)
  Refine = true
  Shapes = -> [Cylinder1402,Cylinder1403]
FEATURE [Part::Chamfer] Chamfer129
  Base = -> Cut014346
  Edges = 1 edges r=2: [Edge49]
FEATURE [Part::MultiFuse] Fusion248002050244
  Refine = true
  Shapes = -> [Fusion248002050243,Chamfer129]
FEATURE [Part::MultiFuse] Fusion248002050245
  Refine = true
  Shapes = -> [Fusion248002050236,Fusion248002050226]
FEATURE [Part::Cut] Cut014347  label="crane-extender-arm-bucket-wires-plate"
  Base = -> Fusion248002050244
  Refine = true
  Tool = -> Fusion248002050245
FEATURE [Part::Cylinder] Cylinder1404  label="Cylinder1717"
  Angle = 360
  AttacherType = Attacher::AttachEngine3D
  Height = 27
  Radius = 8
FEATURE [Part::Box] Box570  label="Cube796"
  AttacherType = Attacher::AttachEngine3D
  Height = 27
  Length = 10.4
  Placement = pos=(-5.2,-6.2,0) rot=(0,0,1;0rad)
  Width = 12.4
FEATURE [Part::Cylinder] Cylinder1405  label="Cylinder1718"
  Angle = 360
  AttacherType = Attacher::AttachEngine3D
  Height = 17
  Radius = 8
FEATURE [Part::Cylinder] Cylinder1406  label="Cylinder1719"
  Angle = 360
  AttacherType = Attacher::AttachEngine3D
  Height = 17
  Radius = 6.5
FEATURE [Part::Cut] Cut014348
  Base = -> Cylinder1405
  Refine = true
  Tool = -> Cylinder1406
FEATURE [Part::Fillet] Fillet428
  Base = -> Box570
  Edges = 4 edges r=1: [Edge1,Edge3,Edge5,Edge7]
FEATURE [Part::Cut] Cut014349
  Base = -> Cylinder1404
  Refine = true
  Tool = -> Fillet428
FEATURE [Part::MultiFuse] Fusion248002050246
  Refine = true
  Shapes = -> [Cut014348,Cut014349]
FEATURE [Part::Cylinder] Cylinder1407  label="Cylinder1720"
  Angle = 360
  AttacherType = Attacher::AttachEngine3D
  Height = 27
  Radius = 8
FEATURE [Part::Cut] Cut014350  label="cylinder-motor-supports-004"
  Base = -> Cylinder1407
  Placement = pos=(175,114,18) rot=(-1,0,0;1.5708rad)
  Refine = true
  Tool = -> Fusion248002050246
FEATURE [Part::Cylinder] Cylinder1408  label="Cylinder1721"
  Angle = 360
  AttacherType = Attacher::AttachEngine3D
  Height = 60
  Placement = pos=(175,195,18) rot=(1,0,0;1.5708rad)
  Radius = 1.5
FEATURE [Part::MultiFuse] Fusion248002050247  label="crane-stabilizers-lifter-motor-left"
  Placement = pos=(207.75,-172.5,139) rot=(0.57735,0.57735,-0.57735;4.18879rad)
  Refine = true
  Shapes = -> [Cut014350,Cylinder1408]
FEATURE [Part::Cylinder] Cylinder1409  label="Cylinder1727"
  Angle = 360
  AttacherType = Attacher::AttachEngine3D
  Height = 27
  Radius = 8
FEATURE [Part::Box] Box571  label="Cube797"
  AttacherType = Attacher::AttachEngine3D
  Height = 27
  Length = 10.4
  Placement = pos=(-5.2,-6.2,0) rot=(0,0,1;0rad)
  Width = 12.4
FEATURE [Part::Cylinder] Cylinder1410  label="Cylinder1728"
  Angle = 360
  AttacherType = Attacher::AttachEngine3D
  Height = 17
  Radius = 8
FEATURE [Part::Cylinder] Cylinder1411  label="Cylinder1729"
  Angle = 360
  AttacherType = Attacher::AttachEngine3D
  Height = 17
  Radius = 6.5
FEATURE [Part::Cut] Cut014351
  Base = -> Cylinder1410
  Refine = true
  Tool = -> Cylinder1411
FEATURE [Part::Fillet] Fillet429
  Base = -> Box571
  Edges = 4 edges r=1: [Edge1,Edge3,Edge5,Edge7]
FEATURE [Part::Cut] Cut014352
  Base = -> Cylinder1409
  Refine = true
  Tool = -> Fillet429
FEATURE [Part::MultiFuse] Fusion248002050248
  Refine = true
  Shapes = -> [Cut014351,Cut014352]
FEATURE [Part::Cylinder] Cylinder1412  label="Cylinder1730"
  Angle = 360
  AttacherType = Attacher::AttachEngine3D
  Height = 27
  Radius = 8
FEATURE [Part::Cut] Cut014353  label="cylinder-motor-supports-005"
  Base = -> Cylinder1412
  Placement = pos=(175,114,18) rot=(-1,0,0;1.5708rad)
  Refine = true
  Tool = -> Fusion248002050248
FEATURE [Part::Cylinder] Cylinder1413  label="Cylinder1731"
  Angle = 360
  AttacherType = Attacher::AttachEngine3D
  Height = 60
  Placement = pos=(175,195,18) rot=(1,0,0;1.5708rad)
  Radius = 1.5
FEATURE [Part::MultiFuse] Fusion248002050249  label="crane-stabilizers-lifter-motor-right"
  Placement = pos=(207.75,-7.5,139) rot=(0.57735,0.57735,-0.57735;4.18879rad)
  Refine = true
  Shapes = -> [Cut014353,Cylinder1413]
FEATURE [Part::Box] Box572  label="Cube798"
  AttacherType = Attacher::AttachEngine3D
  Height = 2
  Length = 14
  Placement = pos=(180,-2.6,23) rot=(0,0,1;0rad)
  Width = 5
FEATURE [Part::Box] Box573  label="Cube799"
  AttacherType = Attacher::AttachEngine3D
  Height = 2
  Length = 14
  Placement = pos=(180,167.6,23) rot=(0,0,1;0rad)
  Width = 5
FEATURE [Part::Cut] Cut014354  label="crane-stabilizers-lifter-motor-holder-left-01"
  Base = -> Cut014320
  Refine = true
  Tool = -> Box572
FEATURE [Part::Cut] Cut014355  label="crane-stabilizers-lifter-motor-holder-right-01"
  Base = -> Cut014325
  Refine = true
  Tool = -> Box573
FEATURE [App::DocumentObjectGroup] Group004  label="stabilizers"
  Group = -> [Fusion248002050037,Fusion248002050038,Fusion248002050085,Cut493,Cut014250,Cylinder1296,Cut014300,Cylinder1299,Cut014302,Cut014319,Cylinder1344,Cylinder1345,Part__Mirroring038,Cylinder1376,Cut014330,Cylinder1379,Cut014332,Chamfer126,Fusion248002050247,Fusion248002050249,Cut014354,Cut014355]
FEATURE [Part::Box] Box575  label="Cube801"
  AttacherType = Attacher::AttachEngine3D
  Height = 3
  Length = 4
  Placement = pos=(169.5,60.5,179) rot=(0,0,1;0rad)
  Width = 28
FEATURE [Part::Cylinder] Cylinder1414  label="Cylinder1742"
  Angle = 360
  AttacherType = Attacher::AttachEngine3D
  Height = 10
  Placement = pos=(-7,3,30) rot=(0,0,1;0rad)
  Radius = 1.1
FEATURE [Part::Cylinder] Cylinder1415  label="Cylinder1743"
  Angle = 360
  AttacherType = Attacher::AttachEngine3D
  Height = 10
  Placement = pos=(-7,26,30) rot=(0,0,1;0rad)
  Radius = 1.1
FEATURE [Part::MultiFuse] Fusion248002050250
  Placement = pos=(178.5,60,147) rot=(0,0,1;0rad)
  Refine = true
  Shapes = -> [Cylinder1415,Cylinder1414]
FEATURE [Part::Cut] Cut014356
  Base = -> Box575
  Refine = true
  Tool = -> Fusion248002050250
FEATURE [Part::Box] Box576  label="Cube802"
  AttacherType = Attacher::AttachEngine3D
  Height = 1.5
  Length = 4
  Placement = pos=(119.5,96.1,42) rot=(0,0,1;0rad)
  Width = 3.5
FEATURE [Part::Fillet] Fillet430
  Base = -> Cut014356
  Edges = 4 edges r=1.99: [Edge1,Edge3,Edge6,Edge13]
  Placement = pos=(-50,26,-137) rot=(0,0,1;0rad)
FEATURE [Part::Fillet] Fillet431
  Base = -> Box576
  Edges = 2 edges r=0.75: [Edge10,Edge12]
  Placement = pos=(0,-5,0) rot=(0,0,1;0rad)
FEATURE [Part::Box] Box577  label="Cube803"
  AttacherType = Attacher::AttachEngine3D
  Height = 1.5
  Length = 4
  Placement = pos=(119.5,96.1,42) rot=(0,0,1;0rad)
  Width = 3.5
FEATURE [Part::Fillet] Fillet432
  Base = -> Box577
  Edges = 2 edges r=0.75: [Edge10,Edge12]
  Placement = pos=(0,-1,0) rot=(0,0,1;0rad)
FEATURE [Part::Box] Box578  label="Cube804"
  AttacherType = Attacher::AttachEngine3D
  Height = 1.5
  Length = 4
  Placement = pos=(119.5,96.1,42) rot=(0,0,1;0rad)
  Width = 3.5
FEATURE [Part::Fillet] Fillet433
  Base = -> Box578
  Edges = 2 edges r=0.75: [Edge10,Edge12]
  Placement = pos=(0,3,0) rot=(0,0,1;0rad)
FEATURE [Part::Box] Box579  label="Cube805"
  AttacherType = Attacher::AttachEngine3D
  Height = 1.5
  Length = 4
  Placement = pos=(119.5,96.1,42) rot=(0,0,1;0rad)
  Width = 3.5
FEATURE [Part::Fillet] Fillet434
  Base = -> Box579
  Edges = 2 edges r=0.75: [Edge10,Edge12]
  Placement = pos=(0,7,0) rot=(0,0,1;0rad)
FEATURE [Part::Box] Box580  label="Cube806"
  AttacherType = Attacher::AttachEngine3D
  Height = 1.5
  Length = 4
  Placement = pos=(119.5,96.1,42) rot=(0,0,1;0rad)
  Width = 3.5
FEATURE [Part::Fillet] Fillet435
  Base = -> Box580
  Edges = 2 edges r=0.75: [Edge10,Edge12]
  Placement = pos=(0,11,0) rot=(0,0,1;0rad)
FEATURE [Part::MultiFuse] Fusion248002050251
  Placement = pos=(0,-0.375,0) rot=(0,0,1;0rad)
  Refine = true
  Shapes = -> [Fillet435,Fillet432,Fillet433,Fillet434,Fillet431]
FEATURE [Part::Cut] Cut014357  label="crane-main-arm-wires-holder-upper"
  Base = -> Fillet430
  Refine = true
  Tool = -> Fusion248002050251
FEATURE [Part::Box] Box581  label="Cube807"
  AttacherType = Attacher::AttachEngine3D
  Height = 3
  Length = 4
  Placement = pos=(169.5,60.5,179) rot=(0,0,1;0rad)
  Width = 28
FEATURE [Part::Cylinder] Cylinder1416  label="Cylinder1746"
  Angle = 360
  AttacherType = Attacher::AttachEngine3D
  Height = 10
  Placement = pos=(-7,3,30) rot=(0,0,1;0rad)
  Radius = 0.9
FEATURE [Part::Cylinder] Cylinder1417  label="Cylinder1747"
  Angle = 360
  AttacherType = Attacher::AttachEngine3D
  Height = 10
  Placement = pos=(-7,26,30) rot=(0,0,1;0rad)
  Radius = 0.9
FEATURE [Part::MultiFuse] Fusion248002050252
  Placement = pos=(178.5,60,147) rot=(0,0,1;0rad)
  Refine = true
  Shapes = -> [Cylinder1417,Cylinder1416]
FEATURE [Part::Cut] Cut014358
  Base = -> Box581
  Refine = true
  Tool = -> Fusion248002050252
FEATURE [Part::Fillet] Fillet436
  Base = -> Cut014358
  Edges = 4 edges r=1.99: [Edge1,Edge3,Edge6,Edge13]
  Placement = pos=(-50,26,-137) rot=(0,0,1;0rad)
FEATURE [Part::Box] Box586  label="Cube812"
  AttacherType = Attacher::AttachEngine3D
  Height = 1.5
  Length = 4
  Placement = pos=(119.5,96.1,42) rot=(0,0,1;0rad)
  Width = 3.5
FEATURE [Part::Fillet] Fillet437
  Base = -> Box586
  Edges = 2 edges r=0.75: [Edge9,Edge11]
  Placement = pos=(0,-5.375,1.5) rot=(0,0,1;0rad)
FEATURE [Part::Box] Box587  label="Cube813"
  AttacherType = Attacher::AttachEngine3D
  Height = 1.5
  Length = 4
  Placement = pos=(119.5,96.1,42) rot=(0,0,1;0rad)
  Width = 3.5
FEATURE [Part::Fillet] Fillet438
  Base = -> Box587
  Edges = 2 edges r=0.75: [Edge9,Edge11]
  Placement = pos=(0,-1.375,1.5) rot=(0,0,1;0rad)
FEATURE [Part::Box] Box588  label="Cube814"
  AttacherType = Attacher::AttachEngine3D
  Height = 1.5
  Length = 4
  Placement = pos=(119.5,96.1,42) rot=(0,0,1;0rad)
  Width = 3.5
FEATURE [Part::Fillet] Fillet439
  Base = -> Box588
  Edges = 2 edges r=0.75: [Edge9,Edge11]
  Placement = pos=(0,2.625,1.5) rot=(0,0,1;0rad)
FEATURE [Part::Box] Box589  label="Cube815"
  AttacherType = Attacher::AttachEngine3D
  Height = 1.5
  Length = 4
  Placement = pos=(119.5,96.1,42) rot=(0,0,1;0rad)
  Width = 3.5
FEATURE [Part::Fillet] Fillet440
  Base = -> Box589
  Edges = 2 edges r=0.75: [Edge9,Edge11]
  Placement = pos=(0,6.625,1.5) rot=(0,0,1;0rad)
FEATURE [Part::Box] Box590  label="Cube816"
  AttacherType = Attacher::AttachEngine3D
  Height = 1.5
  Length = 4
  Placement = pos=(119.5,96.1,42) rot=(0,0,1;0rad)
  Width = 3.5
FEATURE [Part::Fillet] Fillet441
  Base = -> Box590
  Edges = 2 edges r=0.75: [Edge9,Edge11]
  Placement = pos=(0,10.625,1.5) rot=(0,0,1;0rad)
FEATURE [Part::MultiFuse] Fusion248002050253
  Refine = true
  Shapes = -> [Fillet437,Fillet438,Fillet441,Fillet440,Fillet439]
FEATURE [Part::Cut] Cut014359  label="crane-main-arm-wires-holder-lower"
  Base = -> Fillet436
  Placement = pos=(0,0,-3) rot=(0,0,1;0rad)
  Refine = true
  Tool = -> Fusion248002050253
FEATURE [Part::Feature] Cut078001  label="crane-extender-arm001"
  Placement = pos=(454.5,60,-4.5) rot=(0,-1,0;1.5708rad)
  shape: bbox 200 x 17 x 44.39 mm, 142 faces (baked)
FEATURE [Part::Feature] Cut078002  label="crane-extender-arm002"
  Placement = pos=(454.5,60,-4.5) rot=(0,-1,0;1.5708rad)
  shape: bbox 200 x 17 x 44.39 mm, 142 faces (baked)
FEATURE [Part::Feature] Cut078003  label="crane-extender-arm003"
  Placement = pos=(454.5,60,-4.5) rot=(0,-1,0;1.5708rad)
  shape: bbox 200 x 17 x 44.39 mm, 142 faces (baked)
FEATURE [Part::Feature] Cut078004  label="crane-extender-arm004"
  Placement = pos=(454.5,60,-4.5) rot=(0,-1,0;1.5708rad)
  shape: bbox 200 x 17 x 44.39 mm, 142 faces (baked)
FEATURE [Part::Box] Box593  label="Cube819"
  AttacherType = Attacher::AttachEngine3D
  Height = 208
  Length = 48
  Placement = pos=(302,86.75,199.75) rot=(0,1,0;1.5708rad)
  Width = 17
FEATURE [Part::Cut] Cut078007
  Base = -> Cut078003
  Refine = true
  Tool = -> Box593
FEATURE [Part::Box] Box595  label="Cube821"
  AttacherType = Attacher::AttachEngine3D
  Height = 208
  Length = 48
  Placement = pos=(302,93.25,199.75) rot=(0,1,0;1.5708rad)
  Width = 17
FEATURE [Part::Box] Box596  label="Cube822"
  AttacherType = Attacher::AttachEngine3D
  Height = 208
  Length = 48
  Placement = pos=(302,87.75,229.5) rot=(0,1,0;1.5708rad)
  Width = 22
FEATURE [Part::Cut] Cut078008  label="crane-extender-arm-inner"
  Base = -> Cut078007
  Refine = true
  Tool = -> Box596
FEATURE [Part::Box] Box597  label="Cube823"
  AttacherType = Attacher::AttachEngine3D
  Height = 208
  Length = 48
  Placement = pos=(302,87.75,229.5) rot=(0,1,0;1.5708rad)
  Width = 22
FEATURE [Part::Cut] Cut078009
  Base = -> Cut078001
  Refine = true
  Tool = -> Box595
FEATURE [Part::Cut] Cut078010  label="crane-extender-arm-outer"
  Base = -> Cut078009
  Refine = true
  Tool = -> Box597
FEATURE [Part::Box] Box598  label="Cube824"
  AttacherType = Attacher::AttachEngine3D
  Height = 208
  Length = 48
  Placement = pos=(302,87.75,177.25) rot=(0,1,0;1.5708rad)
  Width = 22
FEATURE [Part::Box] Box599  label="Cube825"
  AttacherType = Attacher::AttachEngine3D
  Height = 208
  Length = 48
  Placement = pos=(302,103.75,199.75) rot=(0,1,0;1.5708rad)
  Width = 17
FEATURE [Part::Box] Box600  label="Cube826"
  AttacherType = Attacher::AttachEngine3D
  Height = 208
  Length = 48
  Placement = pos=(302,76.25,199.75) rot=(0,1,0;1.5708rad)
  Width = 17
FEATURE [Part::MultiFuse] Fusion248002050254
  Refine = true
  Shapes = -> [Box598,Box600,Box599]
FEATURE [Part::Cut] Cut078011  label="crane-extender-arm-upper"
  Base = -> Cut078004
  Refine = true
  Tool = -> Fusion248002050254
FEATURE [Part::Box] Box601  label="Cube827"
  AttacherType = Attacher::AttachEngine3D
  Height = 208
  Length = 48
  Placement = pos=(302,87.75,204.75) rot=(0,1,0;1.5708rad)
  Width = 22
FEATURE [Part::Box] Box602  label="Cube828"
  AttacherType = Attacher::AttachEngine3D
  Height = 208
  Length = 48
  Placement = pos=(302,76.25,199.75) rot=(0,1,0;1.5708rad)
  Width = 17
FEATURE [Part::Box] Box603  label="Cube829"
  AttacherType = Attacher::AttachEngine3D
  Height = 208
  Length = 48
  Placement = pos=(302,103.75,199.75) rot=(0,1,0;1.5708rad)
  Width = 17
FEATURE [Part::MultiFuse] Fusion248002050255
  Refine = true
  Shapes = -> [Box601,Box602,Box603]
FEATURE [Part::Cut] Cut078012  label="crane-extender-arm-lower"
  Base = -> Cut078002
  Refine = true
  Tool = -> Fusion248002050255
FEATURE [App::DocumentObjectGroup] Group003  label="extender-arm"
  Group = -> [Cut436,Cut450,Cut452,Fusion248002050028,Cut454,Cylinder249,Chamfer111,Cut073,Cut072,Cylinder175,Cylinder087,Cut014286,Fillet424,Fillet427,Cut014347,Cut078008,Cut078010,Cut078011,Cut078012]
FEATURE [Part::Box] Box604  label="Cube830"
  AttacherType = Attacher::AttachEngine3D
  Height = 30
  Length = 35.5
  Placement = pos=(155.75,59.75,30) rot=(0,0,1;0rad)
  Width = 25.5
FEATURE [Part::Box] Box605  label="Cube831"
  AttacherType = Attacher::AttachEngine3D
  Height = 125
  Length = 30
  Placement = pos=(155.75,59.75,33) rot=(0,-1,0;0.20944rad)
  Width = 25.5
FEATURE [Part::Box] Box606  label="Cube832"
  AttacherType = Attacher::AttachEngine3D
  Height = 30
  Length = 25.5
  Placement = pos=(155.75,59.75,28) rot=(0,0,1;0rad)
  Width = 25.5
FEATURE [Part::MultiFuse] Fusion248002050256
  Refine = true
  Shapes = -> [Box604,Box606,Box605]
FEATURE [Part::Fillet] Fillet442
  Base = -> Fusion248002050256
  Edges = 1 edges r=5.25: [Edge16]
  Placement = pos=(7,0,4.75) rot=(0,0,1;0rad)
FEATURE [Part::Cylinder] Cylinder1418  label="Cylinder1748"
  Angle = 360
  AttacherType = Attacher::AttachEngine3D
  Height = 2.5
  Placement = pos=(9,18,-2) rot=(0,0,1;0rad)
  Radius = 3
FEATURE [Part::Cylinder] Cylinder1419  label="Cylinder1749"
  Angle = 360
  AttacherType = Attacher::AttachEngine3D
  Height = 12
  Placement = pos=(13,12.5,-3) rot=(0,0,1;0rad)
  Radius = 2.5
FEATURE [Part::Cylinder] Cylinder1420  label="Cylinder1678"
  Angle = 360
  AttacherType = Attacher::AttachEngine3D
  Height = 11
  Placement = pos=(9,18,-2) rot=(0,0,1;0rad)
  Radius = 1.25
FEATURE [Part::Cylinder] Cylinder1421  label="Cylinder1679"
  Angle = 360
  AttacherType = Attacher::AttachEngine3D
  Height = 11
  Placement = pos=(9,7,-2) rot=(0,0,1;0rad)
  Radius = 1.25
FEATURE [Part::Cylinder] Cylinder1422  label="Cylinder1680"
  Angle = 360
  AttacherType = Attacher::AttachEngine3D
  Height = 11
  Placement = pos=(18,18,-2) rot=(0,0,1;0rad)
  Radius = 1.25
FEATURE [Part::Cylinder] Cylinder1423  label="Cylinder1681"
  Angle = 360
  AttacherType = Attacher::AttachEngine3D
  Height = 11
  Placement = pos=(18,7,-2) rot=(0,0,1;0rad)
  Radius = 1.25
FEATURE [Part::MultiFuse] Fusion248002050257
  Placement = pos=(150,60,25) rot=(0,0,1;0rad)
  Refine = true
  Shapes = -> [Cylinder1419,Cylinder1420,Cylinder1421,Cylinder1423,Cylinder1422]
FEATURE [Part::Cylinder] Cylinder1424  label="Cylinder1682"
  Angle = 360
  AttacherType = Attacher::AttachEngine3D
  Height = 2.5
  Placement = pos=(9,7,-2) rot=(0,0,1;0rad)
  Radius = 3
FEATURE [Part::Cylinder] Cylinder1425  label="Cylinder1683"
  Angle = 360
  AttacherType = Attacher::AttachEngine3D
  Height = 2.5
  Placement = pos=(18,18,-2) rot=(0,0,1;0rad)
  Radius = 3
FEATURE [Part::Cylinder] Cylinder1426  label="Cylinder1750"
  Angle = 360
  AttacherType = Attacher::AttachEngine3D
  Height = 2.5
  Placement = pos=(18,7,-2) rot=(0,0,1;0rad)
  Radius = 3
FEATURE [Part::MultiFuse] Fusion248002050258
  Placement = pos=(150,60,28.5) rot=(0,0,1;0rad)
  Refine = true
  Shapes = -> [Cylinder1418,Cylinder1424,Cylinder1425,Cylinder1426]
FEATURE [Part::MultiFuse] Fusion248002050259
  Placement = pos=(12,0,2) rot=(0,0,1;0rad)
  Refine = true
  Shapes = -> [Fusion248002050257,Fusion248002050258]
FEATURE [Part::Feature] _9T001_solid002  label="_9T001 (Solid)002"
  shape: large baked B-rep (56 MB .brp); summary skipped
FEATURE [Part::MultiFuse] Fusion248002050260
  Refine = true
  Shapes = -> [Fusion248002050259,Fillet442]
FEATURE [Part::Cut] Cut078013  label="crane-rotating-gear-wormscrew"
  Base = -> _9T001_solid002
  Refine = true
  Tool = -> Fusion248002050260
FEATURE [Part::Box] Box607  label="Cube833"
  AttacherType = Attacher::AttachEngine3D
  Height = 11
  Length = 31
  Placement = pos=(150.5,52,17) rot=(0,0,1;0rad)
  Width = 6
FEATURE [Part::Cylinder] Cylinder1427  label="Cylinder1751"
  Angle = 360
  AttacherType = Attacher::AttachEngine3D
  Height = 10
  Placement = pos=(143,55,32) rot=(0,1,0;1.5708rad)
  Radius = 1.25
FEATURE [Part::Cylinder] Cylinder1428  label="Cylinder1693"
  Angle = 360
  AttacherType = Attacher::AttachEngine3D
  Height = 10
  Placement = pos=(172.75,119,20) rot=(1,0,0;1.5708rad)
  Radius = 1.6
FEATURE [Part::Box] Box608  label="Cube834"
  AttacherType = Attacher::AttachEngine3D
  Height = 20
  Length = 18
  Placement = pos=(143,52,19) rot=(0,0,1;0rad)
  Width = 6
FEATURE [Part::MultiFuse] Fusion248002050261
  Refine = true
  Shapes = -> [Box607,Box608]
FEATURE [Part::Cylinder] Cylinder1429  label="Cylinder1752"
  Angle = 360
  AttacherType = Attacher::AttachEngine3D
  Height = 10
  Placement = pos=(164.5,62,24) rot=(1,0,0;1.5708rad)
  Radius = 1.6
FEATURE [Part::Cylinder] Cylinder1430  label="Cylinder1692"
  Angle = 360
  AttacherType = Attacher::AttachEngine3D
  Height = 10
  Placement = pos=(177.5,62,24) rot=(1,0,0;1.5708rad)
  Radius = 1.6
FEATURE [Part::MultiFuse] Fusion248002050262
  Placement = pos=(0.25,0,0) rot=(0,0,1;0rad)
  Refine = true
  Shapes = -> [Cylinder1430,Cylinder1429]
FEATURE [Part::Cut] Cut078017
  Base = -> Fusion248002050261
  Refine = true
  Tool = -> Fusion248002050262
FEATURE [Part::Cylinder] Cylinder1431  label="Cylinder1753"
  Angle = 360
  AttacherType = Attacher::AttachEngine3D
  Height = 20
  Placement = pos=(152,46,31.5) rot=(-1,0,0;1.5708rad)
  Radius = 6.15
FEATURE [Part::Cut] Cut078016
  Base = -> Cut078017
  Refine = true
  Tool = -> Cylinder1431
FEATURE [Part::Cut] Cut078015
  Base = -> Cut078016
  Refine = true
  Tool = -> Cylinder1427
FEATURE [Part::Chamfer] Chamfer130
  Base = -> Cut078015
  Edges = 1 edges r=1.999: [Edge4]
FEATURE [Part::Chamfer] Chamfer131
  Base = -> Chamfer130
  Edges = 1 edges r=7.499: [Edge19]
FEATURE [Part::Fillet] Fillet443
  Base = -> Chamfer131
  Edges = 1 edges r=10: [Edge17]
FEATURE [Part::Fillet] Fillet444
  Base = -> Fillet443
  Edges = 2 edges r=5: [Edge22,Edge28]
  Placement = pos=(0,61,0) rot=(0,0,1;0rad)
FEATURE [Part::Cut] Cut078014  label="crane-rotating-cylinder-holder-right-thick"
  Base = -> Fillet444
  Placement = pos=(-0.25,0,0) rot=(0,0,1;0rad)
  Refine = true
  Tool = -> Cylinder1428
FEATURE [Part::Box] Box609  label="Cube835"
  AttacherType = Attacher::AttachEngine3D
  Height = 11
  Length = 31
  Placement = pos=(150.5,52,17) rot=(0,0,1;0rad)
  Width = 6
FEATURE [Part::Cylinder] Cylinder1432  label="Cylinder1754"
  Angle = 360
  AttacherType = Attacher::AttachEngine3D
  Height = 10
  Placement = pos=(143,55,32) rot=(0,1,0;1.5708rad)
  Radius = 1.25
FEATURE [Part::Box] Box610  label="Cube836"
  AttacherType = Attacher::AttachEngine3D
  Height = 20
  Length = 18
  Placement = pos=(143,52,19) rot=(0,0,1;0rad)
  Width = 6
FEATURE [Part::MultiFuse] Fusion248002050263
  Refine = true
  Shapes = -> [Box609,Box610]
FEATURE [Part::Cylinder] Cylinder1433  label="Cylinder1755"
  Angle = 360
  AttacherType = Attacher::AttachEngine3D
  Height = 10
  Placement = pos=(164.5,62,24) rot=(1,0,0;1.5708rad)
  Radius = 1.6
FEATURE [Part::Cylinder] Cylinder1434  label="Cylinder1696"
  Angle = 360
  AttacherType = Attacher::AttachEngine3D
  Height = 10
  Placement = pos=(177.5,62,24) rot=(1,0,0;1.5708rad)
  Radius = 1.6
FEATURE [Part::MultiFuse] Fusion248002050264
  Placement = pos=(0.25,0,0) rot=(0,0,1;0rad)
  Refine = true
  Shapes = -> [Cylinder1434,Cylinder1433]
FEATURE [Part::Cut] Cut014343
  Base = -> Fusion248002050263
  Refine = true
  Tool = -> Fusion248002050264
FEATURE [Part::Cylinder] Cylinder1435  label="Cylinder1697"
  Angle = 360
  AttacherType = Attacher::AttachEngine3D
  Height = 20
  Placement = pos=(152,46,31.5) rot=(-1,0,0;1.5708rad)
  Radius = 6.15
FEATURE [Part::Cut] Cut014342
  Base = -> Cut014343
  Refine = true
  Tool = -> Cylinder1435
FEATURE [Part::Cut] Cut078018
  Base = -> Cut014342
  Refine = true
  Tool = -> Cylinder1432
FEATURE [Part::Chamfer] Chamfer132
  Base = -> Cut078018
  Edges = 1 edges r=1.999: [Edge4]
FEATURE [Part::Chamfer] Chamfer133
  Base = -> Chamfer132
  Edges = 1 edges r=7.499: [Edge19]
FEATURE [Part::Fillet] Fillet445
  Base = -> Chamfer133
  Edges = 1 edges r=10: [Edge17]
FEATURE [Part::Fillet] Fillet446
  Base = -> Fillet445
  Edges = 2 edges r=5: [Edge22,Edge28]
  Placement = pos=(-0.5,-6,0) rot=(0,0,1;0rad)
FEATURE [Part::Cylinder] Cylinder1436  label="Cylinder1698"
  Angle = 360
  AttacherType = Attacher::AttachEngine3D
  Height = 10
  Placement = pos=(164.5,62,24) rot=(1,0,0;1.5708rad)
  Radius = 1.6
FEATURE [Part::Cylinder] Cylinder1437  label="Cylinder1699"
  Angle = 360
  AttacherType = Attacher::AttachEngine3D
  Height = 10
  Placement = pos=(177.5,62,24) rot=(1,0,0;1.5708rad)
  Radius = 1.6
FEATURE [Part::MultiFuse] Fusion248002050265
  Placement = pos=(-0.25,0,0) rot=(0,0,1;0rad)
  Refine = true
  Shapes = -> [Cylinder1437,Cylinder1436]
FEATURE [Part::Box] Box611  label="Cube837"
  AttacherType = Attacher::AttachEngine3D
  Height = 11
  Length = 26.5
  Placement = pos=(154.5,52,17) rot=(0,0,1;0rad)
  Width = 5
FEATURE [Part::Cut] Cut078019
  Base = -> Box611
  Refine = true
  Tool = -> Fusion248002050265
FEATURE [Part::Chamfer] Chamfer134
  Base = -> Cut078019
  Edges = 1 edges r=4: [Edge2]
FEATURE [Part::MultiFuse] Fusion248002050266  label="crane-rotating-cylinder-holder-left-thick"
  Placement = pos=(0.25,0,0) rot=(0,0,1;0rad)
  Refine = true
  Shapes = -> [Fillet446,Chamfer134]
FEATURE [App::DocumentObjectGroup] Group006  label="rotation-wormscrew"
  Group = -> [Cut078013,Cut078014,Fusion248002050266]
